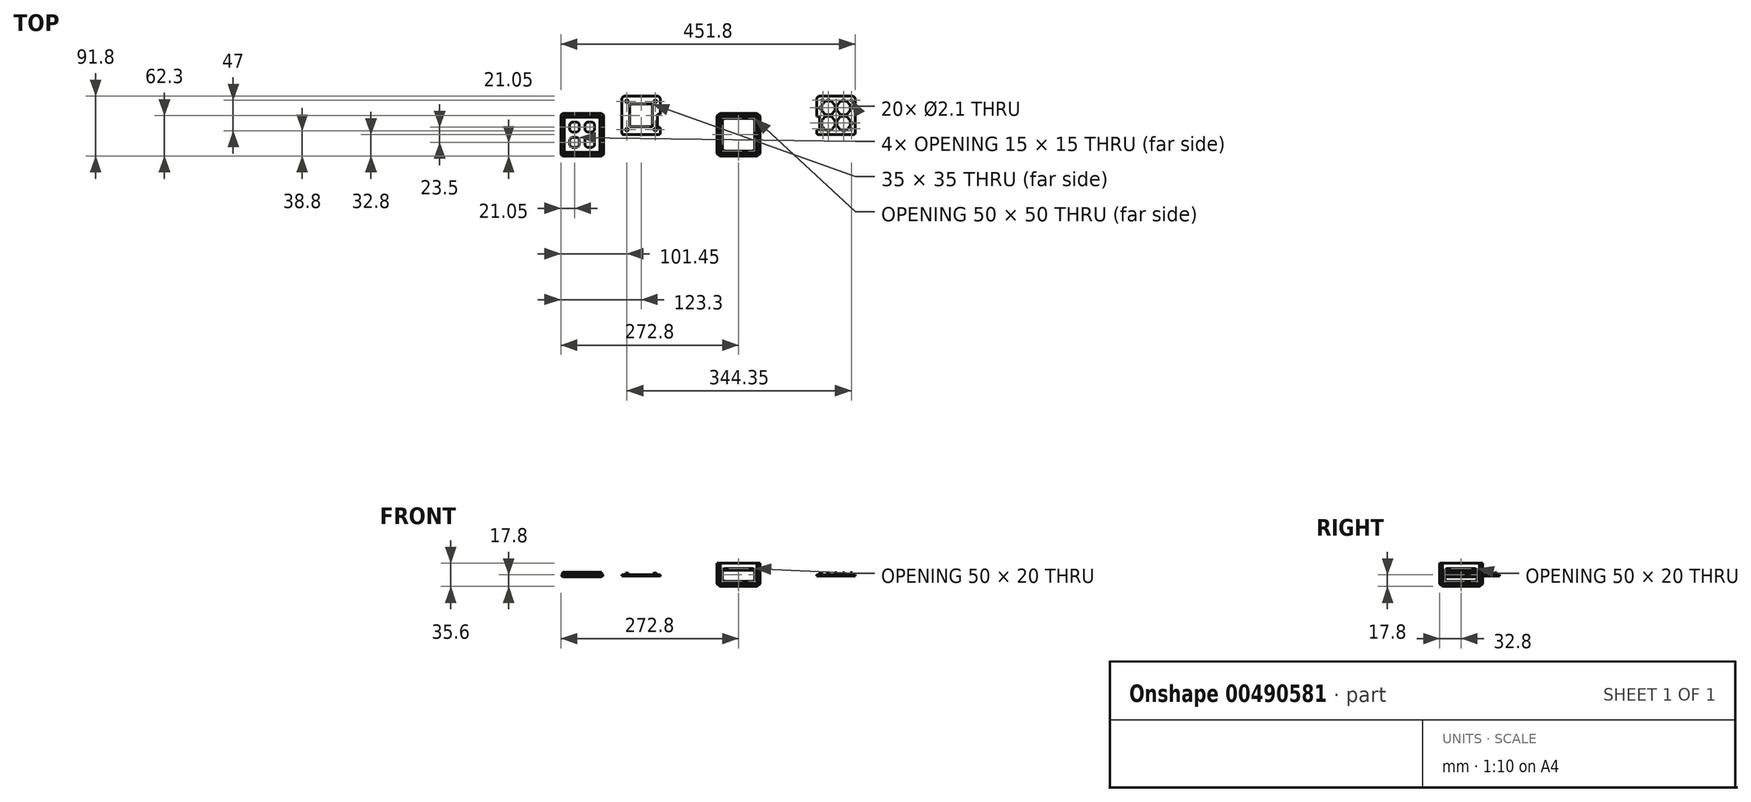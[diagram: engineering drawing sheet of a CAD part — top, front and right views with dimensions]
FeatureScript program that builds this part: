
annotation { "Feature Type Name" : "Feature", "Feature Type Description" : "" }
export const myFeature = defineFeature(function(context is Context, id is Id, definition is map)
    precondition{}
    {
        {
            assignVariable(context, id + "F0", {"name" : "Grosor", "anyValue" : 2.8});
        }
        {
            assignVariable(context, id + "F1", {"name" : "AltoPlaca", "anyValue" : 15});
        }
        {
            assignVariable(context, id + "F2", {"name" : "AltoBriX", "anyValue" : 15});
        }
        {
            var Q0;
            Q0=qCreatedBy(makeId("Top.planeOp"),FACE);
            var sketch = newSketch(context, id + "F3", { "sketchPlane" : qUnion([Q0])});
            skLineSegment(sketch, "E0.bottom", {"start": v(30, -30) * mm, "end": v(-30, -30) * mm});
            skLineSegment(sketch, "E0.top", {"start": v(30, 30) * mm, "end": v(-30, 30) * mm});
            skLineSegment(sketch, "E0.left", {"start": v(30, -30) * mm, "end": v(30, 30) * mm});
            skLineSegment(sketch, "E0.right", {"start": v(-30, -30) * mm, "end": v(-30, 30) * mm});
            skPoint(sketch, "E0.middle", {"position": v(0, 0) * mm});
            skLineSegment(sketch, "E1.0", {"start": v(32.8, 32.8) * mm, "end": v(-32.8, 32.8) * mm});
            skLineSegment(sketch, "E1.1", {"start": v(32.8, -32.8) * mm, "end": v(32.8, 32.8) * mm});
            skLineSegment(sketch, "E1.2", {"start": v(32.8, -32.8) * mm, "end": v(-32.8, -32.8) * mm});
            skLineSegment(sketch, "E1.3", {"start": v(-32.8, -32.8) * mm, "end": v(-32.8, 32.8) * mm});
            skLineSegment(sketch, "E2.bottom", {"start": v(-25, 32.8) * mm, "end": v(25, 32.8) * mm});
            skLineSegment(sketch, "E2.top", {"start": v(-25, -32.8) * mm, "end": v(25, -32.8) * mm});
            skLineSegment(sketch, "E2.left", {"start": v(-25, 32.8) * mm, "end": v(-25, -32.8) * mm});
            skLineSegment(sketch, "E2.right", {"start": v(25, 32.8) * mm, "end": v(25, -32.8) * mm});
            skLineSegment(sketch, "E3.bottom", {"start": v(-32.8, 25) * mm, "end": v(32.8, 25) * mm});
            skLineSegment(sketch, "E3.top", {"start": v(-32.8, -25) * mm, "end": v(32.8, -25) * mm});
            skLineSegment(sketch, "E3.left", {"start": v(-32.8, 25) * mm, "end": v(-32.8, -25) * mm});
            skLineSegment(sketch, "E3.right", {"start": v(32.8, 25) * mm, "end": v(32.8, -25) * mm});
            skSolve(sketch);
        }
        {
            var Q0;
            {var subQ0=sQuery(id+"F3.wireOp",EDGE,"E2.right");var subQ1=sQuery(id+"F3.wireOp",EDGE,"E0.top");var subQ2=makeQuery(id+"F3.imprint","INTERSECT",VERTEX,{"derivedFrom":[subQ1,subQ0]});Q0=makeQuery(id+"F3.imprint","IMPRINT",FACE,{"disambiguationData":[TD([[makeQuery(id+"F3.imprint","IMPRINT",EDGE,{"disambiguationData":[TD([[subQ2,-1.0]])],"derivedFrom":subQ1}),-1.0]])]});}
            var Q1;
            {var subQ7=sQuery(id+"F3.wireOp",EDGE,"E0.right");var subQ8=sQuery(id+"F3.wireOp",EDGE,"E0.top");var subQ9=makeQuery(id+"F3.imprint","INTERSECT",VERTEX,{"derivedFrom":[subQ8,subQ7]});Q1=makeQuery(id+"F3.imprint","IMPRINT",FACE,{"disambiguationData":[TD([[makeQuery(id+"F3.imprint","IMPRINT",EDGE,{"disambiguationData":[TD([[subQ9,1.0]])],"derivedFrom":subQ8}),-1.0]])]});}
            var Q2;
            {var subQ6=sQuery(id+"F3.wireOp",EDGE,"E0.top");var subQ9=sQuery(id+"F3.wireOp",EDGE,"E2.right");var subQ11=makeQuery(id+"F3.imprint","INTERSECT",VERTEX,{"derivedFrom":[subQ6,subQ9]});Q2=makeQuery(id+"F3.imprint","IMPRINT",FACE,{"disambiguationData":[TD([[makeQuery(id+"F3.imprint","IMPRINT",EDGE,{"disambiguationData":[TD([[subQ11,1.0]])],"derivedFrom":subQ6}),-1.0]])]});}
            var Q3;
            {var subQ0=sQuery(id+"F3.wireOp",EDGE,"E3.top");var subQ1=sQuery(id+"F3.wireOp",EDGE,"E0.left");var subQ2=makeQuery(id+"F3.imprint","INTERSECT",VERTEX,{"derivedFrom":[subQ1,subQ0]});Q3=makeQuery(id+"F3.imprint","IMPRINT",FACE,{"disambiguationData":[TD([[makeQuery(id+"F3.imprint","IMPRINT",EDGE,{"disambiguationData":[TD([[subQ2,-1.0]])],"derivedFrom":subQ1}),-1.0]])]});}
            var Q4;
            {var subQ0=sQuery(id+"F3.wireOp",EDGE,"E2.right");var subQ8=sQuery(id+"F3.wireOp",EDGE,"E0.bottom");var subQ11=makeQuery(id+"F3.imprint","INTERSECT",VERTEX,{"derivedFrom":[subQ8,subQ0]});Q4=makeQuery(id+"F3.imprint","IMPRINT",FACE,{"disambiguationData":[TD([[makeQuery(id+"F3.imprint","IMPRINT",EDGE,{"disambiguationData":[TD([[subQ11,1.0]])],"derivedFrom":subQ8}),1.0]])]});}
            var Q5;
            {var subQ0=sQuery(id+"F3.wireOp",EDGE,"E2.right");var subQ1=sQuery(id+"F3.wireOp",EDGE,"E0.bottom");var subQ2=makeQuery(id+"F3.imprint","INTERSECT",VERTEX,{"derivedFrom":[subQ1,subQ0]});Q5=makeQuery(id+"F3.imprint","IMPRINT",FACE,{"disambiguationData":[TD([[makeQuery(id+"F3.imprint","IMPRINT",EDGE,{"disambiguationData":[TD([[subQ2,-1.0]])],"derivedFrom":subQ1}),1.0]])]});}
            var Q6;
            {var subQ6=sQuery(id+"F3.wireOp",EDGE,"E0.right");var subQ9=sQuery(id+"F3.wireOp",EDGE,"E0.bottom");var subQ10=makeQuery(id+"F3.imprint","INTERSECT",VERTEX,{"derivedFrom":[subQ9,subQ6]});Q6=makeQuery(id+"F3.imprint","IMPRINT",FACE,{"disambiguationData":[TD([[makeQuery(id+"F3.imprint","IMPRINT",EDGE,{"disambiguationData":[TD([[subQ10,1.0]])],"derivedFrom":subQ9}),1.0]])]});}
            var Q7;
            {var subQ0=sQuery(id+"F3.wireOp",EDGE,"E3.top");var subQ1=sQuery(id+"F3.wireOp",EDGE,"E0.right");var subQ2=makeQuery(id+"F3.imprint","INTERSECT",VERTEX,{"derivedFrom":[subQ1,subQ0]});Q7=makeQuery(id+"F3.imprint","IMPRINT",FACE,{"disambiguationData":[TD([[makeQuery(id+"F3.imprint","IMPRINT",EDGE,{"disambiguationData":[TD([[subQ2,-1.0]])],"derivedFrom":subQ1}),1.0]])]});}
            var Q8;
            {var subQ0=sQuery(id+"F3.wireOp",EDGE,"E2.right");var subQ1=sQuery(id+"F3.wireOp",EDGE,"E0.bottom");var subQ2=makeQuery(id+"F3.imprint","INTERSECT",VERTEX,{"derivedFrom":[subQ1,subQ0]});Q8=makeQuery(id+"F3.imprint","IMPRINT",FACE,{"disambiguationData":[TD([[makeQuery(id+"F3.imprint","IMPRINT",EDGE,{"disambiguationData":[TD([[subQ2,1.0]])],"derivedFrom":subQ1}),-1.0]])]});}
            var Q9;
            {var subQ0=sQuery(id+"F3.wireOp",EDGE,"E2.right");var subQ1=sQuery(id+"F3.wireOp",EDGE,"E0.top");var subQ2=makeQuery(id+"F3.imprint","INTERSECT",VERTEX,{"derivedFrom":[subQ1,subQ0]});Q9=makeQuery(id+"F3.imprint","IMPRINT",FACE,{"disambiguationData":[TD([[makeQuery(id+"F3.imprint","IMPRINT",EDGE,{"disambiguationData":[TD([[subQ2,1.0]])],"derivedFrom":subQ1}),1.0]])]});}
            var Q10;
            {var subQ0=sQuery(id+"F3.wireOp",EDGE,"E0.right");var subQ1=sQuery(id+"F3.wireOp",EDGE,"E0.top");var subQ2=makeQuery(id+"F3.imprint","INTERSECT",VERTEX,{"derivedFrom":[subQ1,subQ0]});Q10=makeQuery(id+"F3.imprint","IMPRINT",FACE,{"disambiguationData":[TD([[makeQuery(id+"F3.imprint","IMPRINT",EDGE,{"disambiguationData":[TD([[subQ2,1.0]])],"derivedFrom":subQ1}),1.0]])]});}
            var Q11;
            {var subQ0=sQuery(id+"F3.wireOp",EDGE,"E3.top");var subQ1=sQuery(id+"F3.wireOp",EDGE,"E0.right");var subQ2=makeQuery(id+"F3.imprint","INTERSECT",VERTEX,{"derivedFrom":[subQ1,subQ0]});Q11=makeQuery(id+"F3.imprint","IMPRINT",FACE,{"disambiguationData":[TD([[makeQuery(id+"F3.imprint","IMPRINT",EDGE,{"disambiguationData":[TD([[subQ2,-1.0]])],"derivedFrom":subQ1}),-1.0]])]});}
            var Q12;
            {var subQ0=sQuery(id+"F3.wireOp",EDGE,"E3.top");var subQ1=sQuery(id+"F3.wireOp",EDGE,"E0.left");var subQ2=makeQuery(id+"F3.imprint","INTERSECT",VERTEX,{"derivedFrom":[subQ1,subQ0]});Q12=makeQuery(id+"F3.imprint","IMPRINT",FACE,{"disambiguationData":[TD([[makeQuery(id+"F3.imprint","IMPRINT",EDGE,{"disambiguationData":[TD([[subQ2,-1.0]])],"derivedFrom":subQ1}),1.0]])]});}
            var Q13;
            {var subQ0=sQuery(id+"F3.wireOp",EDGE,"E0.right");var subQ1=sQuery(id+"F3.wireOp",EDGE,"E0.bottom");var subQ2=makeQuery(id+"F3.imprint","INTERSECT",VERTEX,{"derivedFrom":[subQ1,subQ0]});Q13=makeQuery(id+"F3.imprint","IMPRINT",FACE,{"disambiguationData":[TD([[makeQuery(id+"F3.imprint","IMPRINT",EDGE,{"disambiguationData":[TD([[subQ2,1.0]])],"derivedFrom":subQ1}),-1.0]])]});}
            var Q14;
            {var subQ0=sQuery(id+"F3.wireOp",EDGE,"E2.right");var subQ1=sQuery(id+"F3.wireOp",EDGE,"E0.bottom");var subQ2=makeQuery(id+"F3.imprint","INTERSECT",VERTEX,{"derivedFrom":[subQ1,subQ0]});Q14=makeQuery(id+"F3.imprint","IMPRINT",FACE,{"disambiguationData":[TD([[makeQuery(id+"F3.imprint","IMPRINT",EDGE,{"disambiguationData":[TD([[subQ2,-1.0]])],"derivedFrom":subQ1}),-1.0]])]});}
            var Q15;
            {var subQ0=sQuery(id+"F3.wireOp",EDGE,"E2.right");var subQ1=sQuery(id+"F3.wireOp",EDGE,"E0.top");var subQ2=makeQuery(id+"F3.imprint","INTERSECT",VERTEX,{"derivedFrom":[subQ1,subQ0]});Q15=makeQuery(id+"F3.imprint","IMPRINT",FACE,{"disambiguationData":[TD([[makeQuery(id+"F3.imprint","IMPRINT",EDGE,{"disambiguationData":[TD([[subQ2,-1.0]])],"derivedFrom":subQ1}),1.0]])]});}
            extrude(context, id + "F4", {"entities" : qUnion([Q0, Q1, Q2, Q3, Q4, Q5, Q6, Q7, Q8, Q9, Q10, Q11, Q12, Q13, Q14, Q15]), "depth" : (getVariable(context, 'AltoBriX') + getVariable(context, 'Grosor')) * mm, "hasSecondDirection" : true, "secondDirectionOppositeDirection" : true, "secondDirectionDepth" : (getVariable(context, 'AltoPlaca') + getVariable(context, 'Grosor')) * mm});
        }
        {
            var Q0;
            {var subQ0=sQuery(id+"F3.wireOp",EDGE,"E3.top");var subQ1=sQuery(id+"F3.wireOp",EDGE,"E0.right");var subQ2=makeQuery(id+"F3.imprint","INTERSECT",VERTEX,{"derivedFrom":[subQ1,subQ0]});Q0=makeQuery(id+"F3.imprint","IMPRINT",FACE,{"disambiguationData":[TD([[makeQuery(id+"F3.imprint","IMPRINT",EDGE,{"disambiguationData":[TD([[subQ2,-1.0]])],"derivedFrom":subQ1}),-1.0]])]});}
            var Q1;
            {var subQ0=sQuery(id+"F3.wireOp",EDGE,"E2.right");var subQ1=sQuery(id+"F3.wireOp",EDGE,"E0.top");var subQ2=makeQuery(id+"F3.imprint","INTERSECT",VERTEX,{"derivedFrom":[subQ1,subQ0]});Q1=makeQuery(id+"F3.imprint","IMPRINT",FACE,{"disambiguationData":[TD([[makeQuery(id+"F3.imprint","IMPRINT",EDGE,{"disambiguationData":[TD([[subQ2,-1.0]])],"derivedFrom":subQ1}),1.0]])]});}
            var Q2;
            {var subQ0=sQuery(id+"F3.wireOp",EDGE,"E0.right");var subQ1=sQuery(id+"F3.wireOp",EDGE,"E0.top");var subQ2=makeQuery(id+"F3.imprint","INTERSECT",VERTEX,{"derivedFrom":[subQ1,subQ0]});Q2=makeQuery(id+"F3.imprint","IMPRINT",FACE,{"disambiguationData":[TD([[makeQuery(id+"F3.imprint","IMPRINT",EDGE,{"disambiguationData":[TD([[subQ2,1.0]])],"derivedFrom":subQ1}),1.0]])]});}
            var Q3;
            {var subQ0=sQuery(id+"F3.wireOp",EDGE,"E3.top");var subQ1=sQuery(id+"F3.wireOp",EDGE,"E0.left");var subQ2=makeQuery(id+"F3.imprint","INTERSECT",VERTEX,{"derivedFrom":[subQ1,subQ0]});Q3=makeQuery(id+"F3.imprint","IMPRINT",FACE,{"disambiguationData":[TD([[makeQuery(id+"F3.imprint","IMPRINT",EDGE,{"disambiguationData":[TD([[subQ2,-1.0]])],"derivedFrom":subQ1}),1.0]])]});}
            var Q4;
            {var subQ0=sQuery(id+"F3.wireOp",EDGE,"E2.right");var subQ1=sQuery(id+"F3.wireOp",EDGE,"E0.top");var subQ2=makeQuery(id+"F3.imprint","INTERSECT",VERTEX,{"derivedFrom":[subQ1,subQ0]});Q4=makeQuery(id+"F3.imprint","IMPRINT",FACE,{"disambiguationData":[TD([[makeQuery(id+"F3.imprint","IMPRINT",EDGE,{"disambiguationData":[TD([[subQ2,1.0]])],"derivedFrom":subQ1}),1.0]])]});}
            var Q5;
            {var subQ0=sQuery(id+"F3.wireOp",EDGE,"E0.right");var subQ1=sQuery(id+"F3.wireOp",EDGE,"E0.bottom");var subQ2=makeQuery(id+"F3.imprint","INTERSECT",VERTEX,{"derivedFrom":[subQ1,subQ0]});Q5=makeQuery(id+"F3.imprint","IMPRINT",FACE,{"disambiguationData":[TD([[makeQuery(id+"F3.imprint","IMPRINT",EDGE,{"disambiguationData":[TD([[subQ2,1.0]])],"derivedFrom":subQ1}),-1.0]])]});}
            var Q6;
            {var subQ0=sQuery(id+"F3.wireOp",EDGE,"E2.right");var subQ1=sQuery(id+"F3.wireOp",EDGE,"E0.bottom");var subQ2=makeQuery(id+"F3.imprint","INTERSECT",VERTEX,{"derivedFrom":[subQ1,subQ0]});Q6=makeQuery(id+"F3.imprint","IMPRINT",FACE,{"disambiguationData":[TD([[makeQuery(id+"F3.imprint","IMPRINT",EDGE,{"disambiguationData":[TD([[subQ2,-1.0]])],"derivedFrom":subQ1}),-1.0]])]});}
            var Q7;
            {var subQ0=sQuery(id+"F3.wireOp",EDGE,"E2.right");var subQ1=sQuery(id+"F3.wireOp",EDGE,"E0.bottom");var subQ2=makeQuery(id+"F3.imprint","INTERSECT",VERTEX,{"derivedFrom":[subQ1,subQ0]});Q7=makeQuery(id+"F3.imprint","IMPRINT",FACE,{"disambiguationData":[TD([[makeQuery(id+"F3.imprint","IMPRINT",EDGE,{"disambiguationData":[TD([[subQ2,1.0]])],"derivedFrom":subQ1}),-1.0]])]});}
            extrude(context, id + "F5", {"entities" : qUnion([Q0, Q1, Q2, Q3, Q4, Q5, Q6, Q7]), "operationType" : NewBodyOperationType.REMOVE, "depth" : (getVariable(context, 'AltoBriX') + getVariable(context, 'Grosor')) * mm, "hasSecondDirection" : true, "secondDirectionOppositeDirection" : true, "secondDirectionDepth" : (getVariable(context, 'AltoPlaca')) * mm});
        }
        {
            var Q0;
            {var subQ0=sQuery(id+"F3.wireOp",EDGE,"E3.top");var subQ1=sQuery(id+"F3.wireOp",EDGE,"E0.right");var subQ2=makeQuery(id+"F3.imprint","INTERSECT",VERTEX,{"derivedFrom":[subQ1,subQ0]});Q0=makeQuery(id+"F3.imprint","IMPRINT",FACE,{"disambiguationData":[TD([[makeQuery(id+"F3.imprint","IMPRINT",EDGE,{"disambiguationData":[TD([[subQ2,-1.0]])],"derivedFrom":subQ1}),1.0]])]});}
            var Q1;
            {var subQ0=sQuery(id+"F3.wireOp",EDGE,"E3.top");var subQ1=sQuery(id+"F3.wireOp",EDGE,"E0.left");var subQ2=makeQuery(id+"F3.imprint","INTERSECT",VERTEX,{"derivedFrom":[subQ1,subQ0]});Q1=makeQuery(id+"F3.imprint","IMPRINT",FACE,{"disambiguationData":[TD([[makeQuery(id+"F3.imprint","IMPRINT",EDGE,{"disambiguationData":[TD([[subQ2,-1.0]])],"derivedFrom":subQ1}),-1.0]])]});}
            var Q2;
            {var subQ0=sQuery(id+"F3.wireOp",EDGE,"E2.right");var subQ1=sQuery(id+"F3.wireOp",EDGE,"E0.bottom");var subQ2=makeQuery(id+"F3.imprint","INTERSECT",VERTEX,{"derivedFrom":[subQ1,subQ0]});Q2=makeQuery(id+"F3.imprint","IMPRINT",FACE,{"disambiguationData":[TD([[makeQuery(id+"F3.imprint","IMPRINT",EDGE,{"disambiguationData":[TD([[subQ2,-1.0]])],"derivedFrom":subQ1}),1.0]])]});}
            var Q3;
            {var subQ0=sQuery(id+"F3.wireOp",EDGE,"E2.right");var subQ1=sQuery(id+"F3.wireOp",EDGE,"E0.top");var subQ2=makeQuery(id+"F3.imprint","INTERSECT",VERTEX,{"derivedFrom":[subQ1,subQ0]});Q3=makeQuery(id+"F3.imprint","IMPRINT",FACE,{"disambiguationData":[TD([[makeQuery(id+"F3.imprint","IMPRINT",EDGE,{"disambiguationData":[TD([[subQ2,-1.0]])],"derivedFrom":subQ1}),-1.0]])]});}
            extrude(context, id + "F6", {"entities" : qUnion([Q0, Q1, Q2, Q3]), "operationType" : NewBodyOperationType.REMOVE, "depth" : (getVariable(context, 'AltoBriX') - 5) * mm, "hasSecondDirection" : true, "secondDirectionOppositeDirection" : true, "secondDirectionDepth" : (getVariable(context, 'AltoPlaca') - 5) * mm});
        }
        {
            var Q0;
            {var subQ0=sQuery(id+"F3.wireOp",EDGE,"E3.bottom");Q0=makeQuery(id+"F6.boolean.opBoolean","COPY",EDGE,{"derivedFrom":makeQuery(id+"F6.opExtrude","CAP_EDGE",EDGE,{"disambiguationData":[OSD([subQ0]),TDD([makeQuery(id+"F3.imprint","IMPRINT",EDGE,{"disambiguationData":[TD([[makeQuery(id+"F3.imprint","INTERSECT",VERTEX,{"derivedFrom":[sQuery(id+"F3.wireOp",EDGE,"E0.right"),subQ0]}),1.0]])],"derivedFrom":subQ0})])],"isStart":false})});}
            var Q1;
            {var subQ0=sQuery(id+"F3.wireOp",EDGE,"E3.bottom");Q1=makeQuery(id+"F6.boolean.opBoolean","COPY",EDGE,{"derivedFrom":makeQuery(id+"F6.opExtrude","CAP_EDGE",EDGE,{"disambiguationData":[OSD([subQ0]),TDD([makeQuery(id+"F3.imprint","IMPRINT",EDGE,{"disambiguationData":[TD([[makeQuery(id+"F3.imprint","INTERSECT",VERTEX,{"derivedFrom":[sQuery(id+"F3.wireOp",EDGE,"E0.right"),subQ0]}),1.0]])],"derivedFrom":subQ0})])],"isStart":true})});}
            var Q2;
            {var subQ0=sQuery(id+"F3.wireOp",EDGE,"E3.top");Q2=makeQuery(id+"F6.boolean.opBoolean","COPY",EDGE,{"derivedFrom":makeQuery(id+"F6.opExtrude","CAP_EDGE",EDGE,{"disambiguationData":[OSD([subQ0]),TDD([makeQuery(id+"F3.imprint","IMPRINT",EDGE,{"disambiguationData":[TD([[makeQuery(id+"F3.imprint","INTERSECT",VERTEX,{"derivedFrom":[sQuery(id+"F3.wireOp",EDGE,"E0.right"),subQ0]}),1.0]])],"derivedFrom":subQ0})])],"isStart":false})});}
            var Q3;
            {var subQ0=sQuery(id+"F3.wireOp",EDGE,"E2.right");Q3=makeQuery(id+"F6.boolean.opBoolean","COPY",EDGE,{"derivedFrom":makeQuery(id+"F6.opExtrude","CAP_EDGE",EDGE,{"disambiguationData":[OSD([subQ0]),TDD([makeQuery(id+"F3.imprint","IMPRINT",EDGE,{"disambiguationData":[TD([[makeQuery(id+"F3.imprint","INTERSECT",VERTEX,{"derivedFrom":[sQuery(id+"F3.wireOp",EDGE,"E0.bottom"),subQ0]}),-1.0]])],"derivedFrom":subQ0})])],"isStart":false})});}
            var Q4;
            {var subQ0=sQuery(id+"F3.wireOp",EDGE,"E3.top");Q4=makeQuery(id+"F6.boolean.opBoolean","COPY",EDGE,{"derivedFrom":makeQuery(id+"F6.opExtrude","CAP_EDGE",EDGE,{"disambiguationData":[OSD([subQ0]),TDD([makeQuery(id+"F3.imprint","IMPRINT",EDGE,{"disambiguationData":[TD([[makeQuery(id+"F3.imprint","INTERSECT",VERTEX,{"derivedFrom":[sQuery(id+"F3.wireOp",EDGE,"E0.left"),subQ0]}),-1.0]])],"derivedFrom":subQ0})])],"isStart":false})});}
            var Q5;
            {var subQ0=sQuery(id+"F3.wireOp",EDGE,"E3.top");Q5=makeQuery(id+"F6.boolean.opBoolean","COPY",EDGE,{"derivedFrom":makeQuery(id+"F6.opExtrude","CAP_EDGE",EDGE,{"disambiguationData":[OSD([subQ0]),TDD([makeQuery(id+"F3.imprint","IMPRINT",EDGE,{"disambiguationData":[TD([[makeQuery(id+"F3.imprint","INTERSECT",VERTEX,{"derivedFrom":[sQuery(id+"F3.wireOp",EDGE,"E0.left"),subQ0]}),-1.0]])],"derivedFrom":subQ0})])],"isStart":true})});}
            var Q6;
            {var subQ0=sQuery(id+"F3.wireOp",EDGE,"E2.right");Q6=makeQuery(id+"F6.boolean.opBoolean","COPY",EDGE,{"derivedFrom":makeQuery(id+"F6.opExtrude","CAP_EDGE",EDGE,{"disambiguationData":[OSD([subQ0]),TDD([makeQuery(id+"F3.imprint","IMPRINT",EDGE,{"disambiguationData":[TD([[makeQuery(id+"F3.imprint","INTERSECT",VERTEX,{"derivedFrom":[sQuery(id+"F3.wireOp",EDGE,"E0.bottom"),subQ0]}),-1.0]])],"derivedFrom":subQ0})])],"isStart":true})});}
            var Q7;
            {var subQ0=sQuery(id+"F3.wireOp",EDGE,"E3.top");Q7=makeQuery(id+"F6.boolean.opBoolean","COPY",EDGE,{"derivedFrom":makeQuery(id+"F6.opExtrude","CAP_EDGE",EDGE,{"disambiguationData":[OSD([subQ0]),TDD([makeQuery(id+"F3.imprint","IMPRINT",EDGE,{"disambiguationData":[TD([[makeQuery(id+"F3.imprint","INTERSECT",VERTEX,{"derivedFrom":[sQuery(id+"F3.wireOp",EDGE,"E0.right"),subQ0]}),1.0]])],"derivedFrom":subQ0})])],"isStart":true})});}
            var Q8;
            {var subQ0=sQuery(id+"F3.wireOp",EDGE,"E2.left");Q8=makeQuery(id+"F6.boolean.opBoolean","COPY",EDGE,{"derivedFrom":makeQuery(id+"F6.opExtrude","CAP_EDGE",EDGE,{"disambiguationData":[OSD([subQ0]),TDD([makeQuery(id+"F3.imprint","IMPRINT",EDGE,{"disambiguationData":[TD([[makeQuery(id+"F3.imprint","INTERSECT",VERTEX,{"derivedFrom":[sQuery(id+"F3.wireOp",EDGE,"E1.2"),subQ0]}),1.0]])],"derivedFrom":subQ0})])],"isStart":true})});}
            var Q9;
            {var subQ0=sQuery(id+"F3.wireOp",EDGE,"E2.left");Q9=makeQuery(id+"F6.boolean.opBoolean","COPY",EDGE,{"derivedFrom":makeQuery(id+"F6.opExtrude","CAP_EDGE",EDGE,{"disambiguationData":[OSD([subQ0]),TDD([makeQuery(id+"F3.imprint","IMPRINT",EDGE,{"disambiguationData":[TD([[makeQuery(id+"F3.imprint","INTERSECT",VERTEX,{"derivedFrom":[sQuery(id+"F3.wireOp",EDGE,"E1.2"),subQ0]}),1.0]])],"derivedFrom":subQ0})])],"isStart":false})});}
            var Q10;
            {var subQ0=sQuery(id+"F3.wireOp",EDGE,"E3.bottom");Q10=makeQuery(id+"F6.boolean.opBoolean","COPY",EDGE,{"derivedFrom":makeQuery(id+"F6.opExtrude","CAP_EDGE",EDGE,{"disambiguationData":[OSD([subQ0]),TDD([makeQuery(id+"F3.imprint","IMPRINT",EDGE,{"disambiguationData":[TD([[makeQuery(id+"F3.imprint","INTERSECT",VERTEX,{"derivedFrom":[sQuery(id+"F3.wireOp",EDGE,"E1.1"),subQ0]}),1.0]])],"derivedFrom":subQ0})])],"isStart":true})});}
            var Q11;
            {var subQ0=sQuery(id+"F3.wireOp",EDGE,"E3.bottom");Q11=makeQuery(id+"F6.boolean.opBoolean","COPY",EDGE,{"derivedFrom":makeQuery(id+"F6.opExtrude","CAP_EDGE",EDGE,{"disambiguationData":[OSD([subQ0]),TDD([makeQuery(id+"F3.imprint","IMPRINT",EDGE,{"disambiguationData":[TD([[makeQuery(id+"F3.imprint","INTERSECT",VERTEX,{"derivedFrom":[sQuery(id+"F3.wireOp",EDGE,"E1.1"),subQ0]}),1.0]])],"derivedFrom":subQ0})])],"isStart":false})});}
            var Q12;
            {var subQ0=sQuery(id+"F3.wireOp",EDGE,"E2.left");Q12=makeQuery(id+"F6.boolean.opBoolean","COPY",EDGE,{"derivedFrom":makeQuery(id+"F6.opExtrude","CAP_EDGE",EDGE,{"disambiguationData":[OSD([subQ0]),TDD([makeQuery(id+"F3.imprint","IMPRINT",EDGE,{"disambiguationData":[TD([[makeQuery(id+"F3.imprint","INTERSECT",VERTEX,{"derivedFrom":[sQuery(id+"F3.wireOp",EDGE,"E1.0"),subQ0]}),-1.0]])],"derivedFrom":subQ0})])],"isStart":false})});}
            var Q13;
            {var subQ0=sQuery(id+"F3.wireOp",EDGE,"E2.left");Q13=makeQuery(id+"F6.boolean.opBoolean","COPY",EDGE,{"derivedFrom":makeQuery(id+"F6.opExtrude","CAP_EDGE",EDGE,{"disambiguationData":[OSD([subQ0]),TDD([makeQuery(id+"F3.imprint","IMPRINT",EDGE,{"disambiguationData":[TD([[makeQuery(id+"F3.imprint","INTERSECT",VERTEX,{"derivedFrom":[sQuery(id+"F3.wireOp",EDGE,"E1.0"),subQ0]}),-1.0]])],"derivedFrom":subQ0})])],"isStart":true})});}
            var Q14;
            {var subQ0=sQuery(id+"F3.wireOp",EDGE,"E2.right");Q14=makeQuery(id+"F6.boolean.opBoolean","COPY",EDGE,{"derivedFrom":makeQuery(id+"F6.opExtrude","CAP_EDGE",EDGE,{"disambiguationData":[OSD([subQ0]),TDD([makeQuery(id+"F3.imprint","IMPRINT",EDGE,{"disambiguationData":[TD([[makeQuery(id+"F3.imprint","INTERSECT",VERTEX,{"derivedFrom":[sQuery(id+"F3.wireOp",EDGE,"E0.top"),subQ0]}),1.0]])],"derivedFrom":subQ0})])],"isStart":false})});}
            var Q15;
            {var subQ0=sQuery(id+"F3.wireOp",EDGE,"E2.right");Q15=makeQuery(id+"F6.boolean.opBoolean","COPY",EDGE,{"derivedFrom":makeQuery(id+"F6.opExtrude","CAP_EDGE",EDGE,{"disambiguationData":[OSD([subQ0]),TDD([makeQuery(id+"F3.imprint","IMPRINT",EDGE,{"disambiguationData":[TD([[makeQuery(id+"F3.imprint","INTERSECT",VERTEX,{"derivedFrom":[sQuery(id+"F3.wireOp",EDGE,"E0.top"),subQ0]}),1.0]])],"derivedFrom":subQ0})])],"isStart":true})});}
            var Q16;
            Q16=makeQuery(id+"F4.opExtrude","SWEPT_EDGE",EDGE,{"disambiguationData":[OSD([sQuery(id+"F3.wireOp",EDGE,"E2.right"),sQuery(id+"F3.wireOp",EDGE,"E3.top")])]});
            var Q17;
            Q17=makeQuery(id+"F4.opExtrude","SWEPT_EDGE",EDGE,{"disambiguationData":[OSD([sQuery(id+"F3.wireOp",EDGE,"E2.left"),sQuery(id+"F3.wireOp",EDGE,"E3.top")])]});
            var Q18;
            Q18=makeQuery(id+"F4.opExtrude","SWEPT_EDGE",EDGE,{"disambiguationData":[OSD([sQuery(id+"F3.wireOp",EDGE,"E2.left"),sQuery(id+"F3.wireOp",EDGE,"E3.bottom")])]});
            var Q19;
            Q19=makeQuery(id+"F4.opExtrude","SWEPT_EDGE",EDGE,{"disambiguationData":[OSD([sQuery(id+"F3.wireOp",EDGE,"E2.right"),sQuery(id+"F3.wireOp",EDGE,"E3.bottom")])]});
            fillet(context, id + "F7", {"entities" : qUnion([Q0, Q1, Q2, Q3, Q4, Q5, Q6, Q7, Q8, Q9, Q10, Q11, Q12, Q13, Q14, Q15, Q16, Q17, Q18, Q19]), "radius" : 5 * mm, "tangentPropagation" : true, "allowEdgeOverflow" : false});
        }
        {
            var Q0;
            Q0=qCreatedBy(makeId("Top.planeOp"),FACE);
            cPlane(context, id + "F8", {"entities" : qUnion([Q0]), "cplaneType" : CPlaneType.OFFSET, "offset" : (getVariable(context, 'AltoBriX') - 5) * mm, "width" : 150 * mm, "height" : 150 * mm});
        }
        {
            var Q0;
            Q0=qCreatedBy(id+"F8.planeOp",FACE);
            var sketch = newSketch(context, id + "F9", { "sketchPlane" : qUnion([Q0])});
            skLineSegment(sketch, "E4", {"start": v(0, 0) * mm, "end": v(-31.4, 0) * mm, "construction": true});
            skLineSegment(sketch, "E5", {"start": v(0, 0) * mm, "end": v(0, 31.4) * mm, "construction": true});
            skLineSegment(sketch, "E6", {"start": v(0, 0) * mm, "end": v(-16.82, 16.82) * mm, "construction": true});
            skLineSegment(sketch, "E7", {"start": v(0, 0) * mm, "end": v(10.62, -10.62) * mm, "construction": true});
            skLineSegment(sketch, "E8.bottom", {"start": v(-0.3, 30.25) * mm, "end": v(0.3, 30.25) * mm});
            skLineSegment(sketch, "E8.top", {"start": v(-0.3, 32.55) * mm, "end": v(0.3, 32.55) * mm});
            skLineSegment(sketch, "E8.left", {"start": v(-0.3, 30.25) * mm, "end": v(-0.3, 32.55) * mm});
            skLineSegment(sketch, "E8.right", {"start": v(0.3, 30.25) * mm, "end": v(0.3, 32.55) * mm});
            skPoint(sketch, "E8.middle", {"position": v(0, 31.4) * mm});
            skLineSegment(sketch, "E9", {"start": v(0, 0) * mm, "end": v(15.28, 0) * mm, "construction": true});
            skLineSegment(sketch, "E10.MirrorCS", {"start": v(0, 0) * mm, "end": v(0, -31.4) * mm, "construction": true});
            skPoint(sketch, "E11.1.0.0", {"position": v(5, 31.4) * mm});
            skPoint(sketch, "E11.1.0.1", {"position": v(5, 31.4) * mm});
            skLineSegment(sketch, "E11.1.0.2", {"start": v(4.7, 30.25) * mm, "end": v(5.3, 30.25) * mm});
            skLineSegment(sketch, "E11.1.0.3", {"start": v(4.7, 32.55) * mm, "end": v(5.3, 32.55) * mm});
            skLineSegment(sketch, "E11.1.0.4", {"start": v(4.7, 30.25) * mm, "end": v(4.7, 32.55) * mm});
            skLineSegment(sketch, "E11.1.0.5", {"start": v(5.3, 30.25) * mm, "end": v(5.3, 32.55) * mm});
            skPoint(sketch, "E11.2.0.0", {"position": v(10, 31.4) * mm});
            skPoint(sketch, "E11.2.0.1", {"position": v(10, 31.4) * mm});
            skLineSegment(sketch, "E11.2.0.2", {"start": v(9.7, 30.25) * mm, "end": v(10.3, 30.25) * mm});
            skLineSegment(sketch, "E11.2.0.3", {"start": v(9.7, 32.55) * mm, "end": v(10.3, 32.55) * mm});
            skLineSegment(sketch, "E11.2.0.4", {"start": v(9.7, 30.25) * mm, "end": v(9.7, 32.55) * mm});
            skLineSegment(sketch, "E11.2.0.5", {"start": v(10.3, 30.25) * mm, "end": v(10.3, 32.55) * mm});
            skPoint(sketch, "E11.3.0.0", {"position": v(15, 31.4) * mm});
            skPoint(sketch, "E11.3.0.1", {"position": v(15, 31.4) * mm});
            skLineSegment(sketch, "E11.3.0.2", {"start": v(14.7, 30.25) * mm, "end": v(15.3, 30.25) * mm});
            skLineSegment(sketch, "E11.3.0.3", {"start": v(14.7, 32.55) * mm, "end": v(15.3, 32.55) * mm});
            skLineSegment(sketch, "E11.3.0.4", {"start": v(14.7, 30.25) * mm, "end": v(14.7, 32.55) * mm});
            skLineSegment(sketch, "E11.3.0.5", {"start": v(15.3, 30.25) * mm, "end": v(15.3, 32.55) * mm});
            skPoint(sketch, "E11.4.0.0", {"position": v(20, 31.4) * mm});
            skPoint(sketch, "E11.4.0.1", {"position": v(20, 31.4) * mm});
            skLineSegment(sketch, "E11.4.0.2", {"start": v(19.7, 30.25) * mm, "end": v(20.3, 30.25) * mm});
            skLineSegment(sketch, "E11.4.0.3", {"start": v(19.7, 32.55) * mm, "end": v(20.3, 32.55) * mm});
            skLineSegment(sketch, "E11.4.0.4", {"start": v(19.7, 30.25) * mm, "end": v(19.7, 32.55) * mm});
            skLineSegment(sketch, "E11.4.0.5", {"start": v(20.3, 30.25) * mm, "end": v(20.3, 32.55) * mm});
            skLineSegment(sketch, "E11.direction1", {"start": v(-0.3, 30.25) * mm, "end": v(4.7, 30.25) * mm, "construction": true});
            skPoint(sketch, "E12.1.0.0", {"position": v(-5, 31.4) * mm});
            skLineSegment(sketch, "E12.1.0.1", {"start": v(-4.7, 30.25) * mm, "end": v(-4.7, 32.55) * mm});
            skLineSegment(sketch, "E12.1.0.2", {"start": v(-5.3, 30.25) * mm, "end": v(-5.3, 32.55) * mm});
            skPoint(sketch, "E12.1.0.3", {"position": v(-5, 31.4) * mm});
            skLineSegment(sketch, "E12.1.0.4", {"start": v(-5.3, 32.55) * mm, "end": v(-4.7, 32.55) * mm});
            skLineSegment(sketch, "E12.1.0.5", {"start": v(-5.3, 30.25) * mm, "end": v(-4.7, 30.25) * mm});
            skPoint(sketch, "E12.2.0.0", {"position": v(-10, 31.4) * mm});
            skLineSegment(sketch, "E12.2.0.1", {"start": v(-9.7, 30.25) * mm, "end": v(-9.7, 32.55) * mm});
            skLineSegment(sketch, "E12.2.0.2", {"start": v(-10.3, 30.25) * mm, "end": v(-10.3, 32.55) * mm});
            skPoint(sketch, "E12.2.0.3", {"position": v(-10, 31.4) * mm});
            skLineSegment(sketch, "E12.2.0.4", {"start": v(-10.3, 32.55) * mm, "end": v(-9.7, 32.55) * mm});
            skLineSegment(sketch, "E12.2.0.5", {"start": v(-10.3, 30.25) * mm, "end": v(-9.7, 30.25) * mm});
            skPoint(sketch, "E12.3.0.0", {"position": v(-15, 31.4) * mm});
            skLineSegment(sketch, "E12.3.0.1", {"start": v(-14.7, 30.25) * mm, "end": v(-14.7, 32.55) * mm});
            skLineSegment(sketch, "E12.3.0.2", {"start": v(-15.3, 30.25) * mm, "end": v(-15.3, 32.55) * mm});
            skPoint(sketch, "E12.3.0.3", {"position": v(-15, 31.4) * mm});
            skLineSegment(sketch, "E12.3.0.4", {"start": v(-15.3, 32.55) * mm, "end": v(-14.7, 32.55) * mm});
            skLineSegment(sketch, "E12.3.0.5", {"start": v(-15.3, 30.25) * mm, "end": v(-14.7, 30.25) * mm});
            skPoint(sketch, "E12.4.0.0", {"position": v(-20, 31.4) * mm});
            skLineSegment(sketch, "E12.4.0.1", {"start": v(-19.7, 30.25) * mm, "end": v(-19.7, 32.55) * mm});
            skLineSegment(sketch, "E12.4.0.2", {"start": v(-20.3, 30.25) * mm, "end": v(-20.3, 32.55) * mm});
            skPoint(sketch, "E12.4.0.3", {"position": v(-20, 31.4) * mm});
            skLineSegment(sketch, "E12.4.0.4", {"start": v(-20.3, 32.55) * mm, "end": v(-19.7, 32.55) * mm});
            skLineSegment(sketch, "E12.4.0.5", {"start": v(-20.3, 30.25) * mm, "end": v(-19.7, 30.25) * mm});
            skLineSegment(sketch, "E12.direction1", {"start": v(-0.3, 30.25) * mm, "end": v(-5.3, 30.25) * mm, "construction": true});
            skLineSegment(sketch, "E13.MirrorCS", {"start": v(-0.3, -30.25) * mm, "end": v(0.3, -30.25) * mm});
            skLineSegment(sketch, "E14.MirrorCS", {"start": v(9.7, -30.25) * mm, "end": v(10.3, -30.25) * mm});
            skLineSegment(sketch, "E15.MirrorCS", {"start": v(5.3, -30.25) * mm, "end": v(5.3, -32.55) * mm});
            skLineSegment(sketch, "E16.MirrorCS", {"start": v(4.7, -30.25) * mm, "end": v(4.7, -32.55) * mm});
            skLineSegment(sketch, "E17.MirrorCS", {"start": v(4.7, -32.55) * mm, "end": v(5.3, -32.55) * mm});
            skLineSegment(sketch, "E18.MirrorCS", {"start": v(4.7, -30.25) * mm, "end": v(5.3, -30.25) * mm});
            skLineSegment(sketch, "E19.MirrorCS", {"start": v(19.7, -30.25) * mm, "end": v(20.3, -30.25) * mm});
            skLineSegment(sketch, "E20.MirrorCS", {"start": v(-0.3, -30.25) * mm, "end": v(-0.3, -32.55) * mm});
            skLineSegment(sketch, "E21.MirrorCS", {"start": v(-0.3, -32.55) * mm, "end": v(0.3, -32.55) * mm});
            skLineSegment(sketch, "E22.MirrorCS", {"start": v(0.3, -30.25) * mm, "end": v(0.3, -32.55) * mm});
            skLineSegment(sketch, "E23.MirrorCS", {"start": v(-5.3, -30.25) * mm, "end": v(-4.7, -30.25) * mm});
            skLineSegment(sketch, "E24.MirrorCS", {"start": v(14.7, -30.25) * mm, "end": v(15.3, -30.25) * mm});
            skLineSegment(sketch, "E25.MirrorCS", {"start": v(20.3, -30.25) * mm, "end": v(20.3, -32.55) * mm});
            skLineSegment(sketch, "E26.MirrorCS", {"start": v(-20.3, -32.55) * mm, "end": v(-19.7, -32.55) * mm});
            skLineSegment(sketch, "E27.MirrorCS", {"start": v(-5.3, -32.55) * mm, "end": v(-4.7, -32.55) * mm});
            skLineSegment(sketch, "E28.MirrorCS", {"start": v(-5.3, -30.25) * mm, "end": v(-5.3, -32.55) * mm});
            skLineSegment(sketch, "E29.MirrorCS", {"start": v(19.7, -30.25) * mm, "end": v(19.7, -32.55) * mm});
            skLineSegment(sketch, "E30.MirrorCS", {"start": v(-20.3, -30.25) * mm, "end": v(-20.3, -32.55) * mm});
            skLineSegment(sketch, "E31.MirrorCS", {"start": v(-4.7, -30.25) * mm, "end": v(-4.7, -32.55) * mm});
            skLineSegment(sketch, "E32.MirrorCS", {"start": v(-0.3, -30.25) * mm, "end": v(-5.3, -30.25) * mm, "construction": true});
            skLineSegment(sketch, "E33.MirrorCS", {"start": v(-20.3, -30.25) * mm, "end": v(-19.7, -30.25) * mm});
            skLineSegment(sketch, "E34.MirrorCS", {"start": v(-15.3, -30.25) * mm, "end": v(-14.7, -30.25) * mm});
            skLineSegment(sketch, "E35.MirrorCS", {"start": v(19.7, -32.55) * mm, "end": v(20.3, -32.55) * mm});
            skLineSegment(sketch, "E36.MirrorCS", {"start": v(-19.7, -30.25) * mm, "end": v(-19.7, -32.55) * mm});
            skLineSegment(sketch, "E37.MirrorCS", {"start": v(15.3, -30.25) * mm, "end": v(15.3, -32.55) * mm});
            skLineSegment(sketch, "E38.MirrorCS", {"start": v(-15.3, -32.55) * mm, "end": v(-14.7, -32.55) * mm});
            skLineSegment(sketch, "E39.MirrorCS", {"start": v(14.7, -30.25) * mm, "end": v(14.7, -32.55) * mm});
            skLineSegment(sketch, "E40.MirrorCS", {"start": v(-15.3, -30.25) * mm, "end": v(-15.3, -32.55) * mm});
            skLineSegment(sketch, "E41.MirrorCS", {"start": v(-10.3, -30.25) * mm, "end": v(-9.7, -30.25) * mm});
            skLineSegment(sketch, "E42.MirrorCS", {"start": v(14.7, -32.55) * mm, "end": v(15.3, -32.55) * mm});
            skLineSegment(sketch, "E43.MirrorCS", {"start": v(-14.7, -30.25) * mm, "end": v(-14.7, -32.55) * mm});
            skLineSegment(sketch, "E44.MirrorCS", {"start": v(-10.3, -30.25) * mm, "end": v(-10.3, -32.55) * mm});
            skLineSegment(sketch, "E45.MirrorCS", {"start": v(9.7, -32.55) * mm, "end": v(10.3, -32.55) * mm});
            skLineSegment(sketch, "E46.MirrorCS", {"start": v(10.3, -30.25) * mm, "end": v(10.3, -32.55) * mm});
            skLineSegment(sketch, "E47.MirrorCS", {"start": v(-10.3, -32.55) * mm, "end": v(-9.7, -32.55) * mm});
            skLineSegment(sketch, "E48.MirrorCS", {"start": v(-9.7, -30.25) * mm, "end": v(-9.7, -32.55) * mm});
            skLineSegment(sketch, "E49.MirrorCS", {"start": v(9.7, -30.25) * mm, "end": v(9.7, -32.55) * mm});
            skPoint(sketch, "E50.MirrorP", {"position": v(0, -31.4) * mm});
            skPoint(sketch, "E51.MirrorP", {"position": v(-15, -31.4) * mm});
            skPoint(sketch, "E52.MirrorP", {"position": v(20, -31.4) * mm});
            skPoint(sketch, "E53.MirrorP", {"position": v(15, -31.4) * mm});
            skLineSegment(sketch, "E54.MirrorCS", {"start": v(-0.3, -30.25) * mm, "end": v(4.7, -30.25) * mm, "construction": true});
            skPoint(sketch, "E55.MirrorP", {"position": v(-5, -31.4) * mm});
            skPoint(sketch, "E56.MirrorP", {"position": v(-20, -31.4) * mm});
            skPoint(sketch, "E57.MirrorP", {"position": v(-10, -31.4) * mm});
            skPoint(sketch, "E58.MirrorP", {"position": v(10, -31.4) * mm});
            skPoint(sketch, "E59.MirrorP", {"position": v(5, -31.4) * mm});
            skLineSegment(sketch, "E60.bottom", {"start": v(-25, 31.25) * mm, "end": v(25, 31.25) * mm});
            skLineSegment(sketch, "E60.top", {"start": v(-25, 31.55) * mm, "end": v(25, 31.55) * mm});
            skLineSegment(sketch, "E60.left", {"start": v(-25, 31.25) * mm, "end": v(-25, 31.55) * mm});
            skLineSegment(sketch, "E60.right", {"start": v(25, 31.25) * mm, "end": v(25, 31.55) * mm});
            skLineSegment(sketch, "E61.MirrorCS", {"start": v(-25, -31.55) * mm, "end": v(25, -31.55) * mm});
            skLineSegment(sketch, "E62.MirrorCS", {"start": v(-25, -31.25) * mm, "end": v(25, -31.25) * mm});
            skLineSegment(sketch, "E63.MirrorCS", {"start": v(25, -31.25) * mm, "end": v(25, -31.55) * mm});
            skLineSegment(sketch, "E64.MirrorCS", {"start": v(-25, -31.25) * mm, "end": v(-25, -31.55) * mm});
            skLineSegment(sketch, "E65.bottom", {"start": v(-32.55, 0.3) * mm, "end": v(-30.25, 0.3) * mm});
            skLineSegment(sketch, "E65.top", {"start": v(-32.55, -0.3) * mm, "end": v(-30.25, -0.3) * mm});
            skLineSegment(sketch, "E65.left", {"start": v(-32.55, 0.3) * mm, "end": v(-32.55, -0.3) * mm});
            skLineSegment(sketch, "E65.right", {"start": v(-30.25, 0.3) * mm, "end": v(-30.25, -0.3) * mm});
            skPoint(sketch, "E65.middle", {"position": v(-31.4, 0) * mm});
            skLineSegment(sketch, "E66.1.0.0", {"start": v(-32.54, -4.7) * mm, "end": v(-32.54, -5.3) * mm});
            skLineSegment(sketch, "E66.1.0.1", {"start": v(-30.24, -4.7) * mm, "end": v(-30.24, -5.3) * mm});
            skPoint(sketch, "E66.1.0.2", {"position": v(-31.4, -5) * mm});
            skLineSegment(sketch, "E66.1.0.3", {"start": v(-32.54, -4.7) * mm, "end": v(-30.24, -4.7) * mm});
            skLineSegment(sketch, "E66.1.0.4", {"start": v(-32.54, -5.3) * mm, "end": v(-30.24, -5.3) * mm});
            skLineSegment(sketch, "E66.2.0.0", {"start": v(-32.53, -9.7) * mm, "end": v(-32.53, -10.3) * mm});
            skLineSegment(sketch, "E66.2.0.1", {"start": v(-30.23, -9.7) * mm, "end": v(-30.23, -10.3) * mm});
            skPoint(sketch, "E66.2.0.2", {"position": v(-31.38, -10) * mm});
            skLineSegment(sketch, "E66.2.0.3", {"start": v(-32.53, -9.7) * mm, "end": v(-30.23, -9.7) * mm});
            skLineSegment(sketch, "E66.2.0.4", {"start": v(-32.53, -10.3) * mm, "end": v(-30.23, -10.3) * mm});
            skLineSegment(sketch, "E66.3.0.0", {"start": v(-32.53, -14.7) * mm, "end": v(-32.53, -15.3) * mm});
            skLineSegment(sketch, "E66.3.0.1", {"start": v(-30.23, -14.7) * mm, "end": v(-30.23, -15.3) * mm});
            skPoint(sketch, "E66.3.0.2", {"position": v(-31.38, -15) * mm});
            skLineSegment(sketch, "E66.3.0.3", {"start": v(-32.53, -14.7) * mm, "end": v(-30.23, -14.7) * mm});
            skLineSegment(sketch, "E66.3.0.4", {"start": v(-32.53, -15.3) * mm, "end": v(-30.23, -15.3) * mm});
            skLineSegment(sketch, "E66.4.0.0", {"start": v(-32.52, -19.7) * mm, "end": v(-32.52, -20.3) * mm});
            skLineSegment(sketch, "E66.4.0.1", {"start": v(-30.22, -19.7) * mm, "end": v(-30.22, -20.3) * mm});
            skPoint(sketch, "E66.4.0.2", {"position": v(-31.37, -20) * mm});
            skLineSegment(sketch, "E66.4.0.3", {"start": v(-32.52, -19.7) * mm, "end": v(-30.22, -19.7) * mm});
            skLineSegment(sketch, "E66.4.0.4", {"start": v(-32.52, -20.3) * mm, "end": v(-30.22, -20.3) * mm});
            skLineSegment(sketch, "E66.5.0.0", {"start": v(-32.5, -24.7) * mm, "end": v(-32.5, -25.3) * mm});
            skLineSegment(sketch, "E66.5.0.1", {"start": v(-30.2, -24.7) * mm, "end": v(-30.2, -25.3) * mm});
            skPoint(sketch, "E66.5.0.2", {"position": v(-31.36, -25) * mm});
            skLineSegment(sketch, "E66.5.0.3", {"start": v(-32.5, -24.7) * mm, "end": v(-30.2, -24.7) * mm});
            skLineSegment(sketch, "E66.5.0.4", {"start": v(-32.5, -25.3) * mm, "end": v(-30.2, -25.3) * mm});
            skLineSegment(sketch, "E66.6.0.0", {"start": v(-32.5, -29.7) * mm, "end": v(-32.5, -30.3) * mm});
            skLineSegment(sketch, "E66.6.0.1", {"start": v(-30.2, -29.7) * mm, "end": v(-30.2, -30.3) * mm});
            skPoint(sketch, "E66.6.0.2", {"position": v(-31.35, -30) * mm});
            skLineSegment(sketch, "E66.6.0.3", {"start": v(-32.5, -29.7) * mm, "end": v(-30.2, -29.7) * mm});
            skLineSegment(sketch, "E66.6.0.4", {"start": v(-32.5, -30.3) * mm, "end": v(-30.2, -30.3) * mm});
            skLineSegment(sketch, "E66.direction1", {"start": v(-32.55, -0.3) * mm, "end": v(-32.54, -5.3) * mm, "construction": true});
            skLineSegment(sketch, "E67.1.0.0", {"start": v(-32.55, 4.7) * mm, "end": v(-30.25, 4.7) * mm});
            skPoint(sketch, "E67.1.0.1", {"position": v(-31.4, 5) * mm});
            skLineSegment(sketch, "E67.1.0.2", {"start": v(-32.55, 5.3) * mm, "end": v(-30.25, 5.3) * mm});
            skLineSegment(sketch, "E67.1.0.3", {"start": v(-30.25, 5.3) * mm, "end": v(-30.25, 4.7) * mm});
            skLineSegment(sketch, "E67.1.0.4", {"start": v(-32.55, 5.3) * mm, "end": v(-32.55, 4.7) * mm});
            skLineSegment(sketch, "E67.2.0.0", {"start": v(-32.55, 9.7) * mm, "end": v(-30.25, 9.7) * mm});
            skPoint(sketch, "E67.2.0.1", {"position": v(-31.4, 10) * mm});
            skLineSegment(sketch, "E67.2.0.2", {"start": v(-32.55, 10.3) * mm, "end": v(-30.25, 10.3) * mm});
            skLineSegment(sketch, "E67.2.0.3", {"start": v(-30.25, 10.3) * mm, "end": v(-30.25, 9.7) * mm});
            skLineSegment(sketch, "E67.2.0.4", {"start": v(-32.55, 10.3) * mm, "end": v(-32.55, 9.7) * mm});
            skLineSegment(sketch, "E67.3.0.0", {"start": v(-32.55, 14.7) * mm, "end": v(-30.25, 14.7) * mm});
            skPoint(sketch, "E67.3.0.1", {"position": v(-31.4, 15) * mm});
            skLineSegment(sketch, "E67.3.0.2", {"start": v(-32.55, 15.3) * mm, "end": v(-30.25, 15.3) * mm});
            skLineSegment(sketch, "E67.3.0.3", {"start": v(-30.25, 15.3) * mm, "end": v(-30.25, 14.7) * mm});
            skLineSegment(sketch, "E67.3.0.4", {"start": v(-32.55, 15.3) * mm, "end": v(-32.55, 14.7) * mm});
            skLineSegment(sketch, "E67.4.0.0", {"start": v(-32.55, 19.7) * mm, "end": v(-30.25, 19.7) * mm});
            skPoint(sketch, "E67.4.0.1", {"position": v(-31.4, 20) * mm});
            skLineSegment(sketch, "E67.4.0.2", {"start": v(-32.55, 20.3) * mm, "end": v(-30.25, 20.3) * mm});
            skLineSegment(sketch, "E67.4.0.3", {"start": v(-30.25, 20.3) * mm, "end": v(-30.25, 19.7) * mm});
            skLineSegment(sketch, "E67.4.0.4", {"start": v(-32.55, 20.3) * mm, "end": v(-32.55, 19.7) * mm});
            skLineSegment(sketch, "E67.5.0.0", {"start": v(-32.55, 24.7) * mm, "end": v(-30.25, 24.7) * mm});
            skPoint(sketch, "E67.5.0.1", {"position": v(-31.4, 25) * mm});
            skLineSegment(sketch, "E67.5.0.2", {"start": v(-32.55, 25.3) * mm, "end": v(-30.25, 25.3) * mm});
            skLineSegment(sketch, "E67.5.0.3", {"start": v(-30.25, 25.3) * mm, "end": v(-30.25, 24.7) * mm});
            skLineSegment(sketch, "E67.5.0.4", {"start": v(-32.55, 25.3) * mm, "end": v(-32.55, 24.7) * mm});
            skLineSegment(sketch, "E67.6.0.0", {"start": v(-32.55, 29.7) * mm, "end": v(-30.25, 29.7) * mm});
            skPoint(sketch, "E67.6.0.1", {"position": v(-31.4, 30) * mm});
            skLineSegment(sketch, "E67.6.0.2", {"start": v(-32.55, 30.3) * mm, "end": v(-30.25, 30.3) * mm});
            skLineSegment(sketch, "E67.6.0.3", {"start": v(-30.25, 30.3) * mm, "end": v(-30.25, 29.7) * mm});
            skLineSegment(sketch, "E67.6.0.4", {"start": v(-32.55, 30.3) * mm, "end": v(-32.55, 29.7) * mm});
            skLineSegment(sketch, "E67.direction1", {"start": v(-32.55, -0.3) * mm, "end": v(-32.55, 4.7) * mm, "construction": true});
            skLineSegment(sketch, "E68.MirrorCS", {"start": v(32.55, 0.3) * mm, "end": v(32.55, -0.3) * mm});
            skLineSegment(sketch, "E69.MirrorCS", {"start": v(32.55, -0.3) * mm, "end": v(30.25, -0.3) * mm});
            skLineSegment(sketch, "E70.MirrorCS", {"start": v(32.55, 0.3) * mm, "end": v(30.25, 0.3) * mm});
            skLineSegment(sketch, "E71.MirrorCS", {"start": v(32.5, -24.7) * mm, "end": v(32.5, -25.3) * mm});
            skLineSegment(sketch, "E72.MirrorCS", {"start": v(32.55, 20.3) * mm, "end": v(32.55, 19.7) * mm});
            skLineSegment(sketch, "E73.MirrorCS", {"start": v(30.2, -24.7) * mm, "end": v(30.2, -25.3) * mm});
            skLineSegment(sketch, "E74.MirrorCS", {"start": v(30.25, 0.3) * mm, "end": v(30.25, -0.3) * mm});
            skLineSegment(sketch, "E75.MirrorCS", {"start": v(30.25, 20.3) * mm, "end": v(30.25, 19.7) * mm});
            skLineSegment(sketch, "E76.MirrorCS", {"start": v(32.5, -24.7) * mm, "end": v(30.2, -24.7) * mm});
            skLineSegment(sketch, "E77.MirrorCS", {"start": v(32.5, -25.3) * mm, "end": v(30.2, -25.3) * mm});
            skLineSegment(sketch, "E78.MirrorCS", {"start": v(32.55, 20.3) * mm, "end": v(30.25, 20.3) * mm});
            skLineSegment(sketch, "E79.MirrorCS", {"start": v(32.55, 19.7) * mm, "end": v(30.25, 19.7) * mm});
            skLineSegment(sketch, "E80.MirrorCS", {"start": v(30.23, -9.7) * mm, "end": v(30.23, -10.3) * mm});
            skLineSegment(sketch, "E81.MirrorCS", {"start": v(30.24, -4.7) * mm, "end": v(30.24, -5.3) * mm});
            skLineSegment(sketch, "E82.MirrorCS", {"start": v(32.52, -20.3) * mm, "end": v(30.22, -20.3) * mm});
            skLineSegment(sketch, "E83.MirrorCS", {"start": v(32.53, -9.7) * mm, "end": v(32.53, -10.3) * mm});
            skLineSegment(sketch, "E84.MirrorCS", {"start": v(32.55, -0.3) * mm, "end": v(32.55, 4.7) * mm, "construction": true});
            skLineSegment(sketch, "E85.MirrorCS", {"start": v(32.53, -10.3) * mm, "end": v(30.23, -10.3) * mm});
            skLineSegment(sketch, "E86.MirrorCS", {"start": v(32.53, -9.7) * mm, "end": v(30.23, -9.7) * mm});
            skLineSegment(sketch, "E87.MirrorCS", {"start": v(32.55, 9.7) * mm, "end": v(30.25, 9.7) * mm});
            skLineSegment(sketch, "E88.MirrorCS", {"start": v(32.55, 29.7) * mm, "end": v(30.25, 29.7) * mm});
            skLineSegment(sketch, "E89.MirrorCS", {"start": v(30.22, -19.7) * mm, "end": v(30.22, -20.3) * mm});
            skLineSegment(sketch, "E90.MirrorCS", {"start": v(30.25, 30.3) * mm, "end": v(30.25, 29.7) * mm});
            skLineSegment(sketch, "E91.MirrorCS", {"start": v(32.52, -19.7) * mm, "end": v(30.22, -19.7) * mm});
            skLineSegment(sketch, "E92.MirrorCS", {"start": v(30.25, 10.3) * mm, "end": v(30.25, 9.7) * mm});
            skLineSegment(sketch, "E93.MirrorCS", {"start": v(32.54, -5.3) * mm, "end": v(30.24, -5.3) * mm});
            skLineSegment(sketch, "E94.MirrorCS", {"start": v(32.55, 5.3) * mm, "end": v(30.25, 5.3) * mm});
            skLineSegment(sketch, "E95.MirrorCS", {"start": v(30.2, -29.7) * mm, "end": v(30.2, -30.3) * mm});
            skLineSegment(sketch, "E96.MirrorCS", {"start": v(30.23, -14.7) * mm, "end": v(30.23, -15.3) * mm});
            skLineSegment(sketch, "E97.MirrorCS", {"start": v(32.55, 4.7) * mm, "end": v(30.25, 4.7) * mm});
            skLineSegment(sketch, "E98.MirrorCS", {"start": v(32.54, -4.7) * mm, "end": v(30.24, -4.7) * mm});
            skLineSegment(sketch, "E99.MirrorCS", {"start": v(32.55, 5.3) * mm, "end": v(32.55, 4.7) * mm});
            skLineSegment(sketch, "E100.MirrorCS", {"start": v(32.55, 30.3) * mm, "end": v(30.25, 30.3) * mm});
            skLineSegment(sketch, "E101.MirrorCS", {"start": v(32.55, 10.3) * mm, "end": v(30.25, 10.3) * mm});
            skLineSegment(sketch, "E102.MirrorCS", {"start": v(32.55, 24.7) * mm, "end": v(30.25, 24.7) * mm});
            skLineSegment(sketch, "E103.MirrorCS", {"start": v(32.5, -30.3) * mm, "end": v(30.2, -30.3) * mm});
            skLineSegment(sketch, "E104.MirrorCS", {"start": v(32.53, -14.7) * mm, "end": v(32.53, -15.3) * mm});
            skLineSegment(sketch, "E105.MirrorCS", {"start": v(32.55, 15.3) * mm, "end": v(32.55, 14.7) * mm});
            skLineSegment(sketch, "E106.MirrorCS", {"start": v(32.55, 10.3) * mm, "end": v(32.55, 9.7) * mm});
            skLineSegment(sketch, "E107.MirrorCS", {"start": v(32.55, 30.3) * mm, "end": v(32.55, 29.7) * mm});
            skLineSegment(sketch, "E108.MirrorCS", {"start": v(32.55, 14.7) * mm, "end": v(30.25, 14.7) * mm});
            skLineSegment(sketch, "E109.MirrorCS", {"start": v(32.54, -4.7) * mm, "end": v(32.54, -5.3) * mm});
            skLineSegment(sketch, "E110.MirrorCS", {"start": v(32.5, -29.7) * mm, "end": v(30.2, -29.7) * mm});
            skLineSegment(sketch, "E111.MirrorCS", {"start": v(32.55, 15.3) * mm, "end": v(30.25, 15.3) * mm});
            skLineSegment(sketch, "E112.MirrorCS", {"start": v(30.25, 15.3) * mm, "end": v(30.25, 14.7) * mm});
            skLineSegment(sketch, "E113.MirrorCS", {"start": v(30.25, 5.3) * mm, "end": v(30.25, 4.7) * mm});
            skLineSegment(sketch, "E114.MirrorCS", {"start": v(32.53, -14.7) * mm, "end": v(30.23, -14.7) * mm});
            skLineSegment(sketch, "E115.MirrorCS", {"start": v(32.55, 25.3) * mm, "end": v(30.25, 25.3) * mm});
            skLineSegment(sketch, "E116.MirrorCS", {"start": v(30.25, 25.3) * mm, "end": v(30.25, 24.7) * mm});
            skLineSegment(sketch, "E117.MirrorCS", {"start": v(32.53, -15.3) * mm, "end": v(30.23, -15.3) * mm});
            skLineSegment(sketch, "E118.MirrorCS", {"start": v(32.5, -29.7) * mm, "end": v(32.5, -30.3) * mm});
            skLineSegment(sketch, "E119.MirrorCS", {"start": v(32.55, -0.3) * mm, "end": v(32.54, -5.3) * mm, "construction": true});
            skLineSegment(sketch, "E120.MirrorCS", {"start": v(32.52, -19.7) * mm, "end": v(32.52, -20.3) * mm});
            skLineSegment(sketch, "E121.MirrorCS", {"start": v(32.55, 25.3) * mm, "end": v(32.55, 24.7) * mm});
            skPoint(sketch, "E122.MirrorP", {"position": v(31.4, 0) * mm});
            skPoint(sketch, "E123.MirrorP", {"position": v(31.38, -10) * mm});
            skPoint(sketch, "E124.MirrorP", {"position": v(31.38, -15) * mm});
            skPoint(sketch, "E125.MirrorP", {"position": v(31.4, 15) * mm});
            skPoint(sketch, "E126.MirrorP", {"position": v(31.4, 30) * mm});
            skPoint(sketch, "E127.MirrorP", {"position": v(31.4, 5) * mm});
            skPoint(sketch, "E128.MirrorP", {"position": v(31.36, -25) * mm});
            skPoint(sketch, "E129.MirrorP", {"position": v(31.35, -30) * mm});
            skPoint(sketch, "E130.MirrorP", {"position": v(31.4, 20) * mm});
            skPoint(sketch, "E131.MirrorP", {"position": v(31.4, 10) * mm});
            skPoint(sketch, "E132.MirrorP", {"position": v(31.4, 25) * mm});
            skPoint(sketch, "E133.MirrorP", {"position": v(31.4, -5) * mm});
            skPoint(sketch, "E134.MirrorP", {"position": v(31.37, -20) * mm});
            skLineSegment(sketch, "E135.bottom", {"start": v(-31.6, -25) * mm, "end": v(-31.2, -25) * mm});
            skLineSegment(sketch, "E135.top", {"start": v(-31.6, 25) * mm, "end": v(-31.2, 25) * mm});
            skLineSegment(sketch, "E135.left", {"start": v(-31.6, -25) * mm, "end": v(-31.6, 25) * mm});
            skLineSegment(sketch, "E135.right", {"start": v(-31.2, -25) * mm, "end": v(-31.2, 25) * mm});
            skLineSegment(sketch, "E136.bottom", {"start": v(31.6, -25) * mm, "end": v(31.2, -25) * mm});
            skLineSegment(sketch, "E136.top", {"start": v(31.6, 25) * mm, "end": v(31.2, 25) * mm});
            skLineSegment(sketch, "E136.left", {"start": v(31.6, -25) * mm, "end": v(31.6, 25) * mm});
            skLineSegment(sketch, "E136.right", {"start": v(31.2, -25) * mm, "end": v(31.2, 25) * mm});
            skSolve(sketch);
        }
        {
            var Q0;
            Q0=qSketchRegion(id+"F9",true);
            extrude(context, id + "F10", {"entities" : qUnion([Q0]), "operationType" : NewBodyOperationType.ADD, "oppositeDirection" : true, "depth" : 3 * mm, "hasDraft" : true, "draftAngle" : 3 * degree});
        }
        {
            var Q0;
            {var subQ5=sQuery(id+"F9.wireOp",EDGE,"E60.left");Q0=makeQuery(id+"F9.imprint","IMPRINT",FACE,{"disambiguationData":[TD([[makeQuery(id+"F9.imprint","IMPRINT",EDGE,{"derivedFrom":subQ5}),-1.0]])]});}
            var Q1;
            {var subQ5=sQuery(id+"F9.wireOp",EDGE,"E60.right");Q1=makeQuery(id+"F9.imprint","IMPRINT",FACE,{"disambiguationData":[TD([[makeQuery(id+"F9.imprint","IMPRINT",EDGE,{"derivedFrom":subQ5}),1.0]])]});}
            var Q2;
            {var subQ0=sQuery(id+"F9.wireOp",EDGE,"E136.left");var subQ1=sQuery(id+"F9.wireOp",EDGE,"E78.MirrorCS");var subQ2=makeQuery(id+"F9.imprint","INTERSECT",VERTEX,{"derivedFrom":[subQ1,subQ0]});Q2=makeQuery(id+"F9.imprint","IMPRINT",FACE,{"disambiguationData":[TD([[makeQuery(id+"F9.imprint","IMPRINT",EDGE,{"disambiguationData":[TD([[subQ2,-1.0]])],"derivedFrom":subQ1}),-1.0]])]});}
            var Q3;
            {var subQ0=sQuery(id+"F9.wireOp",EDGE,"E136.left");var subQ1=sQuery(id+"F9.wireOp",EDGE,"E76.MirrorCS");var subQ2=makeQuery(id+"F9.imprint","INTERSECT",VERTEX,{"derivedFrom":[subQ1,subQ0]});Q3=makeQuery(id+"F9.imprint","IMPRINT",FACE,{"disambiguationData":[TD([[makeQuery(id+"F9.imprint","IMPRINT",EDGE,{"disambiguationData":[TD([[subQ2,-1.0]])],"derivedFrom":subQ1}),-1.0]])]});}
            var Q4;
            {var subQ5=sQuery(id+"F9.wireOp",EDGE,"E63.MirrorCS");Q4=makeQuery(id+"F9.imprint","IMPRINT",FACE,{"disambiguationData":[TD([[makeQuery(id+"F9.imprint","IMPRINT",EDGE,{"derivedFrom":subQ5}),-1.0]])]});}
            var Q5;
            {var subQ5=sQuery(id+"F9.wireOp",EDGE,"E64.MirrorCS");Q5=makeQuery(id+"F9.imprint","IMPRINT",FACE,{"disambiguationData":[TD([[makeQuery(id+"F9.imprint","IMPRINT",EDGE,{"derivedFrom":subQ5}),1.0]])]});}
            var Q6;
            {var subQ0=sQuery(id+"F9.wireOp",EDGE,"E135.left");var subQ1=sQuery(id+"F9.wireOp",EDGE,"E66.4.0.4");var subQ2=makeQuery(id+"F9.imprint","INTERSECT",VERTEX,{"derivedFrom":[subQ1,subQ0]});Q6=makeQuery(id+"F9.imprint","IMPRINT",FACE,{"disambiguationData":[TD([[makeQuery(id+"F9.imprint","IMPRINT",EDGE,{"disambiguationData":[TD([[subQ2,-1.0]])],"derivedFrom":subQ1}),-1.0]])]});}
            var Q7;
            {var subQ0=sQuery(id+"F9.wireOp",EDGE,"E135.left");var subQ1=sQuery(id+"F9.wireOp",EDGE,"E67.4.0.2");var subQ2=makeQuery(id+"F9.imprint","INTERSECT",VERTEX,{"derivedFrom":[subQ1,subQ0]});Q7=makeQuery(id+"F9.imprint","IMPRINT",FACE,{"disambiguationData":[TD([[makeQuery(id+"F9.imprint","IMPRINT",EDGE,{"disambiguationData":[TD([[subQ2,-1.0]])],"derivedFrom":subQ1}),1.0]])]});}
            var Q8;
            {var subQ0=sQuery(id+"F9.wireOp",EDGE,"E60.bottom");var subQ1=sQuery(id+"F9.wireOp",EDGE,"E12.2.0.2");var subQ2=makeQuery(id+"F9.imprint","INTERSECT",VERTEX,{"derivedFrom":[subQ1,subQ0]});Q8=makeQuery(id+"F9.imprint","IMPRINT",FACE,{"disambiguationData":[TD([[makeQuery(id+"F9.imprint","IMPRINT",EDGE,{"disambiguationData":[TD([[subQ2,-1.0]])],"derivedFrom":subQ1}),1.0]])]});}
            var Q9;
            {var subQ0=sQuery(id+"F9.wireOp",EDGE,"E62.MirrorCS");var subQ1=sQuery(id+"F9.wireOp",EDGE,"E36.MirrorCS");var subQ2=makeQuery(id+"F9.imprint","INTERSECT",VERTEX,{"derivedFrom":[subQ1,subQ0]});Q9=makeQuery(id+"F9.imprint","IMPRINT",FACE,{"disambiguationData":[TD([[makeQuery(id+"F9.imprint","IMPRINT",EDGE,{"disambiguationData":[TD([[subQ2,-1.0]])],"derivedFrom":subQ1}),1.0]])]});}
            var Q10;
            {var subQ0=sQuery(id+"F9.wireOp",EDGE,"E62.MirrorCS");var subQ1=sQuery(id+"F9.wireOp",EDGE,"E43.MirrorCS");var subQ2=makeQuery(id+"F9.imprint","INTERSECT",VERTEX,{"derivedFrom":[subQ1,subQ0]});Q10=makeQuery(id+"F9.imprint","IMPRINT",FACE,{"disambiguationData":[TD([[makeQuery(id+"F9.imprint","IMPRINT",EDGE,{"disambiguationData":[TD([[subQ2,-1.0]])],"derivedFrom":subQ1}),1.0]])]});}
            var Q11;
            {var subQ0=sQuery(id+"F9.wireOp",EDGE,"E62.MirrorCS");var subQ1=sQuery(id+"F9.wireOp",EDGE,"E28.MirrorCS");var subQ2=makeQuery(id+"F9.imprint","INTERSECT",VERTEX,{"derivedFrom":[subQ1,subQ0]});Q11=makeQuery(id+"F9.imprint","IMPRINT",FACE,{"disambiguationData":[TD([[makeQuery(id+"F9.imprint","IMPRINT",EDGE,{"disambiguationData":[TD([[subQ2,-1.0]])],"derivedFrom":subQ1}),-1.0]])]});}
            var Q12;
            {var subQ0=sQuery(id+"F9.wireOp",EDGE,"E62.MirrorCS");var subQ1=sQuery(id+"F9.wireOp",EDGE,"E20.MirrorCS");var subQ2=makeQuery(id+"F9.imprint","INTERSECT",VERTEX,{"derivedFrom":[subQ1,subQ0]});Q12=makeQuery(id+"F9.imprint","IMPRINT",FACE,{"disambiguationData":[TD([[makeQuery(id+"F9.imprint","IMPRINT",EDGE,{"disambiguationData":[TD([[subQ2,-1.0]])],"derivedFrom":subQ1}),-1.0]])]});}
            var Q13;
            {var subQ0=sQuery(id+"F9.wireOp",EDGE,"E62.MirrorCS");var subQ1=sQuery(id+"F9.wireOp",EDGE,"E16.MirrorCS");var subQ2=makeQuery(id+"F9.imprint","INTERSECT",VERTEX,{"derivedFrom":[subQ1,subQ0]});Q13=makeQuery(id+"F9.imprint","IMPRINT",FACE,{"disambiguationData":[TD([[makeQuery(id+"F9.imprint","IMPRINT",EDGE,{"disambiguationData":[TD([[subQ2,-1.0]])],"derivedFrom":subQ1}),-1.0]])]});}
            var Q14;
            {var subQ0=sQuery(id+"F9.wireOp",EDGE,"E62.MirrorCS");var subQ1=sQuery(id+"F9.wireOp",EDGE,"E15.MirrorCS");var subQ2=makeQuery(id+"F9.imprint","INTERSECT",VERTEX,{"derivedFrom":[subQ1,subQ0]});Q14=makeQuery(id+"F9.imprint","IMPRINT",FACE,{"disambiguationData":[TD([[makeQuery(id+"F9.imprint","IMPRINT",EDGE,{"disambiguationData":[TD([[subQ2,-1.0]])],"derivedFrom":subQ1}),1.0]])]});}
            var Q15;
            {var subQ0=sQuery(id+"F9.wireOp",EDGE,"E62.MirrorCS");var subQ1=sQuery(id+"F9.wireOp",EDGE,"E29.MirrorCS");var subQ2=makeQuery(id+"F9.imprint","INTERSECT",VERTEX,{"derivedFrom":[subQ1,subQ0]});Q15=makeQuery(id+"F9.imprint","IMPRINT",FACE,{"disambiguationData":[TD([[makeQuery(id+"F9.imprint","IMPRINT",EDGE,{"disambiguationData":[TD([[subQ2,-1.0]])],"derivedFrom":subQ1}),-1.0]])]});}
            var Q16;
            {var subQ0=sQuery(id+"F9.wireOp",EDGE,"E62.MirrorCS");var subQ1=sQuery(id+"F9.wireOp",EDGE,"E39.MirrorCS");var subQ2=makeQuery(id+"F9.imprint","INTERSECT",VERTEX,{"derivedFrom":[subQ1,subQ0]});Q16=makeQuery(id+"F9.imprint","IMPRINT",FACE,{"disambiguationData":[TD([[makeQuery(id+"F9.imprint","IMPRINT",EDGE,{"disambiguationData":[TD([[subQ2,-1.0]])],"derivedFrom":subQ1}),-1.0]])]});}
            var Q17;
            {var subQ0=sQuery(id+"F9.wireOp",EDGE,"E136.left");var subQ1=sQuery(id+"F9.wireOp",EDGE,"E91.MirrorCS");var subQ2=makeQuery(id+"F9.imprint","INTERSECT",VERTEX,{"derivedFrom":[subQ1,subQ0]});Q17=makeQuery(id+"F9.imprint","IMPRINT",FACE,{"disambiguationData":[TD([[makeQuery(id+"F9.imprint","IMPRINT",EDGE,{"disambiguationData":[TD([[subQ2,-1.0]])],"derivedFrom":subQ1}),-1.0]])]});}
            var Q18;
            {var subQ0=sQuery(id+"F9.wireOp",EDGE,"E136.left");var subQ1=sQuery(id+"F9.wireOp",EDGE,"E85.MirrorCS");var subQ2=makeQuery(id+"F9.imprint","INTERSECT",VERTEX,{"derivedFrom":[subQ1,subQ0]});Q18=makeQuery(id+"F9.imprint","IMPRINT",FACE,{"disambiguationData":[TD([[makeQuery(id+"F9.imprint","IMPRINT",EDGE,{"disambiguationData":[TD([[subQ2,-1.0]])],"derivedFrom":subQ1}),1.0]])]});}
            var Q19;
            {var subQ0=sQuery(id+"F9.wireOp",EDGE,"E136.left");var subQ1=sQuery(id+"F9.wireOp",EDGE,"E86.MirrorCS");var subQ2=makeQuery(id+"F9.imprint","INTERSECT",VERTEX,{"derivedFrom":[subQ1,subQ0]});Q19=makeQuery(id+"F9.imprint","IMPRINT",FACE,{"disambiguationData":[TD([[makeQuery(id+"F9.imprint","IMPRINT",EDGE,{"disambiguationData":[TD([[subQ2,-1.0]])],"derivedFrom":subQ1}),-1.0]])]});}
            var Q20;
            {var subQ0=sQuery(id+"F9.wireOp",EDGE,"E136.left");var subQ1=sQuery(id+"F9.wireOp",EDGE,"E69.MirrorCS");var subQ2=makeQuery(id+"F9.imprint","INTERSECT",VERTEX,{"derivedFrom":[subQ1,subQ0]});Q20=makeQuery(id+"F9.imprint","IMPRINT",FACE,{"disambiguationData":[TD([[makeQuery(id+"F9.imprint","IMPRINT",EDGE,{"disambiguationData":[TD([[subQ2,-1.0]])],"derivedFrom":subQ1}),1.0]])]});}
            var Q21;
            {var subQ0=sQuery(id+"F9.wireOp",EDGE,"E136.left");var subQ1=sQuery(id+"F9.wireOp",EDGE,"E87.MirrorCS");var subQ2=makeQuery(id+"F9.imprint","INTERSECT",VERTEX,{"derivedFrom":[subQ1,subQ0]});Q21=makeQuery(id+"F9.imprint","IMPRINT",FACE,{"disambiguationData":[TD([[makeQuery(id+"F9.imprint","IMPRINT",EDGE,{"disambiguationData":[TD([[subQ2,-1.0]])],"derivedFrom":subQ1}),1.0]])]});}
            var Q22;
            {var subQ0=sQuery(id+"F9.wireOp",EDGE,"E136.left");var subQ1=sQuery(id+"F9.wireOp",EDGE,"E70.MirrorCS");var subQ2=makeQuery(id+"F9.imprint","INTERSECT",VERTEX,{"derivedFrom":[subQ1,subQ0]});Q22=makeQuery(id+"F9.imprint","IMPRINT",FACE,{"disambiguationData":[TD([[makeQuery(id+"F9.imprint","IMPRINT",EDGE,{"disambiguationData":[TD([[subQ2,-1.0]])],"derivedFrom":subQ1}),-1.0]])]});}
            var Q23;
            {var subQ0=sQuery(id+"F9.wireOp",EDGE,"E136.left");var subQ1=sQuery(id+"F9.wireOp",EDGE,"E101.MirrorCS");var subQ2=makeQuery(id+"F9.imprint","INTERSECT",VERTEX,{"derivedFrom":[subQ1,subQ0]});Q23=makeQuery(id+"F9.imprint","IMPRINT",FACE,{"disambiguationData":[TD([[makeQuery(id+"F9.imprint","IMPRINT",EDGE,{"disambiguationData":[TD([[subQ2,-1.0]])],"derivedFrom":subQ1}),-1.0]])]});}
            var Q24;
            {var subQ0=sQuery(id+"F9.wireOp",EDGE,"E136.left");var subQ1=sQuery(id+"F9.wireOp",EDGE,"E79.MirrorCS");var subQ2=makeQuery(id+"F9.imprint","INTERSECT",VERTEX,{"derivedFrom":[subQ1,subQ0]});Q24=makeQuery(id+"F9.imprint","IMPRINT",FACE,{"disambiguationData":[TD([[makeQuery(id+"F9.imprint","IMPRINT",EDGE,{"disambiguationData":[TD([[subQ2,-1.0]])],"derivedFrom":subQ1}),1.0]])]});}
            var Q25;
            {var subQ0=sQuery(id+"F9.wireOp",EDGE,"E60.bottom");var subQ1=sQuery(id+"F9.wireOp",EDGE,"E11.3.0.5");var subQ2=makeQuery(id+"F9.imprint","INTERSECT",VERTEX,{"derivedFrom":[subQ1,subQ0]});Q25=makeQuery(id+"F9.imprint","IMPRINT",FACE,{"disambiguationData":[TD([[makeQuery(id+"F9.imprint","IMPRINT",EDGE,{"disambiguationData":[TD([[subQ2,-1.0]])],"derivedFrom":subQ1}),-1.0]])]});}
            var Q26;
            {var subQ0=sQuery(id+"F9.wireOp",EDGE,"E60.bottom");var subQ1=sQuery(id+"F9.wireOp",EDGE,"E11.2.0.5");var subQ2=makeQuery(id+"F9.imprint","INTERSECT",VERTEX,{"derivedFrom":[subQ1,subQ0]});Q26=makeQuery(id+"F9.imprint","IMPRINT",FACE,{"disambiguationData":[TD([[makeQuery(id+"F9.imprint","IMPRINT",EDGE,{"disambiguationData":[TD([[subQ2,-1.0]])],"derivedFrom":subQ1}),-1.0]])]});}
            var Q27;
            {var subQ0=sQuery(id+"F9.wireOp",EDGE,"E60.bottom");var subQ1=sQuery(id+"F9.wireOp",EDGE,"E11.1.0.5");var subQ2=makeQuery(id+"F9.imprint","INTERSECT",VERTEX,{"derivedFrom":[subQ1,subQ0]});Q27=makeQuery(id+"F9.imprint","IMPRINT",FACE,{"disambiguationData":[TD([[makeQuery(id+"F9.imprint","IMPRINT",EDGE,{"disambiguationData":[TD([[subQ2,-1.0]])],"derivedFrom":subQ1}),-1.0]])]});}
            var Q28;
            {var subQ0=sQuery(id+"F9.wireOp",EDGE,"E60.bottom");var subQ1=sQuery(id+"F9.wireOp",EDGE,"E8.right");var subQ2=makeQuery(id+"F9.imprint","INTERSECT",VERTEX,{"derivedFrom":[subQ1,subQ0]});Q28=makeQuery(id+"F9.imprint","IMPRINT",FACE,{"disambiguationData":[TD([[makeQuery(id+"F9.imprint","IMPRINT",EDGE,{"disambiguationData":[TD([[subQ2,-1.0]])],"derivedFrom":subQ1}),-1.0]])]});}
            var Q29;
            {var subQ0=sQuery(id+"F9.wireOp",EDGE,"E60.bottom");var subQ1=sQuery(id+"F9.wireOp",EDGE,"E8.left");var subQ2=makeQuery(id+"F9.imprint","INTERSECT",VERTEX,{"derivedFrom":[subQ1,subQ0]});Q29=makeQuery(id+"F9.imprint","IMPRINT",FACE,{"disambiguationData":[TD([[makeQuery(id+"F9.imprint","IMPRINT",EDGE,{"disambiguationData":[TD([[subQ2,-1.0]])],"derivedFrom":subQ1}),1.0]])]});}
            var Q30;
            {var subQ0=sQuery(id+"F9.wireOp",EDGE,"E60.bottom");var subQ1=sQuery(id+"F9.wireOp",EDGE,"E12.1.0.2");var subQ2=makeQuery(id+"F9.imprint","INTERSECT",VERTEX,{"derivedFrom":[subQ1,subQ0]});Q30=makeQuery(id+"F9.imprint","IMPRINT",FACE,{"disambiguationData":[TD([[makeQuery(id+"F9.imprint","IMPRINT",EDGE,{"disambiguationData":[TD([[subQ2,-1.0]])],"derivedFrom":subQ1}),1.0]])]});}
            var Q31;
            {var subQ0=sQuery(id+"F9.wireOp",EDGE,"E60.bottom");var subQ1=sQuery(id+"F9.wireOp",EDGE,"E12.3.0.2");var subQ2=makeQuery(id+"F9.imprint","INTERSECT",VERTEX,{"derivedFrom":[subQ1,subQ0]});Q31=makeQuery(id+"F9.imprint","IMPRINT",FACE,{"disambiguationData":[TD([[makeQuery(id+"F9.imprint","IMPRINT",EDGE,{"disambiguationData":[TD([[subQ2,-1.0]])],"derivedFrom":subQ1}),1.0]])]});}
            var Q32;
            {var subQ0=sQuery(id+"F9.wireOp",EDGE,"E135.left");var subQ1=sQuery(id+"F9.wireOp",EDGE,"E67.3.0.2");var subQ2=makeQuery(id+"F9.imprint","INTERSECT",VERTEX,{"derivedFrom":[subQ1,subQ0]});Q32=makeQuery(id+"F9.imprint","IMPRINT",FACE,{"disambiguationData":[TD([[makeQuery(id+"F9.imprint","IMPRINT",EDGE,{"disambiguationData":[TD([[subQ2,-1.0]])],"derivedFrom":subQ1}),1.0]])]});}
            var Q33;
            {var subQ0=sQuery(id+"F9.wireOp",EDGE,"E135.left");var subQ1=sQuery(id+"F9.wireOp",EDGE,"E67.2.0.2");var subQ2=makeQuery(id+"F9.imprint","INTERSECT",VERTEX,{"derivedFrom":[subQ1,subQ0]});Q33=makeQuery(id+"F9.imprint","IMPRINT",FACE,{"disambiguationData":[TD([[makeQuery(id+"F9.imprint","IMPRINT",EDGE,{"disambiguationData":[TD([[subQ2,-1.0]])],"derivedFrom":subQ1}),1.0]])]});}
            var Q34;
            {var subQ0=sQuery(id+"F9.wireOp",EDGE,"E135.left");var subQ1=sQuery(id+"F9.wireOp",EDGE,"E67.1.0.2");var subQ2=makeQuery(id+"F9.imprint","INTERSECT",VERTEX,{"derivedFrom":[subQ1,subQ0]});Q34=makeQuery(id+"F9.imprint","IMPRINT",FACE,{"disambiguationData":[TD([[makeQuery(id+"F9.imprint","IMPRINT",EDGE,{"disambiguationData":[TD([[subQ2,-1.0]])],"derivedFrom":subQ1}),1.0]])]});}
            var Q35;
            {var subQ0=sQuery(id+"F9.wireOp",EDGE,"E135.left");var subQ1=sQuery(id+"F9.wireOp",EDGE,"E65.bottom");var subQ2=makeQuery(id+"F9.imprint","INTERSECT",VERTEX,{"derivedFrom":[subQ1,subQ0]});Q35=makeQuery(id+"F9.imprint","IMPRINT",FACE,{"disambiguationData":[TD([[makeQuery(id+"F9.imprint","IMPRINT",EDGE,{"disambiguationData":[TD([[subQ2,-1.0]])],"derivedFrom":subQ1}),1.0]])]});}
            var Q36;
            {var subQ0=sQuery(id+"F9.wireOp",EDGE,"E135.left");var subQ1=sQuery(id+"F9.wireOp",EDGE,"E66.1.0.4");var subQ2=makeQuery(id+"F9.imprint","INTERSECT",VERTEX,{"derivedFrom":[subQ1,subQ0]});Q36=makeQuery(id+"F9.imprint","IMPRINT",FACE,{"disambiguationData":[TD([[makeQuery(id+"F9.imprint","IMPRINT",EDGE,{"disambiguationData":[TD([[subQ2,-1.0]])],"derivedFrom":subQ1}),-1.0]])]});}
            var Q37;
            {var subQ0=sQuery(id+"F9.wireOp",EDGE,"E135.left");var subQ1=sQuery(id+"F9.wireOp",EDGE,"E65.top");var subQ2=makeQuery(id+"F9.imprint","INTERSECT",VERTEX,{"derivedFrom":[subQ1,subQ0]});Q37=makeQuery(id+"F9.imprint","IMPRINT",FACE,{"disambiguationData":[TD([[makeQuery(id+"F9.imprint","IMPRINT",EDGE,{"disambiguationData":[TD([[subQ2,-1.0]])],"derivedFrom":subQ1}),-1.0]])]});}
            var Q38;
            {var subQ0=sQuery(id+"F9.wireOp",EDGE,"E135.left");var subQ1=sQuery(id+"F9.wireOp",EDGE,"E66.2.0.4");var subQ2=makeQuery(id+"F9.imprint","INTERSECT",VERTEX,{"derivedFrom":[subQ1,subQ0]});Q38=makeQuery(id+"F9.imprint","IMPRINT",FACE,{"disambiguationData":[TD([[makeQuery(id+"F9.imprint","IMPRINT",EDGE,{"disambiguationData":[TD([[subQ2,-1.0]])],"derivedFrom":subQ1}),-1.0]])]});}
            var Q39;
            {var subQ0=sQuery(id+"F9.wireOp",EDGE,"E135.left");var subQ1=sQuery(id+"F9.wireOp",EDGE,"E66.3.0.4");var subQ2=makeQuery(id+"F9.imprint","INTERSECT",VERTEX,{"derivedFrom":[subQ1,subQ0]});Q39=makeQuery(id+"F9.imprint","IMPRINT",FACE,{"disambiguationData":[TD([[makeQuery(id+"F9.imprint","IMPRINT",EDGE,{"disambiguationData":[TD([[subQ2,-1.0]])],"derivedFrom":subQ1}),-1.0]])]});}
            extrude(context, id + "F11", {"entities" : qUnion([Q0, Q1, Q2, Q3, Q4, Q5, Q6, Q7, Q8, Q9, Q10, Q11, Q12, Q13, Q14, Q15, Q16, Q17, Q18, Q19, Q20, Q21, Q22, Q23, Q24, Q25, Q26, Q27, Q28, Q29, Q30, Q31, Q32, Q33, Q34, Q35, Q36, Q37, Q38, Q39]), "operationType" : NewBodyOperationType.REMOVE, "oppositeDirection" : true, "depth" : 2 * mm, "hasDraft" : true, "draftAngle" : 3 * degree});
        }
        {
            var Q0;
            {var subQ0=sQuery(id+"F3.wireOp",EDGE,"E0.right");var subQ1=sQuery(id+"F3.wireOp",EDGE,"E0.top");var subQ2=makeQuery(id+"F3.imprint","INTERSECT",VERTEX,{"derivedFrom":[subQ1,subQ0]});Q0=makeQuery(id+"F3.imprint","IMPRINT",FACE,{"disambiguationData":[TD([[makeQuery(id+"F3.imprint","IMPRINT",EDGE,{"disambiguationData":[TD([[subQ2,1.0]])],"derivedFrom":subQ1}),1.0]])]});}
            var Q1;
            {var subQ0=sQuery(id+"F3.wireOp",EDGE,"E2.right");var subQ1=sQuery(id+"F3.wireOp",EDGE,"E0.top");var subQ2=makeQuery(id+"F3.imprint","INTERSECT",VERTEX,{"derivedFrom":[subQ1,subQ0]});Q1=makeQuery(id+"F3.imprint","IMPRINT",FACE,{"disambiguationData":[TD([[makeQuery(id+"F3.imprint","IMPRINT",EDGE,{"disambiguationData":[TD([[subQ2,1.0]])],"derivedFrom":subQ1}),1.0]])]});}
            var Q2;
            {var subQ0=sQuery(id+"F3.wireOp",EDGE,"E2.right");var subQ1=sQuery(id+"F3.wireOp",EDGE,"E0.bottom");var subQ2=makeQuery(id+"F3.imprint","INTERSECT",VERTEX,{"derivedFrom":[subQ1,subQ0]});Q2=makeQuery(id+"F3.imprint","IMPRINT",FACE,{"disambiguationData":[TD([[makeQuery(id+"F3.imprint","IMPRINT",EDGE,{"disambiguationData":[TD([[subQ2,1.0]])],"derivedFrom":subQ1}),-1.0]])]});}
            var Q3;
            {var subQ0=sQuery(id+"F3.wireOp",EDGE,"E0.right");var subQ1=sQuery(id+"F3.wireOp",EDGE,"E0.bottom");var subQ2=makeQuery(id+"F3.imprint","INTERSECT",VERTEX,{"derivedFrom":[subQ1,subQ0]});Q3=makeQuery(id+"F3.imprint","IMPRINT",FACE,{"disambiguationData":[TD([[makeQuery(id+"F3.imprint","IMPRINT",EDGE,{"disambiguationData":[TD([[subQ2,1.0]])],"derivedFrom":subQ1}),-1.0]])]});}
            extrude(context, id + "F12", {"entities" : qUnion([Q0, Q1, Q2, Q3]), "operationType" : NewBodyOperationType.ADD, "endBound" : BoundingType.SYMMETRIC, "depth" : (getVariable(context, 'Grosor')) * mm});
        }
        {
            var Q0;
            Q0=makeQuery(id+"F12.opExtrude","SWEPT_EDGE",EDGE,{"disambiguationData":[OSD([sQuery(id+"F3.wireOp",EDGE,"E2.left"),sQuery(id+"F3.wireOp",EDGE,"E3.bottom")])]});
            var Q1;
            Q1=makeQuery(id+"F12.opExtrude","SWEPT_EDGE",EDGE,{"disambiguationData":[OSD([sQuery(id+"F3.wireOp",EDGE,"E2.right"),sQuery(id+"F3.wireOp",EDGE,"E3.bottom")])]});
            var Q2;
            Q2=makeQuery(id+"F12.opExtrude","SWEPT_EDGE",EDGE,{"disambiguationData":[OSD([sQuery(id+"F3.wireOp",EDGE,"E2.right"),sQuery(id+"F3.wireOp",EDGE,"E3.top")])]});
            var Q3;
            Q3=makeQuery(id+"F12.opExtrude","SWEPT_EDGE",EDGE,{"disambiguationData":[OSD([sQuery(id+"F3.wireOp",EDGE,"E2.left"),sQuery(id+"F3.wireOp",EDGE,"E3.top")])]});
            chamfer(context, id + "F13", {"entities" : qUnion([Q0, Q1, Q2, Q3]), "width" : 5 * mm, "tangentPropagation" : true});
        }
        {
            var Q0;
            {var subQ0=sQuery(id+"F3.wireOp",EDGE,"E1.3");Q0=makeQuery(id+"F3vxCluZQKjuGS6_1.boolean.opBoolean","MERGE",EDGE,{"derivedFrom":[makeQuery(id+"F6.opExtrude","CAP_EDGE",EDGE,{"disambiguationData":[OSD([subQ0]),TDD([makeQuery(id+"F3.imprint","IMPRINT",EDGE,{"disambiguationData":[TD([[makeQuery(id+"F3.imprint","INTERSECT",VERTEX,{"derivedFrom":[sQuery(id+"F3.wireOp",EDGE,"E1.2"),subQ0]}),-1.0]])],"derivedFrom":subQ0})])],"isStart":false}),makeQuery(id+"F6.opExtrude","CAP_EDGE",EDGE,{"disambiguationData":[OSD([subQ0]),TDD([makeQuery(id+"F3.imprint","IMPRINT",EDGE,{"disambiguationData":[TD([[makeQuery(id+"F3.imprint","INTERSECT",VERTEX,{"derivedFrom":[sQuery(id+"F3.wireOp",EDGE,"E1.0"),subQ0]}),1.0]])],"derivedFrom":subQ0})])],"isStart":false}),makeQuery(id+"F3vxCluZQKjuGS6_1.opExtrude","CAP_EDGE",EDGE,{"disambiguationData":[OSD([sQuery(id+"FG7JfQnFfKm0W8e.wireOp",EDGE,"a4df6a7b-901c-458c-aeef-db07d71890a7.3"),sQuery(id+"FG7JfQnFfKm0W8e.wireOp",EDGE,"3a78ae17-f210-4514-9efc-eef556d70575.left")])],"isStart":true})]});}
            var Q1;
            {var subQ0=sQuery(id+"F3.wireOp",EDGE,"E1.0");Q1=makeQuery(id+"F3vxCluZQKjuGS6_1.boolean.opBoolean","MERGE",EDGE,{"derivedFrom":[makeQuery(id+"F6.opExtrude","CAP_EDGE",EDGE,{"disambiguationData":[OSD([subQ0]),TDD([makeQuery(id+"F3.imprint","IMPRINT",EDGE,{"disambiguationData":[TD([[makeQuery(id+"F3.imprint","INTERSECT",VERTEX,{"derivedFrom":[subQ0,sQuery(id+"F3.wireOp",EDGE,"E1.1")]}),-1.0]])],"derivedFrom":subQ0})])],"isStart":false}),makeQuery(id+"F6.opExtrude","CAP_EDGE",EDGE,{"disambiguationData":[OSD([subQ0]),TDD([makeQuery(id+"F3.imprint","IMPRINT",EDGE,{"disambiguationData":[TD([[makeQuery(id+"F3.imprint","INTERSECT",VERTEX,{"derivedFrom":[subQ0,sQuery(id+"F3.wireOp",EDGE,"E1.3")]}),1.0]])],"derivedFrom":subQ0})])],"isStart":false}),makeQuery(id+"F3vxCluZQKjuGS6_1.opExtrude","CAP_EDGE",EDGE,{"disambiguationData":[OSD([sQuery(id+"FG7JfQnFfKm0W8e.wireOp",EDGE,"a4df6a7b-901c-458c-aeef-db07d71890a7.0"),sQuery(id+"FG7JfQnFfKm0W8e.wireOp",EDGE,"28a57de8-ee20-4f04-b501-8f9bbeeccb0a.bottom")])],"isStart":true})]});}
            var Q2;
            Q2=makeQuery(id+"F4.opExtrude","SWEPT_EDGE",EDGE,{"disambiguationData":[OSD([sQuery(id+"F3.wireOp",EDGE,"E1.0"),sQuery(id+"F3.wireOp",EDGE,"E1.3")])]});
            var Q3;
            {var subQ0=sQuery(id+"F3.wireOp",EDGE,"E1.1");Q3=makeQuery(id+"F3vxCluZQKjuGS6_1.boolean.opBoolean","MERGE",EDGE,{"derivedFrom":[makeQuery(id+"F6.opExtrude","CAP_EDGE",EDGE,{"disambiguationData":[OSD([subQ0]),TDD([makeQuery(id+"F3.imprint","IMPRINT",EDGE,{"disambiguationData":[TD([[makeQuery(id+"F3.imprint","INTERSECT",VERTEX,{"derivedFrom":[subQ0,sQuery(id+"F3.wireOp",EDGE,"E1.2")]}),-1.0]])],"derivedFrom":subQ0})])],"isStart":false}),makeQuery(id+"F6.opExtrude","CAP_EDGE",EDGE,{"disambiguationData":[OSD([subQ0]),TDD([makeQuery(id+"F3.imprint","IMPRINT",EDGE,{"disambiguationData":[TD([[makeQuery(id+"F3.imprint","INTERSECT",VERTEX,{"derivedFrom":[sQuery(id+"F3.wireOp",EDGE,"E1.0"),subQ0]}),1.0]])],"derivedFrom":subQ0})])],"isStart":false}),makeQuery(id+"F3vxCluZQKjuGS6_1.opExtrude","CAP_EDGE",EDGE,{"disambiguationData":[OSD([sQuery(id+"FG7JfQnFfKm0W8e.wireOp",EDGE,"a4df6a7b-901c-458c-aeef-db07d71890a7.1"),sQuery(id+"FG7JfQnFfKm0W8e.wireOp",EDGE,"3a78ae17-f210-4514-9efc-eef556d70575.right")])],"isStart":true})]});}
            var Q4;
            Q4=makeQuery(id+"F4.opExtrude","SWEPT_EDGE",EDGE,{"disambiguationData":[OSD([sQuery(id+"F3.wireOp",EDGE,"E1.0"),sQuery(id+"F3.wireOp",EDGE,"E1.1")])]});
            var Q5;
            Q5=makeQuery(id+"F4.opExtrude","SWEPT_EDGE",EDGE,{"disambiguationData":[OSD([sQuery(id+"F3.wireOp",EDGE,"E1.1"),sQuery(id+"F3.wireOp",EDGE,"E1.2")])]});
            var Q6;
            Q6=makeQuery(id+"F4.opExtrude","SWEPT_EDGE",EDGE,{"disambiguationData":[OSD([sQuery(id+"F3.wireOp",EDGE,"E1.2"),sQuery(id+"F3.wireOp",EDGE,"E1.3")])]});
            var Q7;
            {var subQ0=sQuery(id+"F3.wireOp",EDGE,"E1.2");Q7=makeQuery(id+"F3vxCluZQKjuGS6_1.boolean.opBoolean","MERGE",EDGE,{"derivedFrom":[makeQuery(id+"F6.opExtrude","CAP_EDGE",EDGE,{"disambiguationData":[OSD([subQ0]),TDD([makeQuery(id+"F3.imprint","IMPRINT",EDGE,{"disambiguationData":[TD([[makeQuery(id+"F3.imprint","INTERSECT",VERTEX,{"derivedFrom":[sQuery(id+"F3.wireOp",EDGE,"E1.1"),subQ0]}),-1.0]])],"derivedFrom":subQ0})])],"isStart":false}),makeQuery(id+"F6.opExtrude","CAP_EDGE",EDGE,{"disambiguationData":[OSD([subQ0]),TDD([makeQuery(id+"F3.imprint","IMPRINT",EDGE,{"disambiguationData":[TD([[makeQuery(id+"F3.imprint","INTERSECT",VERTEX,{"derivedFrom":[subQ0,sQuery(id+"F3.wireOp",EDGE,"E1.3")]}),1.0]])],"derivedFrom":subQ0})])],"isStart":false}),makeQuery(id+"F3vxCluZQKjuGS6_1.opExtrude","CAP_EDGE",EDGE,{"disambiguationData":[OSD([sQuery(id+"FG7JfQnFfKm0W8e.wireOp",EDGE,"a4df6a7b-901c-458c-aeef-db07d71890a7.2"),sQuery(id+"FG7JfQnFfKm0W8e.wireOp",EDGE,"28a57de8-ee20-4f04-b501-8f9bbeeccb0a.top")])],"isStart":true})]});}
            var Q8;
            Q8=makeQuery(id+"F4.opExtrude","CAP_EDGE",EDGE,{"disambiguationData":[OSD([sQuery(id+"F3.wireOp",EDGE,"E1.2")])],"isStart":true});
            var Q9;
            Q9=makeQuery(id+"F4.opExtrude","CAP_EDGE",EDGE,{"disambiguationData":[OSD([sQuery(id+"F3.wireOp",EDGE,"E1.0")])],"isStart":true});
            var Q10;
            Q10=makeQuery(id+"F4.opExtrude","CAP_EDGE",EDGE,{"disambiguationData":[OSD([sQuery(id+"F3.wireOp",EDGE,"E1.1")])],"isStart":true});
            var Q11;
            Q11=makeQuery(id+"F4.opExtrude","CAP_EDGE",EDGE,{"disambiguationData":[OSD([sQuery(id+"F3.wireOp",EDGE,"E1.3")])],"isStart":true});
            chamfer(context, id + "F14", {"entities" : qUnion([Q0, Q1, Q2, Q3, Q4, Q5, Q6, Q7, Q8, Q9, Q10, Q11]), "width" : 4 * mm, "tangentPropagation" : true});
        }
        {
            var Q0;
            Q0=makeQuery(id+"F5.boolean.opBoolean","COPY",EDGE,{"derivedFrom":makeQuery(id+"F5.opExtrude","CAP_EDGE",EDGE,{"disambiguationData":[OSD([sQuery(id+"F3.wireOp",EDGE,"E0.left")])],"isStart":true})});
            var Q1;
            Q1=makeQuery(id+"F5.boolean.opBoolean","COPY",EDGE,{"derivedFrom":makeQuery(id+"F5.opExtrude","CAP_EDGE",EDGE,{"disambiguationData":[OSD([sQuery(id+"F3.wireOp",EDGE,"E0.bottom")])],"isStart":true})});
            var Q2;
            Q2=makeQuery(id+"F5.boolean.opBoolean","COPY",EDGE,{"derivedFrom":makeQuery(id+"F5.opExtrude","CAP_EDGE",EDGE,{"disambiguationData":[OSD([sQuery(id+"F3.wireOp",EDGE,"E0.top")])],"isStart":true})});
            var Q3;
            Q3=makeQuery(id+"F5.boolean.opBoolean","COPY",EDGE,{"derivedFrom":makeQuery(id+"F5.opExtrude","CAP_EDGE",EDGE,{"disambiguationData":[OSD([sQuery(id+"F3.wireOp",EDGE,"E0.right")])],"isStart":true})});
            var Q4;
            {var subQ0=sQuery(id+"F3.wireOp",EDGE,"E3.bottom");var subQ1=sQuery(id+"F3.wireOp",EDGE,"E2.left");var subQ2=sQuery(id+"F3.wireOp",EDGE,"E0.right");var subQ3=sQuery(id+"F3.wireOp",EDGE,"E0.top");Q4=makeQuery(id+"F12.boolean.opBoolean","SPLIT",EDGE,{"disambiguationData":[TD([makeQuery(id+"F12.opExtrude","CAP_FACE",FACE,{"disambiguationData":[OSD([subQ3,subQ2,subQ1,subQ0])],"isStart":true})])],"derivedFrom":makeQuery(id+"F5.boolean.opBoolean","COPY",EDGE,{"derivedFrom":makeQuery(id+"F5.opExtrude","SWEPT_EDGE",EDGE,{"disambiguationData":[OSD([subQ3,subQ2])]})})});}
            var Q5;
            {var subQ0=sQuery(id+"F3.wireOp",EDGE,"E3.bottom");var subQ1=sQuery(id+"F3.wireOp",EDGE,"E2.right");var subQ2=sQuery(id+"F3.wireOp",EDGE,"E0.left");var subQ3=sQuery(id+"F3.wireOp",EDGE,"E0.top");Q5=makeQuery(id+"F12.boolean.opBoolean","SPLIT",EDGE,{"disambiguationData":[TD([makeQuery(id+"F12.opExtrude","CAP_FACE",FACE,{"disambiguationData":[OSD([subQ3,subQ2,subQ1,subQ0])],"isStart":true})])],"derivedFrom":makeQuery(id+"F5.boolean.opBoolean","COPY",EDGE,{"derivedFrom":makeQuery(id+"F5.opExtrude","SWEPT_EDGE",EDGE,{"disambiguationData":[OSD([subQ3,subQ2])]})})});}
            var Q6;
            {var subQ0=sQuery(id+"F3.wireOp",EDGE,"E0.bottom");var subQ1=sQuery(id+"F3.wireOp",EDGE,"E3.top");var subQ2=sQuery(id+"F3.wireOp",EDGE,"E2.right");var subQ3=sQuery(id+"F3.wireOp",EDGE,"E0.left");Q6=makeQuery(id+"F12.boolean.opBoolean","SPLIT",EDGE,{"disambiguationData":[TD([makeQuery(id+"F12.opExtrude","CAP_FACE",FACE,{"disambiguationData":[OSD([subQ0,subQ3,subQ2,subQ1])],"isStart":true})])],"derivedFrom":makeQuery(id+"F5.boolean.opBoolean","COPY",EDGE,{"derivedFrom":makeQuery(id+"F5.opExtrude","SWEPT_EDGE",EDGE,{"disambiguationData":[OSD([subQ0,subQ3])]})})});}
            var Q7;
            {var subQ0=sQuery(id+"F3.wireOp",EDGE,"E0.bottom");var subQ1=sQuery(id+"F3.wireOp",EDGE,"E3.top");var subQ2=sQuery(id+"F3.wireOp",EDGE,"E2.left");var subQ3=sQuery(id+"F3.wireOp",EDGE,"E0.right");Q7=makeQuery(id+"F12.boolean.opBoolean","SPLIT",EDGE,{"disambiguationData":[TD([makeQuery(id+"F12.opExtrude","CAP_FACE",FACE,{"disambiguationData":[OSD([subQ0,subQ3,subQ2,subQ1])],"isStart":true})])],"derivedFrom":makeQuery(id+"F5.boolean.opBoolean","COPY",EDGE,{"derivedFrom":makeQuery(id+"F5.opExtrude","SWEPT_EDGE",EDGE,{"disambiguationData":[OSD([subQ0,subQ3])]})})});}
            var Q8;
            {var subQ0=sQuery(id+"F3.wireOp",EDGE,"E3.bottom");var subQ1=sQuery(id+"F3.wireOp",EDGE,"E2.right");var subQ2=sQuery(id+"F3.wireOp",EDGE,"E0.top");var subQ3=sQuery(id+"F3.wireOp",EDGE,"E0.left");Q8=makeQuery(id+"F12.boolean.opBoolean","SPLIT",EDGE,{"disambiguationData":[TD([makeQuery(id+"F12.opExtrude","CAP_FACE",FACE,{"disambiguationData":[OSD([subQ2,subQ3,subQ1,subQ0])],"isStart":false})])],"derivedFrom":makeQuery(id+"F5.boolean.opBoolean","COPY",EDGE,{"derivedFrom":makeQuery(id+"F5.opExtrude","SWEPT_EDGE",EDGE,{"disambiguationData":[OSD([subQ2,subQ3])]})})});}
            var Q9;
            {var subQ0=sQuery(id+"F3.wireOp",EDGE,"E3.bottom");var subQ1=sQuery(id+"F3.wireOp",EDGE,"E2.left");var subQ2=sQuery(id+"F3.wireOp",EDGE,"E0.top");var subQ3=sQuery(id+"F3.wireOp",EDGE,"E0.right");Q9=makeQuery(id+"F12.boolean.opBoolean","SPLIT",EDGE,{"disambiguationData":[TD([makeQuery(id+"F12.opExtrude","CAP_FACE",FACE,{"disambiguationData":[OSD([subQ2,subQ3,subQ1,subQ0])],"isStart":false})])],"derivedFrom":makeQuery(id+"F5.boolean.opBoolean","COPY",EDGE,{"derivedFrom":makeQuery(id+"F5.opExtrude","SWEPT_EDGE",EDGE,{"disambiguationData":[OSD([subQ2,subQ3])]})})});}
            chamfer(context, id + "F15", {"entities" : qUnion([Q0, Q1, Q2, Q3, Q4, Q5, Q6, Q7, Q8, Q9]), "width" : 3 * mm, "tangentPropagation" : true});
        }
        {
            var Q0;
            {var subQ0=sQuery(id+"F3.wireOp",EDGE,"E3.top");var subQ1=sQuery(id+"F3.wireOp",EDGE,"E2.right");var subQ2=sQuery(id+"F3.wireOp",EDGE,"E0.bottom");var subQ3=sQuery(id+"F3.wireOp",EDGE,"E0.left");Q0=makeQuery(id+"F12.boolean.opBoolean","SPLIT",EDGE,{"disambiguationData":[TD([makeQuery(id+"F12.opExtrude","CAP_FACE",FACE,{"disambiguationData":[OSD([subQ2,subQ3,subQ1,subQ0])],"isStart":false})])],"derivedFrom":makeQuery(id+"F5.boolean.opBoolean","COPY",EDGE,{"derivedFrom":makeQuery(id+"F5.opExtrude","SWEPT_EDGE",EDGE,{"disambiguationData":[OSD([subQ2,subQ3])]})})});}
            var Q1;
            {var subQ0=sQuery(id+"F3.wireOp",EDGE,"E3.top");var subQ1=sQuery(id+"F3.wireOp",EDGE,"E2.left");var subQ2=sQuery(id+"F3.wireOp",EDGE,"E0.bottom");var subQ3=sQuery(id+"F3.wireOp",EDGE,"E0.right");Q1=makeQuery(id+"F12.boolean.opBoolean","SPLIT",EDGE,{"disambiguationData":[TD([makeQuery(id+"F12.opExtrude","CAP_FACE",FACE,{"disambiguationData":[OSD([subQ2,subQ3,subQ1,subQ0])],"isStart":false})])],"derivedFrom":makeQuery(id+"F5.boolean.opBoolean","COPY",EDGE,{"derivedFrom":makeQuery(id+"F5.opExtrude","SWEPT_EDGE",EDGE,{"disambiguationData":[OSD([subQ2,subQ3])]})})});}
            fillet(context, id + "F16", {"entities" : qUnion([Q0, Q1]), "radius" : 3 * mm, "tangentPropagation" : true, "allowEdgeOverflow" : false});
        }
        {
            var Q0;
            Q0=qCreatedBy(makeId("Top.planeOp"),FACE);
            var sketch = newSketch(context, id + "F17", { "sketchPlane" : qUnion([Q0])});
            skLineSegment(sketch, "E137", {"start": v(0, 0) * mm, "end": v(-240, 0) * mm, "construction": true});
            skLineSegment(sketch, "E138.bottom", {"start": v(-272.8, 32.8) * mm, "end": v(-207.2, 32.8) * mm});
            skLineSegment(sketch, "E138.top", {"start": v(-272.8, -32.8) * mm, "end": v(-207.2, -32.8) * mm});
            skLineSegment(sketch, "E138.left", {"start": v(-272.8, 32.8) * mm, "end": v(-272.8, -32.8) * mm});
            skLineSegment(sketch, "E138.right", {"start": v(-207.2, 32.8) * mm, "end": v(-207.2, -32.8) * mm});
            skPoint(sketch, "E138.middle", {"position": v(-240, 0) * mm});
            skSolve(sketch);
        }
        {
            var Q0;
            Q0=qSketchRegion(id+"F17",true);
            extrude(context, id + "F18", {"entities" : qUnion([Q0]), "oppositeDirection" : true, "depth" : (getVariable(context, 'Grosor')) * mm});
        }
        {
            var Q0;
            Q0=qCreatedBy(makeId("Top.planeOp"),FACE);
            var sketch = newSketch(context, id + "F19", { "sketchPlane" : qUnion([Q0])});
            skLineSegment(sketch, "E139", {"start": v(0, 0) * mm, "end": v(-240, 0) * mm, "construction": true});
            skLineSegment(sketch, "E140.bottom", {"start": v(-269.75, 29.75) * mm, "end": v(-210.25, 29.75) * mm});
            skLineSegment(sketch, "E140.top", {"start": v(-269.75, -29.75) * mm, "end": v(-210.25, -29.75) * mm});
            skLineSegment(sketch, "E140.left", {"start": v(-269.75, 29.75) * mm, "end": v(-269.75, -29.75) * mm});
            skLineSegment(sketch, "E140.right", {"start": v(-210.25, 29.75) * mm, "end": v(-210.25, -29.75) * mm});
            skPoint(sketch, "E140.middle", {"position": v(-240, 0) * mm});
            skLineSegment(sketch, "E141.bottom", {"start": v(-267.2, 27.2) * mm, "end": v(-212.8, 27.2) * mm});
            skLineSegment(sketch, "E141.top", {"start": v(-267.2, -27.2) * mm, "end": v(-212.8, -27.2) * mm});
            skLineSegment(sketch, "E141.left", {"start": v(-267.2, 27.2) * mm, "end": v(-267.2, -27.2) * mm});
            skLineSegment(sketch, "E141.right", {"start": v(-212.8, 27.2) * mm, "end": v(-212.8, -27.2) * mm});
            skSolve(sketch);
        }
        {
            var Q0;
            Q0=qSketchRegion(id+"F19",true);
            extrude(context, id + "F20", {"entities" : qUnion([Q0]), "operationType" : NewBodyOperationType.ADD, "depth" : (getVariable(context, 'Grosor') + 1) * mm});
        }
        {
            var Q0;
            Q0=makeQuery(id+"F18.opExtrude","CAP_FACE",FACE,{"disambiguationData":[OSD([sQuery(id+"F17.wireOp",EDGE,"E138.bottom"),sQuery(id+"F17.wireOp",EDGE,"E138.top"),sQuery(id+"F17.wireOp",EDGE,"E138.left"),sQuery(id+"F17.wireOp",EDGE,"E138.right")])],"isStart":false});
            var Q1;
            Q1=makeQuery(id+"F18.opExtrude","SWEPT_EDGE",EDGE,{"disambiguationData":[OSD([sQuery(id+"F17.wireOp",EDGE,"E138.bottom"),sQuery(id+"F17.wireOp",EDGE,"E138.left")])]});
            var Q2;
            Q2=makeQuery(id+"F18.opExtrude","SWEPT_EDGE",EDGE,{"disambiguationData":[OSD([sQuery(id+"F17.wireOp",EDGE,"E138.bottom"),sQuery(id+"F17.wireOp",EDGE,"E138.right")])]});
            var Q3;
            Q3=makeQuery(id+"F18.opExtrude","SWEPT_EDGE",EDGE,{"disambiguationData":[OSD([sQuery(id+"F17.wireOp",EDGE,"E138.top"),sQuery(id+"F17.wireOp",EDGE,"E138.right")])]});
            var Q4;
            Q4=makeQuery(id+"F18.opExtrude","SWEPT_EDGE",EDGE,{"disambiguationData":[OSD([sQuery(id+"F17.wireOp",EDGE,"E138.top"),sQuery(id+"F17.wireOp",EDGE,"E138.left")])]});
            chamfer(context, id + "F21", {"entities" : qUnion([Q0, Q1, Q2, Q3, Q4]), "width" : 2.8 * mm, "tangentPropagation" : true});
        }
        {
            var Q0;
            Q0=makeQuery(id+"F20.opExtrude","SWEPT_EDGE",EDGE,{"disambiguationData":[OSD([sQuery(id+"F19.wireOp",EDGE,"E140.bottom"),sQuery(id+"F19.wireOp",EDGE,"E140.left")])]});
            var Q1;
            Q1=makeQuery(id+"F20.opExtrude","SWEPT_EDGE",EDGE,{"disambiguationData":[OSD([sQuery(id+"F19.wireOp",EDGE,"E141.bottom"),sQuery(id+"F19.wireOp",EDGE,"E141.left")])]});
            var Q2;
            Q2=makeQuery(id+"F20.opExtrude","SWEPT_EDGE",EDGE,{"disambiguationData":[OSD([sQuery(id+"F19.wireOp",EDGE,"E141.bottom"),sQuery(id+"F19.wireOp",EDGE,"E141.right")])]});
            var Q3;
            Q3=makeQuery(id+"F20.opExtrude","SWEPT_EDGE",EDGE,{"disambiguationData":[OSD([sQuery(id+"F19.wireOp",EDGE,"E140.bottom"),sQuery(id+"F19.wireOp",EDGE,"E140.right")])]});
            chamfer(context, id + "F22", {"entities" : qUnion([Q0, Q1, Q2, Q3]), "width" : 3 * mm, "tangentPropagation" : true});
        }
        {
            var Q0;
            Q0=makeQuery(id+"F20.opExtrude","SWEPT_EDGE",EDGE,{"disambiguationData":[OSD([sQuery(id+"F19.wireOp",EDGE,"E140.top"),sQuery(id+"F19.wireOp",EDGE,"E140.right")])]});
            var Q1;
            Q1=makeQuery(id+"F20.opExtrude","SWEPT_EDGE",EDGE,{"disambiguationData":[OSD([sQuery(id+"F19.wireOp",EDGE,"E140.top"),sQuery(id+"F19.wireOp",EDGE,"E140.left")])]});
            var Q2;
            Q2=makeQuery(id+"F20.opExtrude","SWEPT_EDGE",EDGE,{"disambiguationData":[OSD([sQuery(id+"F19.wireOp",EDGE,"E141.top"),sQuery(id+"F19.wireOp",EDGE,"E141.left")])]});
            var Q3;
            Q3=makeQuery(id+"F20.opExtrude","SWEPT_EDGE",EDGE,{"disambiguationData":[OSD([sQuery(id+"F19.wireOp",EDGE,"E141.top"),sQuery(id+"F19.wireOp",EDGE,"E141.right")])]});
            fillet(context, id + "F23", {"entities" : qUnion([Q0, Q1, Q2, Q3]), "radius" : 3 * mm, "tangentPropagation" : true, "allowEdgeOverflow" : false});
        }
        {
            var Q0;
            Q0=qCreatedBy(makeId("Top.planeOp"),FACE);
            var sketch = newSketch(context, id + "F24", { "sketchPlane" : qUnion([Q0])});
            skLineSegment(sketch, "E142", {"start": v(0, 0) * mm, "end": v(-240, 0) * mm, "construction": true});
            skLineSegment(sketch, "E143", {"start": v(-240, 0) * mm, "end": v(-240, -11.75) * mm, "construction": true});
            skLineSegment(sketch, "E144", {"start": v(-240, -11.75) * mm, "end": v(-251.75, -11.75) * mm, "construction": true});
            skLineSegment(sketch, "E145.bottom", {"start": v(-254.25, -4.25) * mm, "end": v(-249.25, -4.25) * mm});
            skLineSegment(sketch, "E145.top", {"start": v(-254.25, -19.25) * mm, "end": v(-249.25, -19.25) * mm});
            skLineSegment(sketch, "E145.left", {"start": v(-259.25, -9.25) * mm, "end": v(-259.25, -14.25) * mm});
            skLineSegment(sketch, "E145.right", {"start": v(-244.25, -9.25) * mm, "end": v(-244.25, -14.25) * mm});
            skPoint(sketch, "E145.middle", {"position": v(-251.75, -11.75) * mm});
            skPoint(sketch, "E146.visualSharp", {"position": v(-259.25, -4.25) * mm});
            skArc(sketch, "E146.filletArc", {"start": v(-254.25, -4.25) * mm, "mid": v(-257.79, -5.71) * mm, "end": v(-259.25, -9.25) * mm});
            skPoint(sketch, "E147.visualSharp", {"position": v(-244.25, -4.25) * mm});
            skArc(sketch, "E147.filletArc", {"start": v(-244.25, -9.25) * mm, "mid": v(-245.71, -5.71) * mm, "end": v(-249.25, -4.25) * mm});
            skPoint(sketch, "E148.visualSharp", {"position": v(-244.25, -19.25) * mm});
            skArc(sketch, "E148.filletArc", {"start": v(-249.25, -19.25) * mm, "mid": v(-245.71, -17.79) * mm, "end": v(-244.25, -14.25) * mm});
            skPoint(sketch, "E149.visualSharp", {"position": v(-259.25, -19.25) * mm});
            skArc(sketch, "E149.filletArc", {"start": v(-259.25, -14.25) * mm, "mid": v(-257.79, -17.79) * mm, "end": v(-254.25, -19.25) * mm});
            skArc(sketch, "E150.0.1.0", {"start": v(-254.25, 19.25) * mm, "mid": v(-257.79, 17.79) * mm, "end": v(-259.25, 14.25) * mm});
            skPoint(sketch, "E150.0.1.1", {"position": v(-244.25, 4.25) * mm});
            skPoint(sketch, "E150.0.1.2", {"position": v(-244.25, 19.25) * mm});
            skArc(sketch, "E150.0.1.3", {"start": v(-249.25, 4.25) * mm, "mid": v(-245.71, 5.71) * mm, "end": v(-244.25, 9.25) * mm});
            skArc(sketch, "E150.0.1.4", {"start": v(-244.25, 14.25) * mm, "mid": v(-245.71, 17.79) * mm, "end": v(-249.25, 19.25) * mm});
            skPoint(sketch, "E150.0.1.5", {"position": v(-251.75, 11.75) * mm});
            skPoint(sketch, "E150.0.1.6", {"position": v(-259.25, 19.25) * mm});
            skLineSegment(sketch, "E150.0.1.7", {"start": v(-259.25, 14.25) * mm, "end": v(-259.25, 9.25) * mm});
            skArc(sketch, "E150.0.1.8", {"start": v(-259.25, 9.25) * mm, "mid": v(-257.79, 5.71) * mm, "end": v(-254.25, 4.25) * mm});
            skPoint(sketch, "E150.0.1.9", {"position": v(-259.25, 4.25) * mm});
            skLineSegment(sketch, "E150.0.1.10", {"start": v(-244.25, 14.25) * mm, "end": v(-244.25, 9.25) * mm});
            skLineSegment(sketch, "E150.0.1.11", {"start": v(-254.25, 19.25) * mm, "end": v(-249.25, 19.25) * mm});
            skLineSegment(sketch, "E150.0.1.12", {"start": v(-254.25, 4.25) * mm, "end": v(-249.25, 4.25) * mm});
            skArc(sketch, "E150.0.2.0", {"start": v(-254.25, 42.75) * mm, "mid": v(-257.79, 41.29) * mm, "end": v(-259.25, 37.75) * mm});
            skPoint(sketch, "E150.0.2.1", {"position": v(-244.25, 27.75) * mm});
            skPoint(sketch, "E150.0.2.2", {"position": v(-244.25, 42.75) * mm});
            skArc(sketch, "E150.0.2.3", {"start": v(-249.25, 27.75) * mm, "mid": v(-245.71, 29.21) * mm, "end": v(-244.25, 32.75) * mm});
            skArc(sketch, "E150.0.2.4", {"start": v(-244.25, 37.75) * mm, "mid": v(-245.71, 41.29) * mm, "end": v(-249.25, 42.75) * mm});
            skPoint(sketch, "E150.0.2.5", {"position": v(-251.75, 35.25) * mm});
            skPoint(sketch, "E150.0.2.6", {"position": v(-259.25, 42.75) * mm});
            skLineSegment(sketch, "E150.0.2.7", {"start": v(-259.25, 37.75) * mm, "end": v(-259.25, 32.75) * mm});
            skArc(sketch, "E150.0.2.8", {"start": v(-259.25, 32.75) * mm, "mid": v(-257.79, 29.21) * mm, "end": v(-254.25, 27.75) * mm});
            skPoint(sketch, "E150.0.2.9", {"position": v(-259.25, 27.75) * mm});
            skLineSegment(sketch, "E150.0.2.10", {"start": v(-244.25, 37.75) * mm, "end": v(-244.25, 32.75) * mm});
            skLineSegment(sketch, "E150.0.2.11", {"start": v(-254.25, 42.75) * mm, "end": v(-249.25, 42.75) * mm});
            skLineSegment(sketch, "E150.0.2.12", {"start": v(-254.25, 27.75) * mm, "end": v(-249.25, 27.75) * mm});
            skArc(sketch, "E150.1.0.0", {"start": v(-230.75, -4.25) * mm, "mid": v(-234.29, -5.71) * mm, "end": v(-235.75, -9.25) * mm});
            skPoint(sketch, "E150.1.0.1", {"position": v(-220.75, -19.25) * mm});
            skPoint(sketch, "E150.1.0.2", {"position": v(-220.75, -4.25) * mm});
            skArc(sketch, "E150.1.0.3", {"start": v(-225.75, -19.25) * mm, "mid": v(-222.21, -17.79) * mm, "end": v(-220.75, -14.25) * mm});
            skArc(sketch, "E150.1.0.4", {"start": v(-220.75, -9.25) * mm, "mid": v(-222.21, -5.71) * mm, "end": v(-225.75, -4.25) * mm});
            skPoint(sketch, "E150.1.0.5", {"position": v(-228.25, -11.75) * mm});
            skPoint(sketch, "E150.1.0.6", {"position": v(-235.75, -4.25) * mm});
            skLineSegment(sketch, "E150.1.0.7", {"start": v(-235.75, -9.25) * mm, "end": v(-235.75, -14.25) * mm});
            skArc(sketch, "E150.1.0.8", {"start": v(-235.75, -14.25) * mm, "mid": v(-234.29, -17.79) * mm, "end": v(-230.75, -19.25) * mm});
            skPoint(sketch, "E150.1.0.9", {"position": v(-235.75, -19.25) * mm});
            skLineSegment(sketch, "E150.1.0.10", {"start": v(-220.75, -9.25) * mm, "end": v(-220.75, -14.25) * mm});
            skLineSegment(sketch, "E150.1.0.11", {"start": v(-230.75, -4.25) * mm, "end": v(-225.75, -4.25) * mm});
            skLineSegment(sketch, "E150.1.0.12", {"start": v(-230.75, -19.25) * mm, "end": v(-225.75, -19.25) * mm});
            skArc(sketch, "E150.1.1.0", {"start": v(-230.75, 19.25) * mm, "mid": v(-234.29, 17.79) * mm, "end": v(-235.75, 14.25) * mm});
            skPoint(sketch, "E150.1.1.1", {"position": v(-220.75, 4.25) * mm});
            skPoint(sketch, "E150.1.1.2", {"position": v(-220.75, 19.25) * mm});
            skArc(sketch, "E150.1.1.3", {"start": v(-225.75, 4.25) * mm, "mid": v(-222.21, 5.71) * mm, "end": v(-220.75, 9.25) * mm});
            skArc(sketch, "E150.1.1.4", {"start": v(-220.75, 14.25) * mm, "mid": v(-222.21, 17.79) * mm, "end": v(-225.75, 19.25) * mm});
            skPoint(sketch, "E150.1.1.5", {"position": v(-228.25, 11.75) * mm});
            skPoint(sketch, "E150.1.1.6", {"position": v(-235.75, 19.25) * mm});
            skLineSegment(sketch, "E150.1.1.7", {"start": v(-235.75, 14.25) * mm, "end": v(-235.75, 9.25) * mm});
            skArc(sketch, "E150.1.1.8", {"start": v(-235.75, 9.25) * mm, "mid": v(-234.29, 5.71) * mm, "end": v(-230.75, 4.25) * mm});
            skPoint(sketch, "E150.1.1.9", {"position": v(-235.75, 4.25) * mm});
            skLineSegment(sketch, "E150.1.1.10", {"start": v(-220.75, 14.25) * mm, "end": v(-220.75, 9.25) * mm});
            skLineSegment(sketch, "E150.1.1.11", {"start": v(-230.75, 19.25) * mm, "end": v(-225.75, 19.25) * mm});
            skLineSegment(sketch, "E150.1.1.12", {"start": v(-230.75, 4.25) * mm, "end": v(-225.75, 4.25) * mm});
            skArc(sketch, "E150.1.2.0", {"start": v(-230.75, 42.75) * mm, "mid": v(-234.29, 41.29) * mm, "end": v(-235.75, 37.75) * mm});
            skPoint(sketch, "E150.1.2.1", {"position": v(-220.75, 27.75) * mm});
            skPoint(sketch, "E150.1.2.2", {"position": v(-220.75, 42.75) * mm});
            skArc(sketch, "E150.1.2.3", {"start": v(-225.75, 27.75) * mm, "mid": v(-222.21, 29.21) * mm, "end": v(-220.75, 32.75) * mm});
            skArc(sketch, "E150.1.2.4", {"start": v(-220.75, 37.75) * mm, "mid": v(-222.21, 41.29) * mm, "end": v(-225.75, 42.75) * mm});
            skPoint(sketch, "E150.1.2.5", {"position": v(-228.25, 35.25) * mm});
            skPoint(sketch, "E150.1.2.6", {"position": v(-235.75, 42.75) * mm});
            skLineSegment(sketch, "E150.1.2.7", {"start": v(-235.75, 37.75) * mm, "end": v(-235.75, 32.75) * mm});
            skArc(sketch, "E150.1.2.8", {"start": v(-235.75, 32.75) * mm, "mid": v(-234.29, 29.21) * mm, "end": v(-230.75, 27.75) * mm});
            skPoint(sketch, "E150.1.2.9", {"position": v(-235.75, 27.75) * mm});
            skLineSegment(sketch, "E150.1.2.10", {"start": v(-220.75, 37.75) * mm, "end": v(-220.75, 32.75) * mm});
            skLineSegment(sketch, "E150.1.2.11", {"start": v(-230.75, 42.75) * mm, "end": v(-225.75, 42.75) * mm});
            skLineSegment(sketch, "E150.1.2.12", {"start": v(-230.75, 27.75) * mm, "end": v(-225.75, 27.75) * mm});
            skArc(sketch, "E150.2.0.0", {"start": v(-207.25, -4.25) * mm, "mid": v(-210.79, -5.71) * mm, "end": v(-212.25, -9.25) * mm});
            skPoint(sketch, "E150.2.0.1", {"position": v(-197.25, -19.25) * mm});
            skPoint(sketch, "E150.2.0.2", {"position": v(-197.25, -4.25) * mm});
            skArc(sketch, "E150.2.0.3", {"start": v(-202.25, -19.25) * mm, "mid": v(-198.71, -17.79) * mm, "end": v(-197.25, -14.25) * mm});
            skArc(sketch, "E150.2.0.4", {"start": v(-197.25, -9.25) * mm, "mid": v(-198.71, -5.71) * mm, "end": v(-202.25, -4.25) * mm});
            skPoint(sketch, "E150.2.0.5", {"position": v(-204.75, -11.75) * mm});
            skPoint(sketch, "E150.2.0.6", {"position": v(-212.25, -4.25) * mm});
            skLineSegment(sketch, "E150.2.0.7", {"start": v(-212.25, -9.25) * mm, "end": v(-212.25, -14.25) * mm});
            skArc(sketch, "E150.2.0.8", {"start": v(-212.25, -14.25) * mm, "mid": v(-210.79, -17.79) * mm, "end": v(-207.25, -19.25) * mm});
            skPoint(sketch, "E150.2.0.9", {"position": v(-212.25, -19.25) * mm});
            skLineSegment(sketch, "E150.2.0.10", {"start": v(-197.25, -9.25) * mm, "end": v(-197.25, -14.25) * mm});
            skLineSegment(sketch, "E150.2.0.11", {"start": v(-207.25, -4.25) * mm, "end": v(-202.25, -4.25) * mm});
            skLineSegment(sketch, "E150.2.0.12", {"start": v(-207.25, -19.25) * mm, "end": v(-202.25, -19.25) * mm});
            skArc(sketch, "E150.2.1.0", {"start": v(-207.25, 19.25) * mm, "mid": v(-210.79, 17.79) * mm, "end": v(-212.25, 14.25) * mm});
            skPoint(sketch, "E150.2.1.1", {"position": v(-197.25, 4.25) * mm});
            skPoint(sketch, "E150.2.1.2", {"position": v(-197.25, 19.25) * mm});
            skArc(sketch, "E150.2.1.3", {"start": v(-202.25, 4.25) * mm, "mid": v(-198.71, 5.71) * mm, "end": v(-197.25, 9.25) * mm});
            skArc(sketch, "E150.2.1.4", {"start": v(-197.25, 14.25) * mm, "mid": v(-198.71, 17.79) * mm, "end": v(-202.25, 19.25) * mm});
            skPoint(sketch, "E150.2.1.5", {"position": v(-204.75, 11.75) * mm});
            skPoint(sketch, "E150.2.1.6", {"position": v(-212.25, 19.25) * mm});
            skLineSegment(sketch, "E150.2.1.7", {"start": v(-212.25, 14.25) * mm, "end": v(-212.25, 9.25) * mm});
            skArc(sketch, "E150.2.1.8", {"start": v(-212.25, 9.25) * mm, "mid": v(-210.79, 5.71) * mm, "end": v(-207.25, 4.25) * mm});
            skPoint(sketch, "E150.2.1.9", {"position": v(-212.25, 4.25) * mm});
            skLineSegment(sketch, "E150.2.1.10", {"start": v(-197.25, 14.25) * mm, "end": v(-197.25, 9.25) * mm});
            skLineSegment(sketch, "E150.2.1.11", {"start": v(-207.25, 19.25) * mm, "end": v(-202.25, 19.25) * mm});
            skLineSegment(sketch, "E150.2.1.12", {"start": v(-207.25, 4.25) * mm, "end": v(-202.25, 4.25) * mm});
            skArc(sketch, "E150.2.2.0", {"start": v(-207.25, 42.75) * mm, "mid": v(-210.79, 41.29) * mm, "end": v(-212.25, 37.75) * mm});
            skPoint(sketch, "E150.2.2.1", {"position": v(-197.25, 27.75) * mm});
            skPoint(sketch, "E150.2.2.2", {"position": v(-197.25, 42.75) * mm});
            skArc(sketch, "E150.2.2.3", {"start": v(-202.25, 27.75) * mm, "mid": v(-198.71, 29.21) * mm, "end": v(-197.25, 32.75) * mm});
            skArc(sketch, "E150.2.2.4", {"start": v(-197.25, 37.75) * mm, "mid": v(-198.71, 41.29) * mm, "end": v(-202.25, 42.75) * mm});
            skPoint(sketch, "E150.2.2.5", {"position": v(-204.75, 35.25) * mm});
            skPoint(sketch, "E150.2.2.6", {"position": v(-212.25, 42.75) * mm});
            skLineSegment(sketch, "E150.2.2.7", {"start": v(-212.25, 37.75) * mm, "end": v(-212.25, 32.75) * mm});
            skArc(sketch, "E150.2.2.8", {"start": v(-212.25, 32.75) * mm, "mid": v(-210.79, 29.21) * mm, "end": v(-207.25, 27.75) * mm});
            skPoint(sketch, "E150.2.2.9", {"position": v(-212.25, 27.75) * mm});
            skLineSegment(sketch, "E150.2.2.10", {"start": v(-197.25, 37.75) * mm, "end": v(-197.25, 32.75) * mm});
            skLineSegment(sketch, "E150.2.2.11", {"start": v(-207.25, 42.75) * mm, "end": v(-202.25, 42.75) * mm});
            skLineSegment(sketch, "E150.2.2.12", {"start": v(-207.25, 27.75) * mm, "end": v(-202.25, 27.75) * mm});
            skLineSegment(sketch, "E150.direction1", {"start": v(-259.25, -19.25) * mm, "end": v(-235.75, -19.25) * mm, "construction": true});
            skLineSegment(sketch, "E150.direction2", {"start": v(-259.25, -19.25) * mm, "end": v(-259.25, 4.25) * mm, "construction": true});
            skSolve(sketch);
        }
        {
            var Q0;
            Q0=makeQuery(id+"F24.imprint","IMPRINT",FACE,{"disambiguationData":[TD([[makeQuery(id+"F24.imprint","IMPRINT",EDGE,{"derivedFrom":sQuery(id+"F24.wireOp",EDGE,"E150.0.1.0")}),1.0]])]});
            var Q1;
            Q1=makeQuery(id+"F24.imprint","IMPRINT",FACE,{"disambiguationData":[TD([[makeQuery(id+"F24.imprint","IMPRINT",EDGE,{"derivedFrom":sQuery(id+"F24.wireOp",EDGE,"E150.1.1.0")}),1.0]])]});
            var Q2;
            Q2=makeQuery(id+"F24.imprint","IMPRINT",FACE,{"disambiguationData":[TD([[makeQuery(id+"F24.imprint","IMPRINT",EDGE,{"derivedFrom":sQuery(id+"F24.wireOp",EDGE,"E150.1.0.0")}),1.0]])]});
            var Q3;
            Q3=makeQuery(id+"F24.imprint","IMPRINT",FACE,{"disambiguationData":[TD([[makeQuery(id+"F24.imprint","IMPRINT",EDGE,{"derivedFrom":sQuery(id+"F24.wireOp",EDGE,"E145.bottom")}),-1.0]])]});
            extrude(context, id + "F25", {"entities" : qUnion([Q0, Q1, Q2, Q3]), "operationType" : NewBodyOperationType.REMOVE, "endBound" : BoundingType.THROUGH_ALL, "oppositeDirection" : true, "depth" : 25 * mm});
        }
        {
            var Q0;
            Q0=qCreatedBy(makeId("Top.planeOp"),FACE);
            var sketch = newSketch(context, id + "F26", { "sketchPlane" : qUnion([Q0])});
            skLineSegment(sketch, "E151", {"start": v(0, 0) * mm, "end": v(120, 0) * mm, "construction": true});
            skLineSegment(sketch, "E152.bottom", {"start": v(120, 0) * mm, "end": v(179, 0) * mm});
            skLineSegment(sketch, "E152.top", {"start": v(120, 59) * mm, "end": v(179, 59) * mm});
            skLineSegment(sketch, "E152.left", {"start": v(120, 0) * mm, "end": v(120, 59) * mm});
            skLineSegment(sketch, "E152.right", {"start": v(179, 0) * mm, "end": v(179, 59) * mm});
            skSolve(sketch);
        }
        {
            var Q0;
            Q0=qSketchRegion(id+"F26",true);
            extrude(context, id + "F27", {"entities" : qUnion([Q0]), "oppositeDirection" : true, "depth" : (getVariable(context, 'Grosor') / 2) * mm, "hasSecondDirection" : true, "secondDirectionOppositeDirection" : false, "secondDirectionDepth" : 3.5 * mm});
        }
        {
            var Q0;
            Q0=qCreatedBy(makeId("Top.planeOp"),FACE);
            var sketch = newSketch(context, id + "F28", { "sketchPlane" : qUnion([Q0])});
            skLineSegment(sketch, "E153", {"start": v(0, 0) * mm, "end": v(120, 0) * mm, "construction": true});
            skLineSegment(sketch, "E154", {"start": v(120, 0) * mm, "end": v(126, 0) * mm, "construction": true});
            skLineSegment(sketch, "E155", {"start": v(126, 0) * mm, "end": v(126, 6) * mm, "construction": true});
            skLineSegment(sketch, "E156", {"start": v(126, 6) * mm, "end": v(137.75, 6) * mm, "construction": true});
            skLineSegment(sketch, "E157", {"start": v(126, 6) * mm, "end": v(126, 17.75) * mm, "construction": true});
            skLineSegment(sketch, "E158.bottom", {"start": v(136.25, 7.5) * mm, "end": v(139.25, 7.5) * mm});
            skLineSegment(sketch, "E158.top", {"start": v(136.25, 4.5) * mm, "end": v(139.25, 4.5) * mm});
            skLineSegment(sketch, "E158.left", {"start": v(136.25, 7.5) * mm, "end": v(136.25, 4.5) * mm});
            skLineSegment(sketch, "E158.right", {"start": v(139.25, 7.5) * mm, "end": v(139.25, 4.5) * mm});
            skPoint(sketch, "E158.middle", {"position": v(137.75, 6) * mm});
            skLineSegment(sketch, "E159.bottom", {"start": v(124.5, 19.25) * mm, "end": v(127.5, 19.25) * mm});
            skLineSegment(sketch, "E159.top", {"start": v(124.5, 16.25) * mm, "end": v(127.5, 16.25) * mm});
            skLineSegment(sketch, "E159.left", {"start": v(124.5, 19.25) * mm, "end": v(124.5, 16.25) * mm});
            skLineSegment(sketch, "E159.right", {"start": v(127.5, 19.25) * mm, "end": v(127.5, 16.25) * mm});
            skPoint(sketch, "E159.middle", {"position": v(126, 17.75) * mm});
            skLineSegment(sketch, "E160.bottom", {"start": v(120, 0) * mm, "end": v(179, 0) * mm});
            skLineSegment(sketch, "E160.top", {"start": v(120, 59) * mm, "end": v(179, 59) * mm});
            skLineSegment(sketch, "E160.left", {"start": v(120, 0) * mm, "end": v(120, 59) * mm});
            skLineSegment(sketch, "E160.right", {"start": v(179, 0) * mm, "end": v(179, 59) * mm});
            skPoint(sketch, "E161.0.1.0", {"position": v(137.75, 29.5) * mm});
            skPoint(sketch, "E161.0.1.1", {"position": v(126, 41.25) * mm});
            skLineSegment(sketch, "E161.0.1.2", {"start": v(124.5, 42.75) * mm, "end": v(127.5, 42.75) * mm});
            skLineSegment(sketch, "E161.0.1.3", {"start": v(136.25, 31) * mm, "end": v(139.25, 31) * mm});
            skLineSegment(sketch, "E161.0.1.4", {"start": v(139.25, 31) * mm, "end": v(139.25, 28) * mm});
            skLineSegment(sketch, "E161.0.1.5", {"start": v(136.25, 31) * mm, "end": v(136.25, 28) * mm});
            skLineSegment(sketch, "E161.0.1.6", {"start": v(136.25, 28) * mm, "end": v(139.25, 28) * mm});
            skLineSegment(sketch, "E161.0.1.7", {"start": v(124.5, 42.75) * mm, "end": v(124.5, 39.75) * mm});
            skLineSegment(sketch, "E161.0.1.8", {"start": v(127.5, 42.75) * mm, "end": v(127.5, 39.75) * mm});
            skLineSegment(sketch, "E161.0.1.9", {"start": v(124.5, 39.75) * mm, "end": v(127.5, 39.75) * mm});
            skPoint(sketch, "E161.0.2.0", {"position": v(137.75, 53) * mm});
            skPoint(sketch, "E161.0.2.1", {"position": v(126, 64.75) * mm});
            skLineSegment(sketch, "E161.0.2.2", {"start": v(124.5, 66.25) * mm, "end": v(127.5, 66.25) * mm});
            skLineSegment(sketch, "E161.0.2.3", {"start": v(136.25, 54.5) * mm, "end": v(139.25, 54.5) * mm});
            skLineSegment(sketch, "E161.0.2.4", {"start": v(139.25, 54.5) * mm, "end": v(139.25, 51.5) * mm});
            skLineSegment(sketch, "E161.0.2.5", {"start": v(136.25, 54.5) * mm, "end": v(136.25, 51.5) * mm});
            skLineSegment(sketch, "E161.0.2.6", {"start": v(136.25, 51.5) * mm, "end": v(139.25, 51.5) * mm});
            skLineSegment(sketch, "E161.0.2.7", {"start": v(124.5, 66.25) * mm, "end": v(124.5, 63.25) * mm});
            skLineSegment(sketch, "E161.0.2.8", {"start": v(127.5, 66.25) * mm, "end": v(127.5, 63.25) * mm});
            skLineSegment(sketch, "E161.0.2.9", {"start": v(124.5, 63.25) * mm, "end": v(127.5, 63.25) * mm});
            skPoint(sketch, "E161.0.3.0", {"position": v(137.75, 76.5) * mm});
            skPoint(sketch, "E161.0.3.1", {"position": v(126, 88.25) * mm});
            skLineSegment(sketch, "E161.0.3.2", {"start": v(124.5, 89.75) * mm, "end": v(127.5, 89.75) * mm});
            skLineSegment(sketch, "E161.0.3.3", {"start": v(136.25, 78) * mm, "end": v(139.25, 78) * mm});
            skLineSegment(sketch, "E161.0.3.4", {"start": v(139.25, 78) * mm, "end": v(139.25, 75) * mm});
            skLineSegment(sketch, "E161.0.3.5", {"start": v(136.25, 78) * mm, "end": v(136.25, 75) * mm});
            skLineSegment(sketch, "E161.0.3.6", {"start": v(136.25, 75) * mm, "end": v(139.25, 75) * mm});
            skLineSegment(sketch, "E161.0.3.7", {"start": v(124.5, 89.75) * mm, "end": v(124.5, 86.75) * mm});
            skLineSegment(sketch, "E161.0.3.8", {"start": v(127.5, 89.75) * mm, "end": v(127.5, 86.75) * mm});
            skLineSegment(sketch, "E161.0.3.9", {"start": v(124.5, 86.75) * mm, "end": v(127.5, 86.75) * mm});
            skPoint(sketch, "E161.0.4.0", {"position": v(137.75, 100) * mm});
            skPoint(sketch, "E161.0.4.1", {"position": v(126, 111.75) * mm});
            skLineSegment(sketch, "E161.0.4.2", {"start": v(124.5, 113.25) * mm, "end": v(127.5, 113.25) * mm});
            skLineSegment(sketch, "E161.0.4.3", {"start": v(136.25, 101.5) * mm, "end": v(139.25, 101.5) * mm});
            skLineSegment(sketch, "E161.0.4.4", {"start": v(139.25, 101.5) * mm, "end": v(139.25, 98.5) * mm});
            skLineSegment(sketch, "E161.0.4.5", {"start": v(136.25, 101.5) * mm, "end": v(136.25, 98.5) * mm});
            skLineSegment(sketch, "E161.0.4.6", {"start": v(136.25, 98.5) * mm, "end": v(139.25, 98.5) * mm});
            skLineSegment(sketch, "E161.0.4.7", {"start": v(124.5, 113.25) * mm, "end": v(124.5, 110.25) * mm});
            skLineSegment(sketch, "E161.0.4.8", {"start": v(127.5, 113.25) * mm, "end": v(127.5, 110.25) * mm});
            skLineSegment(sketch, "E161.0.4.9", {"start": v(124.5, 110.25) * mm, "end": v(127.5, 110.25) * mm});
            skPoint(sketch, "E161.1.0.0", {"position": v(161.25, 6) * mm});
            skPoint(sketch, "E161.1.0.1", {"position": v(149.5, 17.75) * mm});
            skLineSegment(sketch, "E161.1.0.2", {"start": v(148, 19.25) * mm, "end": v(151, 19.25) * mm});
            skLineSegment(sketch, "E161.1.0.3", {"start": v(159.75, 7.5) * mm, "end": v(162.75, 7.5) * mm});
            skLineSegment(sketch, "E161.1.0.4", {"start": v(162.75, 7.5) * mm, "end": v(162.75, 4.5) * mm});
            skLineSegment(sketch, "E161.1.0.5", {"start": v(159.75, 7.5) * mm, "end": v(159.75, 4.5) * mm});
            skLineSegment(sketch, "E161.1.0.6", {"start": v(159.75, 4.5) * mm, "end": v(162.75, 4.5) * mm});
            skLineSegment(sketch, "E161.1.0.7", {"start": v(148, 19.25) * mm, "end": v(148, 16.25) * mm});
            skLineSegment(sketch, "E161.1.0.8", {"start": v(151, 19.25) * mm, "end": v(151, 16.25) * mm});
            skLineSegment(sketch, "E161.1.0.9", {"start": v(148, 16.25) * mm, "end": v(151, 16.25) * mm});
            skPoint(sketch, "E161.1.1.0", {"position": v(161.25, 29.5) * mm});
            skPoint(sketch, "E161.1.1.1", {"position": v(149.5, 41.25) * mm});
            skLineSegment(sketch, "E161.1.1.2", {"start": v(148, 42.75) * mm, "end": v(151, 42.75) * mm});
            skLineSegment(sketch, "E161.1.1.3", {"start": v(159.75, 31) * mm, "end": v(162.75, 31) * mm});
            skLineSegment(sketch, "E161.1.1.4", {"start": v(162.75, 31) * mm, "end": v(162.75, 28) * mm});
            skLineSegment(sketch, "E161.1.1.5", {"start": v(159.75, 31) * mm, "end": v(159.75, 28) * mm});
            skLineSegment(sketch, "E161.1.1.6", {"start": v(159.75, 28) * mm, "end": v(162.75, 28) * mm});
            skLineSegment(sketch, "E161.1.1.7", {"start": v(148, 42.75) * mm, "end": v(148, 39.75) * mm});
            skLineSegment(sketch, "E161.1.1.8", {"start": v(151, 42.75) * mm, "end": v(151, 39.75) * mm});
            skLineSegment(sketch, "E161.1.1.9", {"start": v(148, 39.75) * mm, "end": v(151, 39.75) * mm});
            skPoint(sketch, "E161.1.2.0", {"position": v(161.25, 53) * mm});
            skPoint(sketch, "E161.1.2.1", {"position": v(149.5, 64.75) * mm});
            skLineSegment(sketch, "E161.1.2.2", {"start": v(148, 66.25) * mm, "end": v(151, 66.25) * mm});
            skLineSegment(sketch, "E161.1.2.3", {"start": v(159.75, 54.5) * mm, "end": v(162.75, 54.5) * mm});
            skLineSegment(sketch, "E161.1.2.4", {"start": v(162.75, 54.5) * mm, "end": v(162.75, 51.5) * mm});
            skLineSegment(sketch, "E161.1.2.5", {"start": v(159.75, 54.5) * mm, "end": v(159.75, 51.5) * mm});
            skLineSegment(sketch, "E161.1.2.6", {"start": v(159.75, 51.5) * mm, "end": v(162.75, 51.5) * mm});
            skLineSegment(sketch, "E161.1.2.7", {"start": v(148, 66.25) * mm, "end": v(148, 63.25) * mm});
            skLineSegment(sketch, "E161.1.2.8", {"start": v(151, 66.25) * mm, "end": v(151, 63.25) * mm});
            skLineSegment(sketch, "E161.1.2.9", {"start": v(148, 63.25) * mm, "end": v(151, 63.25) * mm});
            skPoint(sketch, "E161.1.3.0", {"position": v(161.25, 76.5) * mm});
            skPoint(sketch, "E161.1.3.1", {"position": v(149.5, 88.25) * mm});
            skLineSegment(sketch, "E161.1.3.2", {"start": v(148, 89.75) * mm, "end": v(151, 89.75) * mm});
            skLineSegment(sketch, "E161.1.3.3", {"start": v(159.75, 78) * mm, "end": v(162.75, 78) * mm});
            skLineSegment(sketch, "E161.1.3.4", {"start": v(162.75, 78) * mm, "end": v(162.75, 75) * mm});
            skLineSegment(sketch, "E161.1.3.5", {"start": v(159.75, 78) * mm, "end": v(159.75, 75) * mm});
            skLineSegment(sketch, "E161.1.3.6", {"start": v(159.75, 75) * mm, "end": v(162.75, 75) * mm});
            skLineSegment(sketch, "E161.1.3.7", {"start": v(148, 89.75) * mm, "end": v(148, 86.75) * mm});
            skLineSegment(sketch, "E161.1.3.8", {"start": v(151, 89.75) * mm, "end": v(151, 86.75) * mm});
            skLineSegment(sketch, "E161.1.3.9", {"start": v(148, 86.75) * mm, "end": v(151, 86.75) * mm});
            skPoint(sketch, "E161.1.4.0", {"position": v(161.25, 100) * mm});
            skPoint(sketch, "E161.1.4.1", {"position": v(149.5, 111.75) * mm});
            skLineSegment(sketch, "E161.1.4.2", {"start": v(148, 113.25) * mm, "end": v(151, 113.25) * mm});
            skLineSegment(sketch, "E161.1.4.3", {"start": v(159.75, 101.5) * mm, "end": v(162.75, 101.5) * mm});
            skLineSegment(sketch, "E161.1.4.4", {"start": v(162.75, 101.5) * mm, "end": v(162.75, 98.5) * mm});
            skLineSegment(sketch, "E161.1.4.5", {"start": v(159.75, 101.5) * mm, "end": v(159.75, 98.5) * mm});
            skLineSegment(sketch, "E161.1.4.6", {"start": v(159.75, 98.5) * mm, "end": v(162.75, 98.5) * mm});
            skLineSegment(sketch, "E161.1.4.7", {"start": v(148, 113.25) * mm, "end": v(148, 110.25) * mm});
            skLineSegment(sketch, "E161.1.4.8", {"start": v(151, 113.25) * mm, "end": v(151, 110.25) * mm});
            skLineSegment(sketch, "E161.1.4.9", {"start": v(148, 110.25) * mm, "end": v(151, 110.25) * mm});
            skPoint(sketch, "E161.2.0.0", {"position": v(184.75, 6) * mm});
            skPoint(sketch, "E161.2.0.1", {"position": v(173, 17.75) * mm});
            skLineSegment(sketch, "E161.2.0.2", {"start": v(171.5, 19.25) * mm, "end": v(174.5, 19.25) * mm});
            skLineSegment(sketch, "E161.2.0.3", {"start": v(183.25, 7.5) * mm, "end": v(186.25, 7.5) * mm});
            skLineSegment(sketch, "E161.2.0.4", {"start": v(186.25, 7.5) * mm, "end": v(186.25, 4.5) * mm});
            skLineSegment(sketch, "E161.2.0.5", {"start": v(183.25, 7.5) * mm, "end": v(183.25, 4.5) * mm});
            skLineSegment(sketch, "E161.2.0.6", {"start": v(183.25, 4.5) * mm, "end": v(186.25, 4.5) * mm});
            skLineSegment(sketch, "E161.2.0.7", {"start": v(171.5, 19.25) * mm, "end": v(171.5, 16.25) * mm});
            skLineSegment(sketch, "E161.2.0.8", {"start": v(174.5, 19.25) * mm, "end": v(174.5, 16.25) * mm});
            skLineSegment(sketch, "E161.2.0.9", {"start": v(171.5, 16.25) * mm, "end": v(174.5, 16.25) * mm});
            skPoint(sketch, "E161.2.1.0", {"position": v(184.75, 29.5) * mm});
            skPoint(sketch, "E161.2.1.1", {"position": v(173, 41.25) * mm});
            skLineSegment(sketch, "E161.2.1.2", {"start": v(171.5, 42.75) * mm, "end": v(174.5, 42.75) * mm});
            skLineSegment(sketch, "E161.2.1.3", {"start": v(183.25, 31) * mm, "end": v(186.25, 31) * mm});
            skLineSegment(sketch, "E161.2.1.4", {"start": v(186.25, 31) * mm, "end": v(186.25, 28) * mm});
            skLineSegment(sketch, "E161.2.1.5", {"start": v(183.25, 31) * mm, "end": v(183.25, 28) * mm});
            skLineSegment(sketch, "E161.2.1.6", {"start": v(183.25, 28) * mm, "end": v(186.25, 28) * mm});
            skLineSegment(sketch, "E161.2.1.7", {"start": v(171.5, 42.75) * mm, "end": v(171.5, 39.75) * mm});
            skLineSegment(sketch, "E161.2.1.8", {"start": v(174.5, 42.75) * mm, "end": v(174.5, 39.75) * mm});
            skLineSegment(sketch, "E161.2.1.9", {"start": v(171.5, 39.75) * mm, "end": v(174.5, 39.75) * mm});
            skPoint(sketch, "E161.2.2.0", {"position": v(184.75, 53) * mm});
            skPoint(sketch, "E161.2.2.1", {"position": v(173, 64.75) * mm});
            skLineSegment(sketch, "E161.2.2.2", {"start": v(171.5, 66.25) * mm, "end": v(174.5, 66.25) * mm});
            skLineSegment(sketch, "E161.2.2.3", {"start": v(183.25, 54.5) * mm, "end": v(186.25, 54.5) * mm});
            skLineSegment(sketch, "E161.2.2.4", {"start": v(186.25, 54.5) * mm, "end": v(186.25, 51.5) * mm});
            skLineSegment(sketch, "E161.2.2.5", {"start": v(183.25, 54.5) * mm, "end": v(183.25, 51.5) * mm});
            skLineSegment(sketch, "E161.2.2.6", {"start": v(183.25, 51.5) * mm, "end": v(186.25, 51.5) * mm});
            skLineSegment(sketch, "E161.2.2.7", {"start": v(171.5, 66.25) * mm, "end": v(171.5, 63.25) * mm});
            skLineSegment(sketch, "E161.2.2.8", {"start": v(174.5, 66.25) * mm, "end": v(174.5, 63.25) * mm});
            skLineSegment(sketch, "E161.2.2.9", {"start": v(171.5, 63.25) * mm, "end": v(174.5, 63.25) * mm});
            skPoint(sketch, "E161.2.3.0", {"position": v(184.75, 76.5) * mm});
            skPoint(sketch, "E161.2.3.1", {"position": v(173, 88.25) * mm});
            skLineSegment(sketch, "E161.2.3.2", {"start": v(171.5, 89.75) * mm, "end": v(174.5, 89.75) * mm});
            skLineSegment(sketch, "E161.2.3.3", {"start": v(183.25, 78) * mm, "end": v(186.25, 78) * mm});
            skLineSegment(sketch, "E161.2.3.4", {"start": v(186.25, 78) * mm, "end": v(186.25, 75) * mm});
            skLineSegment(sketch, "E161.2.3.5", {"start": v(183.25, 78) * mm, "end": v(183.25, 75) * mm});
            skLineSegment(sketch, "E161.2.3.6", {"start": v(183.25, 75) * mm, "end": v(186.25, 75) * mm});
            skLineSegment(sketch, "E161.2.3.7", {"start": v(171.5, 89.75) * mm, "end": v(171.5, 86.75) * mm});
            skLineSegment(sketch, "E161.2.3.8", {"start": v(174.5, 89.75) * mm, "end": v(174.5, 86.75) * mm});
            skLineSegment(sketch, "E161.2.3.9", {"start": v(171.5, 86.75) * mm, "end": v(174.5, 86.75) * mm});
            skPoint(sketch, "E161.2.4.0", {"position": v(184.75, 100) * mm});
            skPoint(sketch, "E161.2.4.1", {"position": v(173, 111.75) * mm});
            skLineSegment(sketch, "E161.2.4.2", {"start": v(171.5, 113.25) * mm, "end": v(174.5, 113.25) * mm});
            skLineSegment(sketch, "E161.2.4.3", {"start": v(183.25, 101.5) * mm, "end": v(186.25, 101.5) * mm});
            skLineSegment(sketch, "E161.2.4.4", {"start": v(186.25, 101.5) * mm, "end": v(186.25, 98.5) * mm});
            skLineSegment(sketch, "E161.2.4.5", {"start": v(183.25, 101.5) * mm, "end": v(183.25, 98.5) * mm});
            skLineSegment(sketch, "E161.2.4.6", {"start": v(183.25, 98.5) * mm, "end": v(186.25, 98.5) * mm});
            skLineSegment(sketch, "E161.2.4.7", {"start": v(171.5, 113.25) * mm, "end": v(171.5, 110.25) * mm});
            skLineSegment(sketch, "E161.2.4.8", {"start": v(174.5, 113.25) * mm, "end": v(174.5, 110.25) * mm});
            skLineSegment(sketch, "E161.2.4.9", {"start": v(171.5, 110.25) * mm, "end": v(174.5, 110.25) * mm});
            skLineSegment(sketch, "E161.direction1", {"start": v(136.25, 4.5) * mm, "end": v(159.75, 4.5) * mm, "construction": true});
            skLineSegment(sketch, "E161.direction2", {"start": v(136.25, 4.5) * mm, "end": v(136.25, 28) * mm, "construction": true});
            skPoint(sketch, "E162.0.3.0", {"position": v(208.25, 6) * mm});
            skPoint(sketch, "E162.1.3.0", {"position": v(196.5, 17.75) * mm});
            skLineSegment(sketch, "E162.2.3.0", {"start": v(195, 19.25) * mm, "end": v(198, 19.25) * mm});
            skLineSegment(sketch, "E162.5.3.0", {"start": v(206.75, 7.5) * mm, "end": v(209.75, 7.5) * mm});
            skLineSegment(sketch, "E162.8.3.0", {"start": v(209.75, 7.5) * mm, "end": v(209.75, 4.5) * mm});
            skLineSegment(sketch, "E162.11.3.0", {"start": v(206.75, 7.5) * mm, "end": v(206.75, 4.5) * mm});
            skLineSegment(sketch, "E162.14.3.0", {"start": v(206.75, 4.5) * mm, "end": v(209.75, 4.5) * mm});
            skLineSegment(sketch, "E162.17.3.0", {"start": v(195, 19.25) * mm, "end": v(195, 16.25) * mm});
            skLineSegment(sketch, "E162.20.3.0", {"start": v(198, 19.25) * mm, "end": v(198, 16.25) * mm});
            skLineSegment(sketch, "E162.23.3.0", {"start": v(195, 16.25) * mm, "end": v(198, 16.25) * mm});
            skPoint(sketch, "E162.0.3.1", {"position": v(208.25, 29.5) * mm});
            skPoint(sketch, "E162.1.3.1", {"position": v(196.5, 41.25) * mm});
            skLineSegment(sketch, "E162.2.3.1", {"start": v(195, 42.75) * mm, "end": v(198, 42.75) * mm});
            skLineSegment(sketch, "E162.5.3.1", {"start": v(206.75, 31) * mm, "end": v(209.75, 31) * mm});
            skLineSegment(sketch, "E162.8.3.1", {"start": v(209.75, 31) * mm, "end": v(209.75, 28) * mm});
            skLineSegment(sketch, "E162.11.3.1", {"start": v(206.75, 31) * mm, "end": v(206.75, 28) * mm});
            skLineSegment(sketch, "E162.14.3.1", {"start": v(206.75, 28) * mm, "end": v(209.75, 28) * mm});
            skLineSegment(sketch, "E162.17.3.1", {"start": v(195, 42.75) * mm, "end": v(195, 39.75) * mm});
            skLineSegment(sketch, "E162.20.3.1", {"start": v(198, 42.75) * mm, "end": v(198, 39.75) * mm});
            skLineSegment(sketch, "E162.23.3.1", {"start": v(195, 39.75) * mm, "end": v(198, 39.75) * mm});
            skPoint(sketch, "E162.0.3.2", {"position": v(208.25, 53) * mm});
            skPoint(sketch, "E162.1.3.2", {"position": v(196.5, 64.75) * mm});
            skLineSegment(sketch, "E162.2.3.2", {"start": v(195, 66.25) * mm, "end": v(198, 66.25) * mm});
            skLineSegment(sketch, "E162.5.3.2", {"start": v(206.75, 54.5) * mm, "end": v(209.75, 54.5) * mm});
            skLineSegment(sketch, "E162.8.3.2", {"start": v(209.75, 54.5) * mm, "end": v(209.75, 51.5) * mm});
            skLineSegment(sketch, "E162.11.3.2", {"start": v(206.75, 54.5) * mm, "end": v(206.75, 51.5) * mm});
            skLineSegment(sketch, "E162.14.3.2", {"start": v(206.75, 51.5) * mm, "end": v(209.75, 51.5) * mm});
            skLineSegment(sketch, "E162.17.3.2", {"start": v(195, 66.25) * mm, "end": v(195, 63.25) * mm});
            skLineSegment(sketch, "E162.20.3.2", {"start": v(198, 66.25) * mm, "end": v(198, 63.25) * mm});
            skLineSegment(sketch, "E162.23.3.2", {"start": v(195, 63.25) * mm, "end": v(198, 63.25) * mm});
            skPoint(sketch, "E162.0.3.3", {"position": v(208.25, 76.5) * mm});
            skPoint(sketch, "E162.1.3.3", {"position": v(196.5, 88.25) * mm});
            skLineSegment(sketch, "E162.2.3.3", {"start": v(195, 89.75) * mm, "end": v(198, 89.75) * mm});
            skLineSegment(sketch, "E162.5.3.3", {"start": v(206.75, 78) * mm, "end": v(209.75, 78) * mm});
            skLineSegment(sketch, "E162.8.3.3", {"start": v(209.75, 78) * mm, "end": v(209.75, 75) * mm});
            skLineSegment(sketch, "E162.11.3.3", {"start": v(206.75, 78) * mm, "end": v(206.75, 75) * mm});
            skLineSegment(sketch, "E162.14.3.3", {"start": v(206.75, 75) * mm, "end": v(209.75, 75) * mm});
            skLineSegment(sketch, "E162.17.3.3", {"start": v(195, 89.75) * mm, "end": v(195, 86.75) * mm});
            skLineSegment(sketch, "E162.20.3.3", {"start": v(198, 89.75) * mm, "end": v(198, 86.75) * mm});
            skLineSegment(sketch, "E162.23.3.3", {"start": v(195, 86.75) * mm, "end": v(198, 86.75) * mm});
            skPoint(sketch, "E162.0.3.4", {"position": v(208.25, 100) * mm});
            skPoint(sketch, "E162.1.3.4", {"position": v(196.5, 111.75) * mm});
            skLineSegment(sketch, "E162.2.3.4", {"start": v(195, 113.25) * mm, "end": v(198, 113.25) * mm});
            skLineSegment(sketch, "E162.5.3.4", {"start": v(206.75, 101.5) * mm, "end": v(209.75, 101.5) * mm});
            skLineSegment(sketch, "E162.8.3.4", {"start": v(209.75, 101.5) * mm, "end": v(209.75, 98.5) * mm});
            skLineSegment(sketch, "E162.11.3.4", {"start": v(206.75, 101.5) * mm, "end": v(206.75, 98.5) * mm});
            skLineSegment(sketch, "E162.14.3.4", {"start": v(206.75, 98.5) * mm, "end": v(209.75, 98.5) * mm});
            skLineSegment(sketch, "E162.17.3.4", {"start": v(195, 113.25) * mm, "end": v(195, 110.25) * mm});
            skLineSegment(sketch, "E162.20.3.4", {"start": v(198, 113.25) * mm, "end": v(198, 110.25) * mm});
            skLineSegment(sketch, "E162.23.3.4", {"start": v(195, 110.25) * mm, "end": v(198, 110.25) * mm});
            skSolve(sketch);
        }
        {
            var Q0;
            Q0=qSketchRegion(id+"F28",true);
            extrude(context, id + "F29", {"entities" : qUnion([Q0]), "operationType" : NewBodyOperationType.REMOVE, "depth" : 25 * mm});
        }
        {
            var Q0;
            Q0=qCreatedBy(makeId("Top.planeOp"),FACE);
            var sketch = newSketch(context, id + "F30", { "sketchPlane" : qUnion([Q0])});
            skLineSegment(sketch, "E163", {"start": v(0, 0) * mm, "end": v(120, 0) * mm, "construction": true});
            skLineSegment(sketch, "E164", {"start": v(120, 0) * mm, "end": v(126, 0) * mm, "construction": true});
            skLineSegment(sketch, "E165", {"start": v(126, 0) * mm, "end": v(126, 6) * mm, "construction": true});
            skLineSegment(sketch, "E166", {"start": v(126, 6) * mm, "end": v(137.75, 6) * mm, "construction": true});
            skLineSegment(sketch, "E167", {"start": v(137.75, 6) * mm, "end": v(137.75, 17.75) * mm, "construction": true});
            skLineSegment(sketch, "E168", {"start": v(137.75, 17.75) * mm, "end": v(126, 17.75) * mm, "construction": true});
            skCircle(sketch, "E169", {"center": v(137.75, 6) * mm, "radius": 1.05 * mm});
            skCircle(sketch, "E170", {"center": v(126, 17.75) * mm, "radius": 1.05 * mm});
            skCircle(sketch, "E171.0.1.0", {"center": v(137.75, 29.5) * mm, "radius": 1.05 * mm});
            skCircle(sketch, "E171.0.1.1", {"center": v(126, 41.25) * mm, "radius": 1.05 * mm});
            skCircle(sketch, "E171.0.2.0", {"center": v(137.75, 53) * mm, "radius": 1.05 * mm});
            skCircle(sketch, "E171.0.2.1", {"center": v(126, 64.75) * mm, "radius": 1.05 * mm});
            skCircle(sketch, "E171.0.3.0", {"center": v(137.75, 76.5) * mm, "radius": 1.05 * mm});
            skCircle(sketch, "E171.0.3.1", {"center": v(126, 88.25) * mm, "radius": 1.05 * mm});
            skCircle(sketch, "E171.0.4.0", {"center": v(137.75, 100) * mm, "radius": 1.05 * mm});
            skCircle(sketch, "E171.0.4.1", {"center": v(126, 111.75) * mm, "radius": 1.05 * mm});
            skCircle(sketch, "E171.1.0.0", {"center": v(161.25, 6) * mm, "radius": 1.05 * mm});
            skCircle(sketch, "E171.1.0.1", {"center": v(149.5, 17.75) * mm, "radius": 1.05 * mm});
            skCircle(sketch, "E171.1.1.0", {"center": v(161.25, 29.5) * mm, "radius": 1.05 * mm});
            skCircle(sketch, "E171.1.1.1", {"center": v(149.5, 41.25) * mm, "radius": 1.05 * mm});
            skCircle(sketch, "E171.1.2.0", {"center": v(161.25, 53) * mm, "radius": 1.05 * mm});
            skCircle(sketch, "E171.1.2.1", {"center": v(149.5, 64.75) * mm, "radius": 1.05 * mm});
            skCircle(sketch, "E171.1.3.0", {"center": v(161.25, 76.5) * mm, "radius": 1.05 * mm});
            skCircle(sketch, "E171.1.3.1", {"center": v(149.5, 88.25) * mm, "radius": 1.05 * mm});
            skCircle(sketch, "E171.1.4.0", {"center": v(161.25, 100) * mm, "radius": 1.05 * mm});
            skCircle(sketch, "E171.1.4.1", {"center": v(149.5, 111.75) * mm, "radius": 1.05 * mm});
            skCircle(sketch, "E171.2.0.0", {"center": v(184.75, 6) * mm, "radius": 1.05 * mm});
            skCircle(sketch, "E171.2.0.1", {"center": v(173, 17.75) * mm, "radius": 1.05 * mm});
            skCircle(sketch, "E171.2.1.0", {"center": v(184.75, 29.5) * mm, "radius": 1.05 * mm});
            skCircle(sketch, "E171.2.1.1", {"center": v(173, 41.25) * mm, "radius": 1.05 * mm});
            skCircle(sketch, "E171.2.2.0", {"center": v(184.75, 53) * mm, "radius": 1.05 * mm});
            skCircle(sketch, "E171.2.2.1", {"center": v(173, 64.75) * mm, "radius": 1.05 * mm});
            skCircle(sketch, "E171.2.3.0", {"center": v(184.75, 76.5) * mm, "radius": 1.05 * mm});
            skCircle(sketch, "E171.2.3.1", {"center": v(173, 88.25) * mm, "radius": 1.05 * mm});
            skCircle(sketch, "E171.2.4.0", {"center": v(184.75, 100) * mm, "radius": 1.05 * mm});
            skCircle(sketch, "E171.2.4.1", {"center": v(173, 111.75) * mm, "radius": 1.05 * mm});
            skCircle(sketch, "E171.3.0.0", {"center": v(208.25, 6) * mm, "radius": 1.05 * mm});
            skCircle(sketch, "E171.3.0.1", {"center": v(196.5, 17.75) * mm, "radius": 1.05 * mm});
            skCircle(sketch, "E171.3.1.0", {"center": v(208.25, 29.5) * mm, "radius": 1.05 * mm});
            skCircle(sketch, "E171.3.1.1", {"center": v(196.5, 41.25) * mm, "radius": 1.05 * mm});
            skCircle(sketch, "E171.3.2.0", {"center": v(208.25, 53) * mm, "radius": 1.05 * mm});
            skCircle(sketch, "E171.3.2.1", {"center": v(196.5, 64.75) * mm, "radius": 1.05 * mm});
            skCircle(sketch, "E171.3.3.0", {"center": v(208.25, 76.5) * mm, "radius": 1.05 * mm});
            skCircle(sketch, "E171.3.3.1", {"center": v(196.5, 88.25) * mm, "radius": 1.05 * mm});
            skCircle(sketch, "E171.3.4.0", {"center": v(208.25, 100) * mm, "radius": 1.05 * mm});
            skCircle(sketch, "E171.3.4.1", {"center": v(196.5, 111.75) * mm, "radius": 1.05 * mm});
            skCircle(sketch, "E171.4.0.0", {"center": v(231.75, 6) * mm, "radius": 1.05 * mm});
            skCircle(sketch, "E171.4.0.1", {"center": v(220, 17.75) * mm, "radius": 1.05 * mm});
            skCircle(sketch, "E171.4.1.0", {"center": v(231.75, 29.5) * mm, "radius": 1.05 * mm});
            skCircle(sketch, "E171.4.1.1", {"center": v(220, 41.25) * mm, "radius": 1.05 * mm});
            skCircle(sketch, "E171.4.2.0", {"center": v(231.75, 53) * mm, "radius": 1.05 * mm});
            skCircle(sketch, "E171.4.2.1", {"center": v(220, 64.75) * mm, "radius": 1.05 * mm});
            skCircle(sketch, "E171.4.3.0", {"center": v(231.75, 76.5) * mm, "radius": 1.05 * mm});
            skCircle(sketch, "E171.4.3.1", {"center": v(220, 88.25) * mm, "radius": 1.05 * mm});
            skCircle(sketch, "E171.4.4.0", {"center": v(231.75, 100) * mm, "radius": 1.05 * mm});
            skCircle(sketch, "E171.4.4.1", {"center": v(220, 111.75) * mm, "radius": 1.05 * mm});
            skLineSegment(sketch, "E171.direction1", {"start": v(137.75, 6) * mm, "end": v(161.25, 6) * mm, "construction": true});
            skLineSegment(sketch, "E171.direction2", {"start": v(137.75, 6) * mm, "end": v(137.75, 29.5) * mm, "construction": true});
            skSolve(sketch);
        }
        {
            var Q0;
            Q0=qSketchRegion(id+"F30",true);
            extrude(context, id + "F31", {"entities" : qUnion([Q0]), "operationType" : NewBodyOperationType.REMOVE, "endBound" : BoundingType.THROUGH_ALL, "depth" : 25 * mm, "hasSecondDirection" : true, "secondDirectionBound" : SecondDirectionBoundingType.THROUGH_ALL, "secondDirectionOppositeDirection" : true, "secondDirectionDepth" : 25 * mm});
        }
        {
            var Q0;
            Q0=qCreatedBy(makeId("Top.planeOp"),FACE);
            var sketch = newSketch(context, id + "F32", { "sketchPlane" : qUnion([Q0])});
            skLineSegment(sketch, "E172", {"start": v(0, 0) * mm, "end": v(120, 0) * mm, "construction": true});
            skLineSegment(sketch, "E173", {"start": v(120, 0) * mm, "end": v(129.3, 0) * mm, "construction": true});
            skLineSegment(sketch, "E174", {"start": v(129.3, 0) * mm, "end": v(129.3, 9.3) * mm, "construction": true});
            skLineSegment(sketch, "E175.bottom", {"start": v(129.3, 9.3) * mm, "end": v(173, 9.3) * mm, "construction": true});
            skLineSegment(sketch, "E175.top", {"start": v(129.3, 53) * mm, "end": v(173, 53) * mm, "construction": true});
            skLineSegment(sketch, "E175.left", {"start": v(129.3, 9.3) * mm, "end": v(129.3, 53) * mm, "construction": true});
            skLineSegment(sketch, "E175.right", {"start": v(173, 9.3) * mm, "end": v(173, 53) * mm, "construction": true});
            skCircle(sketch, "E176", {"center": v(129.3, 9.3) * mm, "radius": 1.05 * mm});
            skCircle(sketch, "E177", {"center": v(173, 9.3) * mm, "radius": 1.05 * mm});
            skCircle(sketch, "E178", {"center": v(173, 53) * mm, "radius": 1.05 * mm});
            skCircle(sketch, "E179", {"center": v(129.3, 53) * mm, "radius": 1.05 * mm});
            skLineSegment(sketch, "E180", {"start": v(173, 53) * mm, "end": v(196.5, 53) * mm, "construction": true});
            skLineSegment(sketch, "E181", {"start": v(173, 9.3) * mm, "end": v(196.5, 9.3) * mm, "construction": true});
            skCircle(sketch, "E182", {"center": v(196.5, 53) * mm, "radius": 1.05 * mm});
            skCircle(sketch, "E183", {"center": v(196.5, 9.3) * mm, "radius": 1.05 * mm});
            skSolve(sketch);
        }
        {
            var Q0;
            Q0=qSketchRegion(id+"F32",true);
            extrude(context, id + "F33", {"entities" : qUnion([Q0]), "operationType" : NewBodyOperationType.REMOVE, "endBound" : BoundingType.THROUGH_ALL, "oppositeDirection" : true, "depth" : 25 * mm});
        }
        {
            var Q0;
            Q0=qCreatedBy(makeId("Top.planeOp"),FACE);
            var sketch = newSketch(context, id + "F34", { "sketchPlane" : qUnion([Q0])});
            skLineSegment(sketch, "E184", {"start": v(0, 0) * mm, "end": v(120, 0) * mm, "construction": true});
            skLineSegment(sketch, "E185", {"start": v(120, 0) * mm, "end": v(127.5, 0) * mm, "construction": true});
            skLineSegment(sketch, "E186", {"start": v(127.5, 0) * mm, "end": v(127.5, 7.5) * mm, "construction": true});
            skLineSegment(sketch, "E187", {"start": v(127.5, 7.5) * mm, "end": v(137.75, 7.5) * mm, "construction": true});
            skCircle(sketch, "E188.cCircle", {"center": v(137.75, 17.75) * mm, "radius": 10.25 * mm, "construction": true});
            skLineSegment(sketch, "E188.0", {"start": v(142, 7.5) * mm, "end": v(133.5, 7.5) * mm});
            skLineSegment(sketch, "E188.1", {"start": v(133.5, 7.5) * mm, "end": v(127.5, 13.5) * mm});
            skLineSegment(sketch, "E188.2", {"start": v(127.5, 13.5) * mm, "end": v(127.5, 22) * mm});
            skLineSegment(sketch, "E188.3", {"start": v(127.5, 22) * mm, "end": v(133.5, 28) * mm});
            skLineSegment(sketch, "E188.4", {"start": v(133.5, 28) * mm, "end": v(142, 28) * mm});
            skLineSegment(sketch, "E188.5", {"start": v(142, 28) * mm, "end": v(148, 22) * mm});
            skLineSegment(sketch, "E188.6", {"start": v(148, 22) * mm, "end": v(148, 13.5) * mm});
            skLineSegment(sketch, "E188.7", {"start": v(148, 13.5) * mm, "end": v(142, 7.5) * mm});
            skPoint(sketch, "E188.0.midPoint", {"position": v(137.75, 7.5) * mm});
            skPoint(sketch, "E189.0.1.0", {"position": v(137.75, 31) * mm});
            skLineSegment(sketch, "E189.0.1.1", {"start": v(142, 51.5) * mm, "end": v(148, 45.5) * mm});
            skLineSegment(sketch, "E189.0.1.2", {"start": v(137.75, 31) * mm, "end": v(137.75, 41.25) * mm, "construction": true});
            skLineSegment(sketch, "E189.0.1.3", {"start": v(148, 37) * mm, "end": v(142, 31) * mm});
            skLineSegment(sketch, "E189.0.1.4", {"start": v(127.5, 45.5) * mm, "end": v(133.5, 51.5) * mm});
            skLineSegment(sketch, "E189.0.1.5", {"start": v(133.5, 51.5) * mm, "end": v(142, 51.5) * mm});
            skLineSegment(sketch, "E189.0.1.6", {"start": v(148, 45.5) * mm, "end": v(148, 37) * mm});
            skLineSegment(sketch, "E189.0.1.7", {"start": v(142, 31) * mm, "end": v(133.5, 31) * mm});
            skCircle(sketch, "E189.0.1.8", {"center": v(137.75, 41.25) * mm, "radius": 10.25 * mm, "construction": true});
            skLineSegment(sketch, "E189.0.1.9", {"start": v(127.5, 37) * mm, "end": v(127.5, 45.5) * mm});
            skLineSegment(sketch, "E189.0.1.10", {"start": v(133.5, 31) * mm, "end": v(127.5, 37) * mm});
            skPoint(sketch, "E189.0.2.0", {"position": v(137.75, 54.5) * mm});
            skLineSegment(sketch, "E189.0.2.1", {"start": v(142, 75) * mm, "end": v(148, 69) * mm});
            skLineSegment(sketch, "E189.0.2.2", {"start": v(137.75, 54.5) * mm, "end": v(137.75, 64.75) * mm, "construction": true});
            skLineSegment(sketch, "E189.0.2.3", {"start": v(148, 60.5) * mm, "end": v(142, 54.5) * mm});
            skLineSegment(sketch, "E189.0.2.4", {"start": v(127.5, 69) * mm, "end": v(133.5, 75) * mm});
            skLineSegment(sketch, "E189.0.2.5", {"start": v(133.5, 75) * mm, "end": v(142, 75) * mm});
            skLineSegment(sketch, "E189.0.2.6", {"start": v(148, 69) * mm, "end": v(148, 60.5) * mm});
            skLineSegment(sketch, "E189.0.2.7", {"start": v(142, 54.5) * mm, "end": v(133.5, 54.5) * mm});
            skCircle(sketch, "E189.0.2.8", {"center": v(137.75, 64.75) * mm, "radius": 10.25 * mm, "construction": true});
            skLineSegment(sketch, "E189.0.2.9", {"start": v(127.5, 60.5) * mm, "end": v(127.5, 69) * mm});
            skLineSegment(sketch, "E189.0.2.10", {"start": v(133.5, 54.5) * mm, "end": v(127.5, 60.5) * mm});
            skPoint(sketch, "E189.1.0.0", {"position": v(161.25, 7.5) * mm});
            skLineSegment(sketch, "E189.1.0.1", {"start": v(165.5, 28) * mm, "end": v(171.5, 22) * mm});
            skLineSegment(sketch, "E189.1.0.2", {"start": v(161.25, 7.5) * mm, "end": v(161.25, 17.75) * mm, "construction": true});
            skLineSegment(sketch, "E189.1.0.3", {"start": v(171.5, 13.5) * mm, "end": v(165.5, 7.5) * mm});
            skLineSegment(sketch, "E189.1.0.4", {"start": v(151, 22) * mm, "end": v(157, 28) * mm});
            skLineSegment(sketch, "E189.1.0.5", {"start": v(157, 28) * mm, "end": v(165.5, 28) * mm});
            skLineSegment(sketch, "E189.1.0.6", {"start": v(171.5, 22) * mm, "end": v(171.5, 13.5) * mm});
            skLineSegment(sketch, "E189.1.0.7", {"start": v(165.5, 7.5) * mm, "end": v(157, 7.5) * mm});
            skCircle(sketch, "E189.1.0.8", {"center": v(161.25, 17.75) * mm, "radius": 10.25 * mm, "construction": true});
            skLineSegment(sketch, "E189.1.0.9", {"start": v(151, 13.5) * mm, "end": v(151, 22) * mm});
            skLineSegment(sketch, "E189.1.0.10", {"start": v(157, 7.5) * mm, "end": v(151, 13.5) * mm});
            skPoint(sketch, "E189.1.1.0", {"position": v(161.25, 31) * mm});
            skLineSegment(sketch, "E189.1.1.1", {"start": v(165.5, 51.5) * mm, "end": v(171.5, 45.5) * mm});
            skLineSegment(sketch, "E189.1.1.2", {"start": v(161.25, 31) * mm, "end": v(161.25, 41.25) * mm, "construction": true});
            skLineSegment(sketch, "E189.1.1.3", {"start": v(171.5, 37) * mm, "end": v(165.5, 31) * mm});
            skLineSegment(sketch, "E189.1.1.4", {"start": v(151, 45.5) * mm, "end": v(157, 51.5) * mm});
            skLineSegment(sketch, "E189.1.1.5", {"start": v(157, 51.5) * mm, "end": v(165.5, 51.5) * mm});
            skLineSegment(sketch, "E189.1.1.6", {"start": v(171.5, 45.5) * mm, "end": v(171.5, 37) * mm});
            skLineSegment(sketch, "E189.1.1.7", {"start": v(165.5, 31) * mm, "end": v(157, 31) * mm});
            skCircle(sketch, "E189.1.1.8", {"center": v(161.25, 41.25) * mm, "radius": 10.25 * mm, "construction": true});
            skLineSegment(sketch, "E189.1.1.9", {"start": v(151, 37) * mm, "end": v(151, 45.5) * mm});
            skLineSegment(sketch, "E189.1.1.10", {"start": v(157, 31) * mm, "end": v(151, 37) * mm});
            skPoint(sketch, "E189.1.2.0", {"position": v(161.25, 54.5) * mm});
            skLineSegment(sketch, "E189.1.2.1", {"start": v(165.5, 75) * mm, "end": v(171.5, 69) * mm});
            skLineSegment(sketch, "E189.1.2.2", {"start": v(161.25, 54.5) * mm, "end": v(161.25, 64.75) * mm, "construction": true});
            skLineSegment(sketch, "E189.1.2.3", {"start": v(171.5, 60.5) * mm, "end": v(165.5, 54.5) * mm});
            skLineSegment(sketch, "E189.1.2.4", {"start": v(151, 69) * mm, "end": v(157, 75) * mm});
            skLineSegment(sketch, "E189.1.2.5", {"start": v(157, 75) * mm, "end": v(165.5, 75) * mm});
            skLineSegment(sketch, "E189.1.2.6", {"start": v(171.5, 69) * mm, "end": v(171.5, 60.5) * mm});
            skLineSegment(sketch, "E189.1.2.7", {"start": v(165.5, 54.5) * mm, "end": v(157, 54.5) * mm});
            skCircle(sketch, "E189.1.2.8", {"center": v(161.25, 64.75) * mm, "radius": 10.25 * mm, "construction": true});
            skLineSegment(sketch, "E189.1.2.9", {"start": v(151, 60.5) * mm, "end": v(151, 69) * mm});
            skLineSegment(sketch, "E189.1.2.10", {"start": v(157, 54.5) * mm, "end": v(151, 60.5) * mm});
            skPoint(sketch, "E189.2.0.0", {"position": v(184.75, 7.5) * mm});
            skLineSegment(sketch, "E189.2.0.1", {"start": v(189, 28) * mm, "end": v(195, 22) * mm});
            skLineSegment(sketch, "E189.2.0.2", {"start": v(184.75, 7.5) * mm, "end": v(184.75, 17.75) * mm, "construction": true});
            skLineSegment(sketch, "E189.2.0.3", {"start": v(195, 13.5) * mm, "end": v(189, 7.5) * mm});
            skLineSegment(sketch, "E189.2.0.4", {"start": v(174.5, 22) * mm, "end": v(180.5, 28) * mm});
            skLineSegment(sketch, "E189.2.0.5", {"start": v(180.5, 28) * mm, "end": v(189, 28) * mm});
            skLineSegment(sketch, "E189.2.0.6", {"start": v(195, 22) * mm, "end": v(195, 13.5) * mm});
            skLineSegment(sketch, "E189.2.0.7", {"start": v(189, 7.5) * mm, "end": v(180.5, 7.5) * mm});
            skCircle(sketch, "E189.2.0.8", {"center": v(184.75, 17.75) * mm, "radius": 10.25 * mm, "construction": true});
            skLineSegment(sketch, "E189.2.0.9", {"start": v(174.5, 13.5) * mm, "end": v(174.5, 22) * mm});
            skLineSegment(sketch, "E189.2.0.10", {"start": v(180.5, 7.5) * mm, "end": v(174.5, 13.5) * mm});
            skPoint(sketch, "E189.2.1.0", {"position": v(184.75, 31) * mm});
            skLineSegment(sketch, "E189.2.1.1", {"start": v(189, 51.5) * mm, "end": v(195, 45.5) * mm});
            skLineSegment(sketch, "E189.2.1.2", {"start": v(184.75, 31) * mm, "end": v(184.75, 41.25) * mm, "construction": true});
            skLineSegment(sketch, "E189.2.1.3", {"start": v(195, 37) * mm, "end": v(189, 31) * mm});
            skLineSegment(sketch, "E189.2.1.4", {"start": v(174.5, 45.5) * mm, "end": v(180.5, 51.5) * mm});
            skLineSegment(sketch, "E189.2.1.5", {"start": v(180.5, 51.5) * mm, "end": v(189, 51.5) * mm});
            skLineSegment(sketch, "E189.2.1.6", {"start": v(195, 45.5) * mm, "end": v(195, 37) * mm});
            skLineSegment(sketch, "E189.2.1.7", {"start": v(189, 31) * mm, "end": v(180.5, 31) * mm});
            skCircle(sketch, "E189.2.1.8", {"center": v(184.75, 41.25) * mm, "radius": 10.25 * mm, "construction": true});
            skLineSegment(sketch, "E189.2.1.9", {"start": v(174.5, 37) * mm, "end": v(174.5, 45.5) * mm});
            skLineSegment(sketch, "E189.2.1.10", {"start": v(180.5, 31) * mm, "end": v(174.5, 37) * mm});
            skPoint(sketch, "E189.2.2.0", {"position": v(184.75, 54.5) * mm});
            skLineSegment(sketch, "E189.2.2.1", {"start": v(189, 75) * mm, "end": v(195, 69) * mm});
            skLineSegment(sketch, "E189.2.2.2", {"start": v(184.75, 54.5) * mm, "end": v(184.75, 64.75) * mm, "construction": true});
            skLineSegment(sketch, "E189.2.2.3", {"start": v(195, 60.5) * mm, "end": v(189, 54.5) * mm});
            skLineSegment(sketch, "E189.2.2.4", {"start": v(174.5, 69) * mm, "end": v(180.5, 75) * mm});
            skLineSegment(sketch, "E189.2.2.5", {"start": v(180.5, 75) * mm, "end": v(189, 75) * mm});
            skLineSegment(sketch, "E189.2.2.6", {"start": v(195, 69) * mm, "end": v(195, 60.5) * mm});
            skLineSegment(sketch, "E189.2.2.7", {"start": v(189, 54.5) * mm, "end": v(180.5, 54.5) * mm});
            skCircle(sketch, "E189.2.2.8", {"center": v(184.75, 64.75) * mm, "radius": 10.25 * mm, "construction": true});
            skLineSegment(sketch, "E189.2.2.9", {"start": v(174.5, 60.5) * mm, "end": v(174.5, 69) * mm});
            skLineSegment(sketch, "E189.2.2.10", {"start": v(180.5, 54.5) * mm, "end": v(174.5, 60.5) * mm});
            skLineSegment(sketch, "E189.direction1", {"start": v(133.5, 7.5) * mm, "end": v(157, 7.5) * mm, "construction": true});
            skLineSegment(sketch, "E189.direction2", {"start": v(133.5, 7.5) * mm, "end": v(133.5, 31) * mm, "construction": true});
            skLineSegment(sketch, "E190.bottom", {"start": v(127.5, 7.5) * mm, "end": v(124.5, 7.5) * mm});
            skLineSegment(sketch, "E190.top", {"start": v(127.5, 28) * mm, "end": v(124.5, 28) * mm});
            skLineSegment(sketch, "E190.left", {"start": v(127.5, 7.5) * mm, "end": v(127.5, 28) * mm});
            skLineSegment(sketch, "E190.right", {"start": v(124.5, 7.5) * mm, "end": v(124.5, 28) * mm});
            skLineSegment(sketch, "E191.bottom", {"start": v(124.5, 7.5) * mm, "end": v(120, 7.5) * mm});
            skLineSegment(sketch, "E191.top", {"start": v(124.5, 28) * mm, "end": v(120, 28) * mm});
            skLineSegment(sketch, "E191.right", {"start": v(120, 7.5) * mm, "end": v(120, 28) * mm});
            skSolve(sketch);
        }
        {
            var Q0;
            Q0=makeQuery(id+"F34.imprint","IMPRINT",FACE,{"disambiguationData":[TD([[makeQuery(id+"F34.imprint","IMPRINT",EDGE,{"derivedFrom":sQuery(id+"F34.wireOp",EDGE,"E188.0")}),-1.0]])]});
            var Q1;
            Q1=makeQuery(id+"F34.imprint","IMPRINT",FACE,{"disambiguationData":[TD([[makeQuery(id+"F34.imprint","IMPRINT",EDGE,{"derivedFrom":sQuery(id+"F34.wireOp",EDGE,"E189.1.0.1")}),-1.0]])]});
            var Q2;
            Q2=makeQuery(id+"F34.imprint","IMPRINT",FACE,{"disambiguationData":[TD([[makeQuery(id+"F34.imprint","IMPRINT",EDGE,{"derivedFrom":sQuery(id+"F34.wireOp",EDGE,"E189.1.1.1")}),-1.0]])]});
            var Q3;
            Q3=makeQuery(id+"F34.imprint","IMPRINT",FACE,{"disambiguationData":[TD([[makeQuery(id+"F34.imprint","IMPRINT",EDGE,{"derivedFrom":sQuery(id+"F34.wireOp",EDGE,"E189.0.1.1")}),-1.0]])]});
            var Q4;
            Q4=makeQuery(id+"F34.imprint","IMPRINT",FACE,{"disambiguationData":[TD([[makeQuery(id+"F34.imprint","IMPRINT",EDGE,{"derivedFrom":sQuery(id+"F34.wireOp",EDGE,"E190.right")}),1.0]])]});
            extrude(context, id + "F35", {"entities" : qUnion([Q0, Q1, Q2, Q3, Q4]), "operationType" : NewBodyOperationType.REMOVE, "endBound" : BoundingType.THROUGH_ALL, "oppositeDirection" : true, "depth" : 25 * mm});
        }
        {
            var Q0;
            Q0=qCreatedBy(makeId("Top.planeOp"),FACE);
            var sketch = newSketch(context, id + "F36", { "sketchPlane" : qUnion([Q0])});
            skLineSegment(sketch, "E192", {"start": v(0, 0) * mm, "end": v(-120, 0) * mm, "construction": true});
            skLineSegment(sketch, "E193.bottom", {"start": v(-179, 0) * mm, "end": v(-120, 0) * mm});
            skLineSegment(sketch, "E193.top", {"start": v(-179, 59) * mm, "end": v(-120, 59) * mm});
            skLineSegment(sketch, "E193.left", {"start": v(-179, 0) * mm, "end": v(-179, 59) * mm});
            skLineSegment(sketch, "E193.right", {"start": v(-120, 0) * mm, "end": v(-120, 59) * mm});
            skPoint(sketch, "E193.middle", {"position": v(-149.5, 29.5) * mm});
            skLineSegment(sketch, "E194.bottom", {"start": v(-171.35, 51.35) * mm, "end": v(-127.65, 51.35) * mm, "construction": true});
            skLineSegment(sketch, "E194.top", {"start": v(-171.35, 7.65) * mm, "end": v(-127.65, 7.65) * mm, "construction": true});
            skLineSegment(sketch, "E194.left", {"start": v(-171.35, 51.35) * mm, "end": v(-171.35, 7.65) * mm, "construction": true});
            skLineSegment(sketch, "E194.right", {"start": v(-127.65, 51.35) * mm, "end": v(-127.65, 7.65) * mm, "construction": true});
            skCircle(sketch, "E195", {"center": v(-171.35, 51.35) * mm, "radius": 1.05 * mm});
            skCircle(sketch, "E196", {"center": v(-127.65, 51.35) * mm, "radius": 1.05 * mm});
            skCircle(sketch, "E197", {"center": v(-127.65, 7.65) * mm, "radius": 1.05 * mm});
            skCircle(sketch, "E198", {"center": v(-171.35, 7.65) * mm, "radius": 1.05 * mm});
            skLineSegment(sketch, "E199.bottom", {"start": v(-167, 47) * mm, "end": v(-132, 47) * mm});
            skLineSegment(sketch, "E199.top", {"start": v(-167, 12) * mm, "end": v(-132, 12) * mm});
            skLineSegment(sketch, "E199.left", {"start": v(-167, 47) * mm, "end": v(-167, 12) * mm});
            skLineSegment(sketch, "E199.right", {"start": v(-132, 47) * mm, "end": v(-132, 12) * mm});
            skLineSegment(sketch, "E200", {"start": v(-127.65, 7.65) * mm, "end": v(-124.5, 7.65) * mm, "construction": true});
            skLineSegment(sketch, "E201", {"start": v(-124.5, 7.65) * mm, "end": v(-124.5, 10.8) * mm, "construction": true});
            skLineSegment(sketch, "E202.bottom", {"start": v(-124.5, 10.8) * mm, "end": v(-120, 10.8) * mm});
            skLineSegment(sketch, "E202.top", {"start": v(-124.5, 31.3) * mm, "end": v(-120, 31.3) * mm});
            skLineSegment(sketch, "E202.left", {"start": v(-124.5, 10.8) * mm, "end": v(-124.5, 31.3) * mm});
            skLineSegment(sketch, "E202.right", {"start": v(-120, 10.8) * mm, "end": v(-120, 31.3) * mm});
            skSolve(sketch);
        }
        {
            var Q0;
            {var subQ1=sQuery(id+"F36.wireOp",EDGE,"E193.bottom");Q0=makeQuery(id+"F36.imprint","IMPRINT",FACE,{"disambiguationData":[TD([[makeQuery(id+"F36.imprint","IMPRINT",EDGE,{"derivedFrom":subQ1}),1.0]])]});}
            extrude(context, id + "F37", {"entities" : qUnion([Q0]), "oppositeDirection" : true, "depth" : (getVariable(context, 'Grosor') / 2) * mm, "hasSecondDirection" : true, "secondDirectionOppositeDirection" : false, "secondDirectionDepth" : 3 * mm});
        }
        {
            var Q0;
            Q0=qCreatedBy(makeId("Top.planeOp"),FACE);
            var sketch = newSketch(context, id + "F38", { "sketchPlane" : qUnion([Q0])});
            skLineSegment(sketch, "E203", {"start": v(0, 0) * mm, "end": v(-120, 0) * mm, "construction": true});
            skLineSegment(sketch, "E204.bottom", {"start": v(-171.35, 51.35) * mm, "end": v(-127.65, 51.35) * mm, "construction": true});
            skLineSegment(sketch, "E204.top", {"start": v(-171.35, 7.65) * mm, "end": v(-127.65, 7.65) * mm, "construction": true});
            skLineSegment(sketch, "E204.left", {"start": v(-171.35, 51.35) * mm, "end": v(-171.35, 7.65) * mm, "construction": true});
            skLineSegment(sketch, "E204.right", {"start": v(-127.65, 51.35) * mm, "end": v(-127.65, 7.65) * mm, "construction": true});
            skPoint(sketch, "E204.middle", {"position": v(-149.5, 29.5) * mm});
            skCircle(sketch, "E205", {"center": v(-171.35, 51.35) * mm, "radius": 2.1 * mm});
            skCircle(sketch, "E206", {"center": v(-127.65, 51.35) * mm, "radius": 2.1 * mm});
            skCircle(sketch, "E207", {"center": v(-127.65, 7.65) * mm, "radius": 2.1 * mm});
            skCircle(sketch, "E208", {"center": v(-171.35, 7.65) * mm, "radius": 2.1 * mm});
            skLineSegment(sketch, "E209.bottom", {"start": v(-179.5, -0.5) * mm, "end": v(-119.5, -0.5) * mm});
            skLineSegment(sketch, "E209.top", {"start": v(-179.5, 59.5) * mm, "end": v(-119.5, 59.5) * mm});
            skLineSegment(sketch, "E209.left", {"start": v(-179.5, -0.5) * mm, "end": v(-179.5, 59.5) * mm});
            skLineSegment(sketch, "E209.right", {"start": v(-119.5, -0.5) * mm, "end": v(-119.5, 59.5) * mm});
            skSolve(sketch);
        }
        {
            var Q0;
            Q0=qSketchRegion(id+"F38",true);
            extrude(context, id + "F39", {"entities" : qUnion([Q0]), "operationType" : NewBodyOperationType.REMOVE, "depth" : 25 * mm});
        }
        {
            var Q0;
            Q0=makeQuery(id+"F27.opExtrude","SWEPT_EDGE",EDGE,{"disambiguationData":[OSD([sQuery(id+"F26.wireOp",EDGE,"Wud6Z5jM-8rQq-3mEt-tfTX-94YiYB74VQni.bottom"),sQuery(id+"F26.wireOp",EDGE,"Wud6Z5jM-8rQq-3mEt-tfTX-94YiYB74VQni.right")])]});
            var Q1;
            Q1=makeQuery(id+"F27.opExtrude","SWEPT_EDGE",EDGE,{"disambiguationData":[OSD([sQuery(id+"F26.wireOp",EDGE,"Wud6Z5jM-8rQq-3mEt-tfTX-94YiYB74VQni.bottom"),sQuery(id+"F26.wireOp",EDGE,"Wud6Z5jM-8rQq-3mEt-tfTX-94YiYB74VQni.left")])]});
            var Q2;
            Q2=makeQuery(id+"F37.opExtrude","SWEPT_EDGE",EDGE,{"disambiguationData":[OSD([sQuery(id+"F36.wireOp",EDGE,"E193.bottom"),sQuery(id+"F36.wireOp",EDGE,"E193.right")])]});
            var Q3;
            Q3=makeQuery(id+"F37.opExtrude","SWEPT_EDGE",EDGE,{"disambiguationData":[OSD([sQuery(id+"F36.wireOp",EDGE,"E193.bottom"),sQuery(id+"F36.wireOp",EDGE,"E193.left")])]});
            var Q4;
            Q4=makeQuery(id+"F27.opExtrude","SWEPT_EDGE",EDGE,{"disambiguationData":[OSD([sQuery(id+"F26.wireOp",EDGE,"E152.bottom"),sQuery(id+"F26.wireOp",EDGE,"E152.left")])]});
            var Q5;
            Q5=makeQuery(id+"F27.opExtrude","SWEPT_EDGE",EDGE,{"disambiguationData":[OSD([sQuery(id+"F26.wireOp",EDGE,"E152.bottom"),sQuery(id+"F26.wireOp",EDGE,"E152.right")])]});
            fillet(context, id + "F40", {"entities" : qUnion([Q0, Q1, Q2, Q3, Q4, Q5]), "radius" : 3 * mm, "tangentPropagation" : true, "allowEdgeOverflow" : false});
        }
        {
            var Q0;
            Q0=makeQuery(id+"F37.opExtrude","SWEPT_EDGE",EDGE,{"disambiguationData":[OSD([sQuery(id+"F36.wireOp",EDGE,"E193.top"),sQuery(id+"F36.wireOp",EDGE,"E193.left")])]});
            var Q1;
            Q1=makeQuery(id+"F37.opExtrude","SWEPT_EDGE",EDGE,{"disambiguationData":[OSD([sQuery(id+"F36.wireOp",EDGE,"E193.top"),sQuery(id+"F36.wireOp",EDGE,"E193.right")])]});
            var Q2;
            Q2=makeQuery(id+"F27.opExtrude","SWEPT_EDGE",EDGE,{"disambiguationData":[OSD([sQuery(id+"F26.wireOp",EDGE,"Wud6Z5jM-8rQq-3mEt-tfTX-94YiYB74VQni.top"),sQuery(id+"F26.wireOp",EDGE,"Wud6Z5jM-8rQq-3mEt-tfTX-94YiYB74VQni.left")])]});
            var Q3;
            Q3=makeQuery(id+"F27.opExtrude","SWEPT_EDGE",EDGE,{"disambiguationData":[OSD([sQuery(id+"F26.wireOp",EDGE,"Wud6Z5jM-8rQq-3mEt-tfTX-94YiYB74VQni.top"),sQuery(id+"F26.wireOp",EDGE,"Wud6Z5jM-8rQq-3mEt-tfTX-94YiYB74VQni.right")])]});
            var Q4;
            Q4=makeQuery(id+"F27.opExtrude","SWEPT_EDGE",EDGE,{"disambiguationData":[OSD([sQuery(id+"F26.wireOp",EDGE,"E152.top"),sQuery(id+"F26.wireOp",EDGE,"E152.right")])]});
            var Q5;
            Q5=makeQuery(id+"F27.opExtrude","SWEPT_EDGE",EDGE,{"disambiguationData":[OSD([sQuery(id+"F26.wireOp",EDGE,"E152.top"),sQuery(id+"F26.wireOp",EDGE,"E152.left")])]});
            chamfer(context, id + "F41", {"entities" : qUnion([Q0, Q1, Q2, Q3, Q4, Q5]), "width" : 3 * mm, "tangentPropagation" : true});
        }
    });
